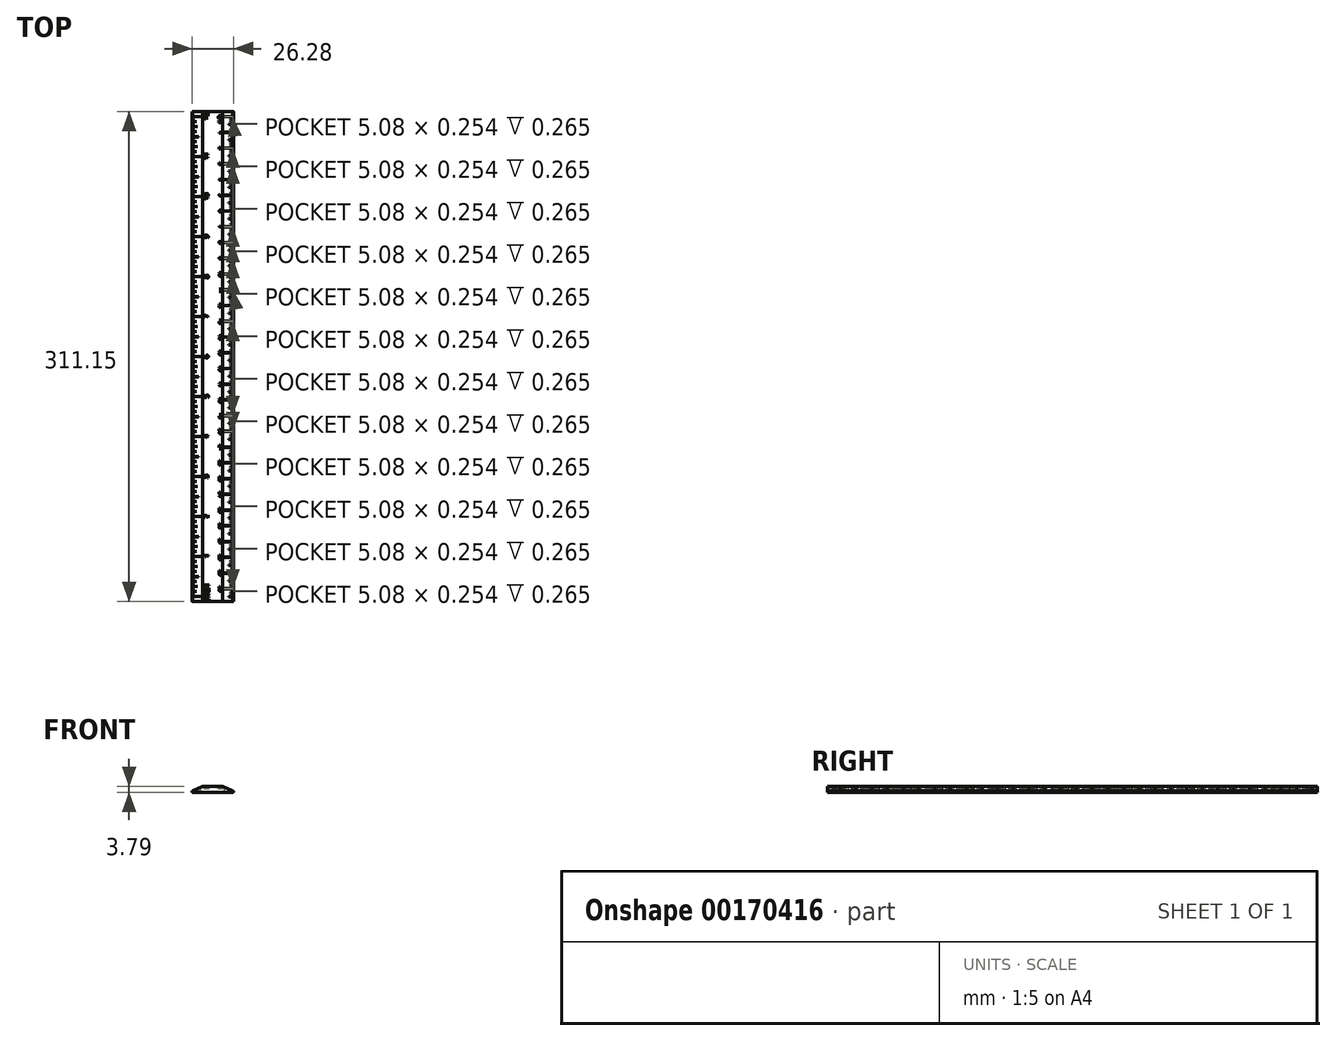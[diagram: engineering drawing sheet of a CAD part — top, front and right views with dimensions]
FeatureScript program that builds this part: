
annotation { "Feature Type Name" : "Feature", "Feature Type Description" : "" }
export const myFeature = defineFeature(function(context is Context, id is Id, definition is map)
    precondition{}
    {
        {
            var Q0;
            Q0=qCreatedBy(makeId("Front.planeOp"),FACE);
            var sketch = newSketch(context, id + "F0", { "sketchPlane" : qUnion([Q0])});
            skLineSegment(sketch, "E0", {"start": v(0, 0) * mm, "end": v(12.7, 0) * mm});
            skLineSegment(sketch, "E1", {"start": v(0, 0) * mm, "end": v(-12.7, 0) * mm});
            skArc(sketch, "E2", {"start": v(-12.7, 0.88) * mm, "mid": v(-13.14, 0.44) * mm, "end": v(-12.7, 0) * mm});
            skLineSegment(sketch, "E3", {"start": v(-12.7, 0.88) * mm, "end": v(-6.35, 3.79) * mm});
            skPoint(sketch, "E3.endSnap0", {"position": v(-6.35, 0) * mm});
            skLineSegment(sketch, "E4", {"start": v(0, 0) * mm, "end": v(0, 3.84) * mm});
            skLineSegment(sketch, "E5.MirrorCS", {"start": v(12.7, 0.88) * mm, "end": v(6.35, 3.79) * mm});
            skArc(sketch, "E6.MirrorCS", {"start": v(12.7, 0.88) * mm, "mid": v(13.14, 0.44) * mm, "end": v(12.7, 0) * mm});
            skLineSegment(sketch, "E7", {"start": v(-6.35, 3.79) * mm, "end": v(6.35, 3.79) * mm});
            skSolve(sketch);
        }
        {
            var Q0;
            Q0 = qSketchRegion(id + "F0", true);
            extrude(context, id + "F1", {"entities" : qUnion([Q0]), "depth" : 311.15 * mm});
        }
        {
            var Q0;
            Q0=makeQuery(id+"F1.opExtrude","SWEPT_FACE",FACE,{"disambiguationData":[OSD([sQuery(id+"F0.wireOp",EDGE,"E7")])]});
            var sketch = newSketch(context, id + "F2", { "sketchPlane" : qUnion([Q0])});
            skLineSegment(sketch, "E8.0.0", {"start": v(-6.35, 0) * mm, "end": v(-12.7, 0) * mm});
            skLineSegment(sketch, "E8.0.1", {"start": v(-12.7, 0) * mm, "end": v(-12.7, -311.15) * mm});
            skLineSegment(sketch, "E8.0.2", {"start": v(-12.7, -311.15) * mm, "end": v(-6.35, -311.15) * mm});
            skLineSegment(sketch, "E8.0.3", {"start": v(-6.35, -311.15) * mm, "end": v(-6.35, 0) * mm});
            skLineSegment(sketch, "E9.0.0", {"start": v(12.7, 0) * mm, "end": v(6.35, 0) * mm});
            skLineSegment(sketch, "E9.0.1", {"start": v(6.35, 0) * mm, "end": v(6.35, -311.15) * mm});
            skLineSegment(sketch, "E9.0.2", {"start": v(6.35, -311.15) * mm, "end": v(12.7, -311.15) * mm});
            skLineSegment(sketch, "E9.0.3", {"start": v(12.7, -311.15) * mm, "end": v(12.7, 0) * mm});
            skLineSegment(sketch, "E10", {"start": v(-12.7, -311.15) * mm, "end": v(-12.7, -308.5) * mm});
            skLineSegment(sketch, "E11", {"start": v(-7.62, -307.98) * mm, "end": v(-7.62, -307.85) * mm});
            skLineSegment(sketch, "E12", {"start": v(-7.62, -307.98) * mm, "end": v(-7.62, -308.1) * mm});
            skLineSegment(sketch, "E13", {"start": v(-7.62, -308.1) * mm, "end": v(-12.7, -308.1) * mm});
            skLineSegment(sketch, "E14", {"start": v(-7.62, -307.85) * mm, "end": v(-12.7, -307.85) * mm});
            skLineSegment(sketch, "E15.0.1.0", {"start": v(-7.62, -282.7) * mm, "end": v(-12.7, -282.7) * mm});
            skLineSegment(sketch, "E15.0.1.1", {"start": v(-7.62, -282.45) * mm, "end": v(-12.7, -282.45) * mm});
            skLineSegment(sketch, "E15.0.1.2", {"start": v(-7.62, -282.58) * mm, "end": v(-7.62, -282.7) * mm});
            skLineSegment(sketch, "E15.0.1.3", {"start": v(-7.62, -282.58) * mm, "end": v(-7.62, -282.45) * mm});
            skLineSegment(sketch, "E15.0.2.0", {"start": v(-7.62, -257.3) * mm, "end": v(-12.7, -257.3) * mm});
            skLineSegment(sketch, "E15.0.2.1", {"start": v(-7.62, -257.05) * mm, "end": v(-12.7, -257.05) * mm});
            skLineSegment(sketch, "E15.0.2.2", {"start": v(-7.62, -257.18) * mm, "end": v(-7.62, -257.3) * mm});
            skLineSegment(sketch, "E15.0.2.3", {"start": v(-7.62, -257.18) * mm, "end": v(-7.62, -257.05) * mm});
            skLineSegment(sketch, "E15.0.3.0", {"start": v(-7.62, -231.9) * mm, "end": v(-12.7, -231.9) * mm});
            skLineSegment(sketch, "E15.0.3.1", {"start": v(-7.62, -231.65) * mm, "end": v(-12.7, -231.65) * mm});
            skLineSegment(sketch, "E15.0.3.2", {"start": v(-7.62, -231.78) * mm, "end": v(-7.62, -231.9) * mm});
            skLineSegment(sketch, "E15.0.3.3", {"start": v(-7.62, -231.78) * mm, "end": v(-7.62, -231.65) * mm});
            skLineSegment(sketch, "E15.0.4.0", {"start": v(-7.62, -206.5) * mm, "end": v(-12.7, -206.5) * mm});
            skLineSegment(sketch, "E15.0.4.1", {"start": v(-7.62, -206.25) * mm, "end": v(-12.7, -206.25) * mm});
            skLineSegment(sketch, "E15.0.4.2", {"start": v(-7.62, -206.38) * mm, "end": v(-7.62, -206.5) * mm});
            skLineSegment(sketch, "E15.0.4.3", {"start": v(-7.62, -206.38) * mm, "end": v(-7.62, -206.25) * mm});
            skLineSegment(sketch, "E15.0.5.0", {"start": v(-7.62, -181.1) * mm, "end": v(-12.7, -181.1) * mm});
            skLineSegment(sketch, "E15.0.5.1", {"start": v(-7.62, -180.85) * mm, "end": v(-12.7, -180.85) * mm});
            skLineSegment(sketch, "E15.0.5.2", {"start": v(-7.62, -180.98) * mm, "end": v(-7.62, -181.1) * mm});
            skLineSegment(sketch, "E15.0.5.3", {"start": v(-7.62, -180.98) * mm, "end": v(-7.62, -180.85) * mm});
            skLineSegment(sketch, "E15.0.6.0", {"start": v(-7.62, -155.7) * mm, "end": v(-12.7, -155.7) * mm});
            skLineSegment(sketch, "E15.0.6.1", {"start": v(-7.62, -155.45) * mm, "end": v(-12.7, -155.45) * mm});
            skLineSegment(sketch, "E15.0.6.2", {"start": v(-7.62, -155.58) * mm, "end": v(-7.62, -155.7) * mm});
            skLineSegment(sketch, "E15.0.6.3", {"start": v(-7.62, -155.58) * mm, "end": v(-7.62, -155.45) * mm});
            skLineSegment(sketch, "E15.0.7.0", {"start": v(-7.62, -130.3) * mm, "end": v(-12.7, -130.3) * mm});
            skLineSegment(sketch, "E15.0.7.1", {"start": v(-7.62, -130.05) * mm, "end": v(-12.7, -130.05) * mm});
            skLineSegment(sketch, "E15.0.7.2", {"start": v(-7.62, -130.18) * mm, "end": v(-7.62, -130.3) * mm});
            skLineSegment(sketch, "E15.0.7.3", {"start": v(-7.62, -130.18) * mm, "end": v(-7.62, -130.05) * mm});
            skLineSegment(sketch, "E15.0.8.0", {"start": v(-7.62, -104.9) * mm, "end": v(-12.7, -104.9) * mm});
            skLineSegment(sketch, "E15.0.8.1", {"start": v(-7.62, -104.65) * mm, "end": v(-12.7, -104.65) * mm});
            skLineSegment(sketch, "E15.0.8.2", {"start": v(-7.62, -104.78) * mm, "end": v(-7.62, -104.9) * mm});
            skLineSegment(sketch, "E15.0.8.3", {"start": v(-7.62, -104.78) * mm, "end": v(-7.62, -104.65) * mm});
            skLineSegment(sketch, "E15.0.9.0", {"start": v(-7.62, -79.5) * mm, "end": v(-12.7, -79.5) * mm});
            skLineSegment(sketch, "E15.0.9.1", {"start": v(-7.62, -79.25) * mm, "end": v(-12.7, -79.25) * mm});
            skLineSegment(sketch, "E15.0.9.2", {"start": v(-7.62, -79.38) * mm, "end": v(-7.62, -79.5) * mm});
            skLineSegment(sketch, "E15.0.9.3", {"start": v(-7.62, -79.38) * mm, "end": v(-7.62, -79.25) * mm});
            skLineSegment(sketch, "E15.0.10.0", {"start": v(-7.62, -54.1) * mm, "end": v(-12.7, -54.1) * mm});
            skLineSegment(sketch, "E15.0.10.1", {"start": v(-7.62, -53.85) * mm, "end": v(-12.7, -53.85) * mm});
            skLineSegment(sketch, "E15.0.10.2", {"start": v(-7.62, -53.98) * mm, "end": v(-7.62, -54.1) * mm});
            skLineSegment(sketch, "E15.0.10.3", {"start": v(-7.62, -53.98) * mm, "end": v(-7.62, -53.85) * mm});
            skLineSegment(sketch, "E15.0.11.0", {"start": v(-7.62, -28.7) * mm, "end": v(-12.7, -28.7) * mm});
            skLineSegment(sketch, "E15.0.11.1", {"start": v(-7.62, -28.45) * mm, "end": v(-12.7, -28.45) * mm});
            skLineSegment(sketch, "E15.0.11.2", {"start": v(-7.62, -28.58) * mm, "end": v(-7.62, -28.7) * mm});
            skLineSegment(sketch, "E15.0.11.3", {"start": v(-7.62, -28.58) * mm, "end": v(-7.62, -28.45) * mm});
            skLineSegment(sketch, "E15.direction1", {"start": v(-12.7, -308.1) * mm, "end": v(12.7, -308.1) * mm, "construction": true});
            skLineSegment(sketch, "E15.direction2", {"start": v(-12.7, -308.1) * mm, "end": v(-12.7, -282.7) * mm, "construction": true});
            skLineSegment(sketch, "E16.0.0.12", {"start": v(-7.62, -3.3) * mm, "end": v(-12.7, -3.3) * mm});
            skLineSegment(sketch, "E16.3.0.12", {"start": v(-7.62, -3.05) * mm, "end": v(-12.7, -3.05) * mm});
            skLineSegment(sketch, "E16.6.0.12", {"start": v(-7.62, -3.18) * mm, "end": v(-7.62, -3.3) * mm});
            skLineSegment(sketch, "E16.9.0.12", {"start": v(-7.62, -3.18) * mm, "end": v(-7.62, -3.05) * mm});
            skLineSegment(sketch, "E17", {"start": v(-12.7, -308.1) * mm, "end": v(-12.7, -307.85) * mm});
            skPoint(sketch, "E18", {"position": v(-12.7, -307.98) * mm});
            skLineSegment(sketch, "E19", {"start": v(-12.7, -307.98) * mm, "end": v(-12.7, -307.25) * mm});
            skLineSegment(sketch, "E20", {"start": v(-12.7, -306.39) * mm, "end": v(-12.7, -306.63) * mm});
            skLineSegment(sketch, "E21", {"start": v(-11.43, -306.39) * mm, "end": v(-11.43, -306.51) * mm});
            skLineSegment(sketch, "E22", {"start": v(-11.43, -306.39) * mm, "end": v(-11.43, -306.26) * mm});
            skLineSegment(sketch, "E23", {"start": v(-11.43, -306.51) * mm, "end": v(-12.7, -306.51) * mm});
            skLineSegment(sketch, "E24", {"start": v(-11.43, -306.26) * mm, "end": v(-12.7, -306.26) * mm});
            skPoint(sketch, "E25.orphan", {"position": v(-12.14, -306.39) * mm});
            skPoint(sketch, "E26.start.orphan", {"position": v(-12.14, -307.98) * mm});
            skLineSegment(sketch, "E27.0.1.0", {"start": v(-11.43, -303.34) * mm, "end": v(-12.7, -303.34) * mm});
            skLineSegment(sketch, "E27.0.1.1", {"start": v(-11.43, -303.09) * mm, "end": v(-12.7, -303.09) * mm});
            skLineSegment(sketch, "E27.0.1.2", {"start": v(-11.43, -303.21) * mm, "end": v(-11.43, -303.34) * mm});
            skLineSegment(sketch, "E27.0.1.3", {"start": v(-11.43, -303.21) * mm, "end": v(-11.43, -303.09) * mm});
            skLineSegment(sketch, "E27.0.2.0", {"start": v(-11.43, -300.16) * mm, "end": v(-12.7, -300.16) * mm});
            skLineSegment(sketch, "E27.0.2.1", {"start": v(-11.43, -299.91) * mm, "end": v(-12.7, -299.91) * mm});
            skLineSegment(sketch, "E27.0.2.2", {"start": v(-11.43, -300.04) * mm, "end": v(-11.43, -300.16) * mm});
            skLineSegment(sketch, "E27.0.2.3", {"start": v(-11.43, -300.04) * mm, "end": v(-11.43, -299.91) * mm});
            skLineSegment(sketch, "E27.0.3.0", {"start": v(-11.43, -296.99) * mm, "end": v(-12.7, -296.99) * mm});
            skLineSegment(sketch, "E27.0.3.1", {"start": v(-11.43, -296.74) * mm, "end": v(-12.7, -296.74) * mm});
            skLineSegment(sketch, "E27.0.3.2", {"start": v(-11.43, -296.86) * mm, "end": v(-11.43, -296.99) * mm});
            skLineSegment(sketch, "E27.0.3.3", {"start": v(-11.43, -296.86) * mm, "end": v(-11.43, -296.74) * mm});
            skLineSegment(sketch, "E27.0.4.0", {"start": v(-11.43, -293.81) * mm, "end": v(-12.7, -293.81) * mm});
            skLineSegment(sketch, "E27.0.4.1", {"start": v(-11.43, -293.56) * mm, "end": v(-12.7, -293.56) * mm});
            skLineSegment(sketch, "E27.0.4.2", {"start": v(-11.43, -293.69) * mm, "end": v(-11.43, -293.81) * mm});
            skLineSegment(sketch, "E27.0.4.3", {"start": v(-11.43, -293.69) * mm, "end": v(-11.43, -293.56) * mm});
            skLineSegment(sketch, "E27.0.5.0", {"start": v(-11.43, -290.64) * mm, "end": v(-12.7, -290.64) * mm});
            skLineSegment(sketch, "E27.0.5.1", {"start": v(-11.43, -290.39) * mm, "end": v(-12.7, -290.39) * mm});
            skLineSegment(sketch, "E27.0.5.2", {"start": v(-11.43, -290.51) * mm, "end": v(-11.43, -290.64) * mm});
            skLineSegment(sketch, "E27.0.5.3", {"start": v(-11.43, -290.51) * mm, "end": v(-11.43, -290.39) * mm});
            skLineSegment(sketch, "E27.0.6.0", {"start": v(-11.43, -287.46) * mm, "end": v(-12.7, -287.46) * mm});
            skLineSegment(sketch, "E27.0.6.1", {"start": v(-11.43, -287.21) * mm, "end": v(-12.7, -287.21) * mm});
            skLineSegment(sketch, "E27.0.6.2", {"start": v(-11.43, -287.34) * mm, "end": v(-11.43, -287.46) * mm});
            skLineSegment(sketch, "E27.0.6.3", {"start": v(-11.43, -287.34) * mm, "end": v(-11.43, -287.21) * mm});
            skLineSegment(sketch, "E27.0.7.0", {"start": v(-11.43, -284.29) * mm, "end": v(-12.7, -284.29) * mm});
            skLineSegment(sketch, "E27.0.7.1", {"start": v(-11.43, -284.04) * mm, "end": v(-12.7, -284.04) * mm});
            skLineSegment(sketch, "E27.0.7.2", {"start": v(-11.43, -284.16) * mm, "end": v(-11.43, -284.29) * mm});
            skLineSegment(sketch, "E27.0.7.3", {"start": v(-11.43, -284.16) * mm, "end": v(-11.43, -284.04) * mm});
            skLineSegment(sketch, "E27.0.8.0", {"start": v(-11.43, -281.11) * mm, "end": v(-12.7, -281.11) * mm});
            skLineSegment(sketch, "E27.0.8.1", {"start": v(-11.43, -280.86) * mm, "end": v(-12.7, -280.86) * mm});
            skLineSegment(sketch, "E27.0.8.2", {"start": v(-11.43, -280.99) * mm, "end": v(-11.43, -281.11) * mm});
            skLineSegment(sketch, "E27.0.8.3", {"start": v(-11.43, -280.99) * mm, "end": v(-11.43, -280.86) * mm});
            skLineSegment(sketch, "E27.0.9.0", {"start": v(-11.43, -277.94) * mm, "end": v(-12.7, -277.94) * mm});
            skLineSegment(sketch, "E27.0.9.1", {"start": v(-11.43, -277.69) * mm, "end": v(-12.7, -277.69) * mm});
            skLineSegment(sketch, "E27.0.9.2", {"start": v(-11.43, -277.81) * mm, "end": v(-11.43, -277.94) * mm});
            skLineSegment(sketch, "E27.0.9.3", {"start": v(-11.43, -277.81) * mm, "end": v(-11.43, -277.69) * mm});
            skLineSegment(sketch, "E27.0.10.0", {"start": v(-11.43, -274.76) * mm, "end": v(-12.7, -274.76) * mm});
            skLineSegment(sketch, "E27.0.10.1", {"start": v(-11.43, -274.51) * mm, "end": v(-12.7, -274.51) * mm});
            skLineSegment(sketch, "E27.0.10.2", {"start": v(-11.43, -274.64) * mm, "end": v(-11.43, -274.76) * mm});
            skLineSegment(sketch, "E27.0.10.3", {"start": v(-11.43, -274.64) * mm, "end": v(-11.43, -274.51) * mm});
            skLineSegment(sketch, "E27.0.11.0", {"start": v(-11.43, -271.59) * mm, "end": v(-12.7, -271.59) * mm});
            skLineSegment(sketch, "E27.0.11.1", {"start": v(-11.43, -271.34) * mm, "end": v(-12.7, -271.34) * mm});
            skLineSegment(sketch, "E27.0.11.2", {"start": v(-11.43, -271.46) * mm, "end": v(-11.43, -271.59) * mm});
            skLineSegment(sketch, "E27.0.11.3", {"start": v(-11.43, -271.46) * mm, "end": v(-11.43, -271.34) * mm});
            skLineSegment(sketch, "E27.0.12.0", {"start": v(-11.43, -268.41) * mm, "end": v(-12.7, -268.41) * mm});
            skLineSegment(sketch, "E27.0.12.1", {"start": v(-11.43, -268.16) * mm, "end": v(-12.7, -268.16) * mm});
            skLineSegment(sketch, "E27.0.12.2", {"start": v(-11.43, -268.29) * mm, "end": v(-11.43, -268.41) * mm});
            skLineSegment(sketch, "E27.0.12.3", {"start": v(-11.43, -268.29) * mm, "end": v(-11.43, -268.16) * mm});
            skLineSegment(sketch, "E27.0.13.0", {"start": v(-11.43, -265.24) * mm, "end": v(-12.7, -265.24) * mm});
            skLineSegment(sketch, "E27.0.13.1", {"start": v(-11.43, -264.99) * mm, "end": v(-12.7, -264.99) * mm});
            skLineSegment(sketch, "E27.0.13.2", {"start": v(-11.43, -265.11) * mm, "end": v(-11.43, -265.24) * mm});
            skLineSegment(sketch, "E27.0.13.3", {"start": v(-11.43, -265.11) * mm, "end": v(-11.43, -264.99) * mm});
            skLineSegment(sketch, "E27.0.14.0", {"start": v(-11.43, -262.06) * mm, "end": v(-12.7, -262.06) * mm});
            skLineSegment(sketch, "E27.0.14.1", {"start": v(-11.43, -261.81) * mm, "end": v(-12.7, -261.81) * mm});
            skLineSegment(sketch, "E27.0.14.2", {"start": v(-11.43, -261.94) * mm, "end": v(-11.43, -262.06) * mm});
            skLineSegment(sketch, "E27.0.14.3", {"start": v(-11.43, -261.94) * mm, "end": v(-11.43, -261.81) * mm});
            skLineSegment(sketch, "E27.0.15.0", {"start": v(-11.43, -258.89) * mm, "end": v(-12.7, -258.89) * mm});
            skLineSegment(sketch, "E27.0.15.1", {"start": v(-11.43, -258.64) * mm, "end": v(-12.7, -258.64) * mm});
            skLineSegment(sketch, "E27.0.15.2", {"start": v(-11.43, -258.76) * mm, "end": v(-11.43, -258.89) * mm});
            skLineSegment(sketch, "E27.0.15.3", {"start": v(-11.43, -258.76) * mm, "end": v(-11.43, -258.64) * mm});
            skLineSegment(sketch, "E27.0.16.0", {"start": v(-11.43, -255.71) * mm, "end": v(-12.7, -255.71) * mm});
            skLineSegment(sketch, "E27.0.16.1", {"start": v(-11.43, -255.46) * mm, "end": v(-12.7, -255.46) * mm});
            skLineSegment(sketch, "E27.0.16.2", {"start": v(-11.43, -255.59) * mm, "end": v(-11.43, -255.71) * mm});
            skLineSegment(sketch, "E27.0.16.3", {"start": v(-11.43, -255.59) * mm, "end": v(-11.43, -255.46) * mm});
            skLineSegment(sketch, "E27.0.17.0", {"start": v(-11.43, -252.54) * mm, "end": v(-12.7, -252.54) * mm});
            skLineSegment(sketch, "E27.0.17.1", {"start": v(-11.43, -252.29) * mm, "end": v(-12.7, -252.29) * mm});
            skLineSegment(sketch, "E27.0.17.2", {"start": v(-11.43, -252.41) * mm, "end": v(-11.43, -252.54) * mm});
            skLineSegment(sketch, "E27.0.17.3", {"start": v(-11.43, -252.41) * mm, "end": v(-11.43, -252.29) * mm});
            skLineSegment(sketch, "E27.0.18.0", {"start": v(-11.43, -249.36) * mm, "end": v(-12.7, -249.36) * mm});
            skLineSegment(sketch, "E27.0.18.1", {"start": v(-11.43, -249.11) * mm, "end": v(-12.7, -249.11) * mm});
            skLineSegment(sketch, "E27.0.18.2", {"start": v(-11.43, -249.24) * mm, "end": v(-11.43, -249.36) * mm});
            skLineSegment(sketch, "E27.0.18.3", {"start": v(-11.43, -249.24) * mm, "end": v(-11.43, -249.11) * mm});
            skLineSegment(sketch, "E27.0.19.0", {"start": v(-11.43, -246.19) * mm, "end": v(-12.7, -246.19) * mm});
            skLineSegment(sketch, "E27.0.19.1", {"start": v(-11.43, -245.94) * mm, "end": v(-12.7, -245.94) * mm});
            skLineSegment(sketch, "E27.0.19.2", {"start": v(-11.43, -246.06) * mm, "end": v(-11.43, -246.19) * mm});
            skLineSegment(sketch, "E27.0.19.3", {"start": v(-11.43, -246.06) * mm, "end": v(-11.43, -245.94) * mm});
            skLineSegment(sketch, "E27.0.20.0", {"start": v(-11.43, -243.01) * mm, "end": v(-12.7, -243.01) * mm});
            skLineSegment(sketch, "E27.0.20.1", {"start": v(-11.43, -242.76) * mm, "end": v(-12.7, -242.76) * mm});
            skLineSegment(sketch, "E27.0.20.2", {"start": v(-11.43, -242.89) * mm, "end": v(-11.43, -243.01) * mm});
            skLineSegment(sketch, "E27.0.20.3", {"start": v(-11.43, -242.89) * mm, "end": v(-11.43, -242.76) * mm});
            skLineSegment(sketch, "E27.0.21.0", {"start": v(-11.43, -239.84) * mm, "end": v(-12.7, -239.84) * mm});
            skLineSegment(sketch, "E27.0.21.1", {"start": v(-11.43, -239.59) * mm, "end": v(-12.7, -239.59) * mm});
            skLineSegment(sketch, "E27.0.21.2", {"start": v(-11.43, -239.71) * mm, "end": v(-11.43, -239.84) * mm});
            skLineSegment(sketch, "E27.0.21.3", {"start": v(-11.43, -239.71) * mm, "end": v(-11.43, -239.59) * mm});
            skLineSegment(sketch, "E27.0.22.0", {"start": v(-11.43, -236.66) * mm, "end": v(-12.7, -236.66) * mm});
            skLineSegment(sketch, "E27.0.22.1", {"start": v(-11.43, -236.41) * mm, "end": v(-12.7, -236.41) * mm});
            skLineSegment(sketch, "E27.0.22.2", {"start": v(-11.43, -236.54) * mm, "end": v(-11.43, -236.66) * mm});
            skLineSegment(sketch, "E27.0.22.3", {"start": v(-11.43, -236.54) * mm, "end": v(-11.43, -236.41) * mm});
            skLineSegment(sketch, "E27.0.23.0", {"start": v(-11.43, -233.49) * mm, "end": v(-12.7, -233.49) * mm});
            skLineSegment(sketch, "E27.0.23.1", {"start": v(-11.43, -233.24) * mm, "end": v(-12.7, -233.24) * mm});
            skLineSegment(sketch, "E27.0.23.2", {"start": v(-11.43, -233.36) * mm, "end": v(-11.43, -233.49) * mm});
            skLineSegment(sketch, "E27.0.23.3", {"start": v(-11.43, -233.36) * mm, "end": v(-11.43, -233.24) * mm});
            skLineSegment(sketch, "E27.0.24.0", {"start": v(-11.43, -230.31) * mm, "end": v(-12.7, -230.31) * mm});
            skLineSegment(sketch, "E27.0.24.1", {"start": v(-11.43, -230.06) * mm, "end": v(-12.7, -230.06) * mm});
            skLineSegment(sketch, "E27.0.24.2", {"start": v(-11.43, -230.19) * mm, "end": v(-11.43, -230.31) * mm});
            skLineSegment(sketch, "E27.0.24.3", {"start": v(-11.43, -230.19) * mm, "end": v(-11.43, -230.06) * mm});
            skLineSegment(sketch, "E27.0.25.0", {"start": v(-11.43, -227.14) * mm, "end": v(-12.7, -227.14) * mm});
            skLineSegment(sketch, "E27.0.25.1", {"start": v(-11.43, -226.89) * mm, "end": v(-12.7, -226.89) * mm});
            skLineSegment(sketch, "E27.0.25.2", {"start": v(-11.43, -227.01) * mm, "end": v(-11.43, -227.14) * mm});
            skLineSegment(sketch, "E27.0.25.3", {"start": v(-11.43, -227.01) * mm, "end": v(-11.43, -226.89) * mm});
            skLineSegment(sketch, "E27.0.26.0", {"start": v(-11.43, -223.96) * mm, "end": v(-12.7, -223.96) * mm});
            skLineSegment(sketch, "E27.0.26.1", {"start": v(-11.43, -223.71) * mm, "end": v(-12.7, -223.71) * mm});
            skLineSegment(sketch, "E27.0.26.2", {"start": v(-11.43, -223.84) * mm, "end": v(-11.43, -223.96) * mm});
            skLineSegment(sketch, "E27.0.26.3", {"start": v(-11.43, -223.84) * mm, "end": v(-11.43, -223.71) * mm});
            skLineSegment(sketch, "E27.0.27.0", {"start": v(-11.43, -220.79) * mm, "end": v(-12.7, -220.79) * mm});
            skLineSegment(sketch, "E27.0.27.1", {"start": v(-11.43, -220.54) * mm, "end": v(-12.7, -220.54) * mm});
            skLineSegment(sketch, "E27.0.27.2", {"start": v(-11.43, -220.66) * mm, "end": v(-11.43, -220.79) * mm});
            skLineSegment(sketch, "E27.0.27.3", {"start": v(-11.43, -220.66) * mm, "end": v(-11.43, -220.54) * mm});
            skLineSegment(sketch, "E27.0.28.0", {"start": v(-11.43, -217.61) * mm, "end": v(-12.7, -217.61) * mm});
            skLineSegment(sketch, "E27.0.28.1", {"start": v(-11.43, -217.36) * mm, "end": v(-12.7, -217.36) * mm});
            skLineSegment(sketch, "E27.0.28.2", {"start": v(-11.43, -217.49) * mm, "end": v(-11.43, -217.61) * mm});
            skLineSegment(sketch, "E27.0.28.3", {"start": v(-11.43, -217.49) * mm, "end": v(-11.43, -217.36) * mm});
            skLineSegment(sketch, "E27.0.29.0", {"start": v(-11.43, -214.44) * mm, "end": v(-12.7, -214.44) * mm});
            skLineSegment(sketch, "E27.0.29.1", {"start": v(-11.43, -214.19) * mm, "end": v(-12.7, -214.19) * mm});
            skLineSegment(sketch, "E27.0.29.2", {"start": v(-11.43, -214.31) * mm, "end": v(-11.43, -214.44) * mm});
            skLineSegment(sketch, "E27.0.29.3", {"start": v(-11.43, -214.31) * mm, "end": v(-11.43, -214.19) * mm});
            skLineSegment(sketch, "E27.0.30.0", {"start": v(-11.43, -211.26) * mm, "end": v(-12.7, -211.26) * mm});
            skLineSegment(sketch, "E27.0.30.1", {"start": v(-11.43, -211.01) * mm, "end": v(-12.7, -211.01) * mm});
            skLineSegment(sketch, "E27.0.30.2", {"start": v(-11.43, -211.14) * mm, "end": v(-11.43, -211.26) * mm});
            skLineSegment(sketch, "E27.0.30.3", {"start": v(-11.43, -211.14) * mm, "end": v(-11.43, -211.01) * mm});
            skLineSegment(sketch, "E27.0.31.0", {"start": v(-11.43, -208.09) * mm, "end": v(-12.7, -208.09) * mm});
            skLineSegment(sketch, "E27.0.31.1", {"start": v(-11.43, -207.84) * mm, "end": v(-12.7, -207.84) * mm});
            skLineSegment(sketch, "E27.0.31.2", {"start": v(-11.43, -207.96) * mm, "end": v(-11.43, -208.09) * mm});
            skLineSegment(sketch, "E27.0.31.3", {"start": v(-11.43, -207.96) * mm, "end": v(-11.43, -207.84) * mm});
            skLineSegment(sketch, "E27.0.32.0", {"start": v(-11.43, -204.91) * mm, "end": v(-12.7, -204.91) * mm});
            skLineSegment(sketch, "E27.0.32.1", {"start": v(-11.43, -204.66) * mm, "end": v(-12.7, -204.66) * mm});
            skLineSegment(sketch, "E27.0.32.2", {"start": v(-11.43, -204.79) * mm, "end": v(-11.43, -204.91) * mm});
            skLineSegment(sketch, "E27.0.32.3", {"start": v(-11.43, -204.79) * mm, "end": v(-11.43, -204.66) * mm});
            skLineSegment(sketch, "E27.0.33.0", {"start": v(-11.43, -201.74) * mm, "end": v(-12.7, -201.74) * mm});
            skLineSegment(sketch, "E27.0.33.1", {"start": v(-11.43, -201.49) * mm, "end": v(-12.7, -201.49) * mm});
            skLineSegment(sketch, "E27.0.33.2", {"start": v(-11.43, -201.61) * mm, "end": v(-11.43, -201.74) * mm});
            skLineSegment(sketch, "E27.0.33.3", {"start": v(-11.43, -201.61) * mm, "end": v(-11.43, -201.49) * mm});
            skLineSegment(sketch, "E27.0.34.0", {"start": v(-11.43, -198.56) * mm, "end": v(-12.7, -198.56) * mm});
            skLineSegment(sketch, "E27.0.34.1", {"start": v(-11.43, -198.31) * mm, "end": v(-12.7, -198.31) * mm});
            skLineSegment(sketch, "E27.0.34.2", {"start": v(-11.43, -198.44) * mm, "end": v(-11.43, -198.56) * mm});
            skLineSegment(sketch, "E27.0.34.3", {"start": v(-11.43, -198.44) * mm, "end": v(-11.43, -198.31) * mm});
            skLineSegment(sketch, "E27.0.35.0", {"start": v(-11.43, -195.39) * mm, "end": v(-12.7, -195.39) * mm});
            skLineSegment(sketch, "E27.0.35.1", {"start": v(-11.43, -195.14) * mm, "end": v(-12.7, -195.14) * mm});
            skLineSegment(sketch, "E27.0.35.2", {"start": v(-11.43, -195.26) * mm, "end": v(-11.43, -195.39) * mm});
            skLineSegment(sketch, "E27.0.35.3", {"start": v(-11.43, -195.26) * mm, "end": v(-11.43, -195.14) * mm});
            skLineSegment(sketch, "E27.0.36.0", {"start": v(-11.43, -192.21) * mm, "end": v(-12.7, -192.21) * mm});
            skLineSegment(sketch, "E27.0.36.1", {"start": v(-11.43, -191.96) * mm, "end": v(-12.7, -191.96) * mm});
            skLineSegment(sketch, "E27.0.36.2", {"start": v(-11.43, -192.09) * mm, "end": v(-11.43, -192.21) * mm});
            skLineSegment(sketch, "E27.0.36.3", {"start": v(-11.43, -192.09) * mm, "end": v(-11.43, -191.96) * mm});
            skLineSegment(sketch, "E27.0.37.0", {"start": v(-11.43, -189.04) * mm, "end": v(-12.7, -189.04) * mm});
            skLineSegment(sketch, "E27.0.37.1", {"start": v(-11.43, -188.79) * mm, "end": v(-12.7, -188.79) * mm});
            skLineSegment(sketch, "E27.0.37.2", {"start": v(-11.43, -188.91) * mm, "end": v(-11.43, -189.04) * mm});
            skLineSegment(sketch, "E27.0.37.3", {"start": v(-11.43, -188.91) * mm, "end": v(-11.43, -188.79) * mm});
            skLineSegment(sketch, "E27.0.38.0", {"start": v(-11.43, -185.86) * mm, "end": v(-12.7, -185.86) * mm});
            skLineSegment(sketch, "E27.0.38.1", {"start": v(-11.43, -185.61) * mm, "end": v(-12.7, -185.61) * mm});
            skLineSegment(sketch, "E27.0.38.2", {"start": v(-11.43, -185.74) * mm, "end": v(-11.43, -185.86) * mm});
            skLineSegment(sketch, "E27.0.38.3", {"start": v(-11.43, -185.74) * mm, "end": v(-11.43, -185.61) * mm});
            skLineSegment(sketch, "E27.0.39.0", {"start": v(-11.43, -182.69) * mm, "end": v(-12.7, -182.69) * mm});
            skLineSegment(sketch, "E27.0.39.1", {"start": v(-11.43, -182.44) * mm, "end": v(-12.7, -182.44) * mm});
            skLineSegment(sketch, "E27.0.39.2", {"start": v(-11.43, -182.56) * mm, "end": v(-11.43, -182.69) * mm});
            skLineSegment(sketch, "E27.0.39.3", {"start": v(-11.43, -182.56) * mm, "end": v(-11.43, -182.44) * mm});
            skLineSegment(sketch, "E27.0.40.0", {"start": v(-11.43, -179.51) * mm, "end": v(-12.7, -179.51) * mm});
            skLineSegment(sketch, "E27.0.40.1", {"start": v(-11.43, -179.26) * mm, "end": v(-12.7, -179.26) * mm});
            skLineSegment(sketch, "E27.0.40.2", {"start": v(-11.43, -179.39) * mm, "end": v(-11.43, -179.51) * mm});
            skLineSegment(sketch, "E27.0.40.3", {"start": v(-11.43, -179.39) * mm, "end": v(-11.43, -179.26) * mm});
            skLineSegment(sketch, "E27.0.41.0", {"start": v(-11.43, -176.34) * mm, "end": v(-12.7, -176.34) * mm});
            skLineSegment(sketch, "E27.0.41.1", {"start": v(-11.43, -176.09) * mm, "end": v(-12.7, -176.09) * mm});
            skLineSegment(sketch, "E27.0.41.2", {"start": v(-11.43, -176.21) * mm, "end": v(-11.43, -176.34) * mm});
            skLineSegment(sketch, "E27.0.41.3", {"start": v(-11.43, -176.21) * mm, "end": v(-11.43, -176.09) * mm});
            skLineSegment(sketch, "E27.0.42.0", {"start": v(-11.43, -173.16) * mm, "end": v(-12.7, -173.16) * mm});
            skLineSegment(sketch, "E27.0.42.1", {"start": v(-11.43, -172.91) * mm, "end": v(-12.7, -172.91) * mm});
            skLineSegment(sketch, "E27.0.42.2", {"start": v(-11.43, -173.04) * mm, "end": v(-11.43, -173.16) * mm});
            skLineSegment(sketch, "E27.0.42.3", {"start": v(-11.43, -173.04) * mm, "end": v(-11.43, -172.91) * mm});
            skLineSegment(sketch, "E27.0.43.0", {"start": v(-11.43, -169.99) * mm, "end": v(-12.7, -169.99) * mm});
            skLineSegment(sketch, "E27.0.43.1", {"start": v(-11.43, -169.74) * mm, "end": v(-12.7, -169.74) * mm});
            skLineSegment(sketch, "E27.0.43.2", {"start": v(-11.43, -169.86) * mm, "end": v(-11.43, -169.99) * mm});
            skLineSegment(sketch, "E27.0.43.3", {"start": v(-11.43, -169.86) * mm, "end": v(-11.43, -169.74) * mm});
            skLineSegment(sketch, "E27.0.44.0", {"start": v(-11.43, -166.81) * mm, "end": v(-12.7, -166.81) * mm});
            skLineSegment(sketch, "E27.0.44.1", {"start": v(-11.43, -166.56) * mm, "end": v(-12.7, -166.56) * mm});
            skLineSegment(sketch, "E27.0.44.2", {"start": v(-11.43, -166.69) * mm, "end": v(-11.43, -166.81) * mm});
            skLineSegment(sketch, "E27.0.44.3", {"start": v(-11.43, -166.69) * mm, "end": v(-11.43, -166.56) * mm});
            skLineSegment(sketch, "E27.0.45.0", {"start": v(-11.43, -163.64) * mm, "end": v(-12.7, -163.64) * mm});
            skLineSegment(sketch, "E27.0.45.1", {"start": v(-11.43, -163.39) * mm, "end": v(-12.7, -163.39) * mm});
            skLineSegment(sketch, "E27.0.45.2", {"start": v(-11.43, -163.51) * mm, "end": v(-11.43, -163.64) * mm});
            skLineSegment(sketch, "E27.0.45.3", {"start": v(-11.43, -163.51) * mm, "end": v(-11.43, -163.39) * mm});
            skLineSegment(sketch, "E27.0.46.0", {"start": v(-11.43, -160.46) * mm, "end": v(-12.7, -160.46) * mm});
            skLineSegment(sketch, "E27.0.46.1", {"start": v(-11.43, -160.21) * mm, "end": v(-12.7, -160.21) * mm});
            skLineSegment(sketch, "E27.0.46.2", {"start": v(-11.43, -160.34) * mm, "end": v(-11.43, -160.46) * mm});
            skLineSegment(sketch, "E27.0.46.3", {"start": v(-11.43, -160.34) * mm, "end": v(-11.43, -160.21) * mm});
            skLineSegment(sketch, "E27.0.47.0", {"start": v(-11.43, -157.29) * mm, "end": v(-12.7, -157.29) * mm});
            skLineSegment(sketch, "E27.0.47.1", {"start": v(-11.43, -157.04) * mm, "end": v(-12.7, -157.04) * mm});
            skLineSegment(sketch, "E27.0.47.2", {"start": v(-11.43, -157.16) * mm, "end": v(-11.43, -157.29) * mm});
            skLineSegment(sketch, "E27.0.47.3", {"start": v(-11.43, -157.16) * mm, "end": v(-11.43, -157.04) * mm});
            skLineSegment(sketch, "E27.0.48.0", {"start": v(-11.43, -154.11) * mm, "end": v(-12.7, -154.11) * mm});
            skLineSegment(sketch, "E27.0.48.1", {"start": v(-11.43, -153.86) * mm, "end": v(-12.7, -153.86) * mm});
            skLineSegment(sketch, "E27.0.48.2", {"start": v(-11.43, -153.99) * mm, "end": v(-11.43, -154.11) * mm});
            skLineSegment(sketch, "E27.0.48.3", {"start": v(-11.43, -153.99) * mm, "end": v(-11.43, -153.86) * mm});
            skLineSegment(sketch, "E27.0.49.0", {"start": v(-11.43, -150.94) * mm, "end": v(-12.7, -150.94) * mm});
            skLineSegment(sketch, "E27.0.49.1", {"start": v(-11.43, -150.69) * mm, "end": v(-12.7, -150.69) * mm});
            skLineSegment(sketch, "E27.0.49.2", {"start": v(-11.43, -150.81) * mm, "end": v(-11.43, -150.94) * mm});
            skLineSegment(sketch, "E27.0.49.3", {"start": v(-11.43, -150.81) * mm, "end": v(-11.43, -150.69) * mm});
            skLineSegment(sketch, "E27.0.50.0", {"start": v(-11.43, -147.76) * mm, "end": v(-12.7, -147.76) * mm});
            skLineSegment(sketch, "E27.0.50.1", {"start": v(-11.43, -147.51) * mm, "end": v(-12.7, -147.51) * mm});
            skLineSegment(sketch, "E27.0.50.2", {"start": v(-11.43, -147.64) * mm, "end": v(-11.43, -147.76) * mm});
            skLineSegment(sketch, "E27.0.50.3", {"start": v(-11.43, -147.64) * mm, "end": v(-11.43, -147.51) * mm});
            skLineSegment(sketch, "E27.0.51.0", {"start": v(-11.43, -144.59) * mm, "end": v(-12.7, -144.59) * mm});
            skLineSegment(sketch, "E27.0.51.1", {"start": v(-11.43, -144.34) * mm, "end": v(-12.7, -144.34) * mm});
            skLineSegment(sketch, "E27.0.51.2", {"start": v(-11.43, -144.46) * mm, "end": v(-11.43, -144.59) * mm});
            skLineSegment(sketch, "E27.0.51.3", {"start": v(-11.43, -144.46) * mm, "end": v(-11.43, -144.34) * mm});
            skLineSegment(sketch, "E27.0.52.0", {"start": v(-11.43, -141.41) * mm, "end": v(-12.7, -141.41) * mm});
            skLineSegment(sketch, "E27.0.52.1", {"start": v(-11.43, -141.16) * mm, "end": v(-12.7, -141.16) * mm});
            skLineSegment(sketch, "E27.0.52.2", {"start": v(-11.43, -141.29) * mm, "end": v(-11.43, -141.41) * mm});
            skLineSegment(sketch, "E27.0.52.3", {"start": v(-11.43, -141.29) * mm, "end": v(-11.43, -141.16) * mm});
            skLineSegment(sketch, "E27.0.53.0", {"start": v(-11.43, -138.24) * mm, "end": v(-12.7, -138.24) * mm});
            skLineSegment(sketch, "E27.0.53.1", {"start": v(-11.43, -137.99) * mm, "end": v(-12.7, -137.99) * mm});
            skLineSegment(sketch, "E27.0.53.2", {"start": v(-11.43, -138.11) * mm, "end": v(-11.43, -138.24) * mm});
            skLineSegment(sketch, "E27.0.53.3", {"start": v(-11.43, -138.11) * mm, "end": v(-11.43, -137.99) * mm});
            skLineSegment(sketch, "E27.0.54.0", {"start": v(-11.43, -135.06) * mm, "end": v(-12.7, -135.06) * mm});
            skLineSegment(sketch, "E27.0.54.1", {"start": v(-11.43, -134.81) * mm, "end": v(-12.7, -134.81) * mm});
            skLineSegment(sketch, "E27.0.54.2", {"start": v(-11.43, -134.94) * mm, "end": v(-11.43, -135.06) * mm});
            skLineSegment(sketch, "E27.0.54.3", {"start": v(-11.43, -134.94) * mm, "end": v(-11.43, -134.81) * mm});
            skLineSegment(sketch, "E27.0.55.0", {"start": v(-11.43, -131.89) * mm, "end": v(-12.7, -131.89) * mm});
            skLineSegment(sketch, "E27.0.55.1", {"start": v(-11.43, -131.64) * mm, "end": v(-12.7, -131.64) * mm});
            skLineSegment(sketch, "E27.0.55.2", {"start": v(-11.43, -131.76) * mm, "end": v(-11.43, -131.89) * mm});
            skLineSegment(sketch, "E27.0.55.3", {"start": v(-11.43, -131.76) * mm, "end": v(-11.43, -131.64) * mm});
            skLineSegment(sketch, "E27.0.56.0", {"start": v(-11.43, -128.71) * mm, "end": v(-12.7, -128.71) * mm});
            skLineSegment(sketch, "E27.0.56.1", {"start": v(-11.43, -128.46) * mm, "end": v(-12.7, -128.46) * mm});
            skLineSegment(sketch, "E27.0.56.2", {"start": v(-11.43, -128.59) * mm, "end": v(-11.43, -128.71) * mm});
            skLineSegment(sketch, "E27.0.56.3", {"start": v(-11.43, -128.59) * mm, "end": v(-11.43, -128.46) * mm});
            skLineSegment(sketch, "E27.0.57.0", {"start": v(-11.43, -125.54) * mm, "end": v(-12.7, -125.54) * mm});
            skLineSegment(sketch, "E27.0.57.1", {"start": v(-11.43, -125.29) * mm, "end": v(-12.7, -125.29) * mm});
            skLineSegment(sketch, "E27.0.57.2", {"start": v(-11.43, -125.41) * mm, "end": v(-11.43, -125.54) * mm});
            skLineSegment(sketch, "E27.0.57.3", {"start": v(-11.43, -125.41) * mm, "end": v(-11.43, -125.29) * mm});
            skLineSegment(sketch, "E27.0.58.0", {"start": v(-11.43, -122.36) * mm, "end": v(-12.7, -122.36) * mm});
            skLineSegment(sketch, "E27.0.58.1", {"start": v(-11.43, -122.11) * mm, "end": v(-12.7, -122.11) * mm});
            skLineSegment(sketch, "E27.0.58.2", {"start": v(-11.43, -122.24) * mm, "end": v(-11.43, -122.36) * mm});
            skLineSegment(sketch, "E27.0.58.3", {"start": v(-11.43, -122.24) * mm, "end": v(-11.43, -122.11) * mm});
            skLineSegment(sketch, "E27.0.59.0", {"start": v(-11.43, -119.19) * mm, "end": v(-12.7, -119.19) * mm});
            skLineSegment(sketch, "E27.0.59.1", {"start": v(-11.43, -118.94) * mm, "end": v(-12.7, -118.94) * mm});
            skLineSegment(sketch, "E27.0.59.2", {"start": v(-11.43, -119.06) * mm, "end": v(-11.43, -119.19) * mm});
            skLineSegment(sketch, "E27.0.59.3", {"start": v(-11.43, -119.06) * mm, "end": v(-11.43, -118.94) * mm});
            skLineSegment(sketch, "E27.0.60.0", {"start": v(-11.43, -116.01) * mm, "end": v(-12.7, -116.01) * mm});
            skLineSegment(sketch, "E27.0.60.1", {"start": v(-11.43, -115.76) * mm, "end": v(-12.7, -115.76) * mm});
            skLineSegment(sketch, "E27.0.60.2", {"start": v(-11.43, -115.89) * mm, "end": v(-11.43, -116.01) * mm});
            skLineSegment(sketch, "E27.0.60.3", {"start": v(-11.43, -115.89) * mm, "end": v(-11.43, -115.76) * mm});
            skLineSegment(sketch, "E27.0.61.0", {"start": v(-11.43, -112.84) * mm, "end": v(-12.7, -112.84) * mm});
            skLineSegment(sketch, "E27.0.61.1", {"start": v(-11.43, -112.59) * mm, "end": v(-12.7, -112.59) * mm});
            skLineSegment(sketch, "E27.0.61.2", {"start": v(-11.43, -112.71) * mm, "end": v(-11.43, -112.84) * mm});
            skLineSegment(sketch, "E27.0.61.3", {"start": v(-11.43, -112.71) * mm, "end": v(-11.43, -112.59) * mm});
            skLineSegment(sketch, "E27.0.62.0", {"start": v(-11.43, -109.66) * mm, "end": v(-12.7, -109.66) * mm});
            skLineSegment(sketch, "E27.0.62.1", {"start": v(-11.43, -109.41) * mm, "end": v(-12.7, -109.41) * mm});
            skLineSegment(sketch, "E27.0.62.2", {"start": v(-11.43, -109.54) * mm, "end": v(-11.43, -109.66) * mm});
            skLineSegment(sketch, "E27.0.62.3", {"start": v(-11.43, -109.54) * mm, "end": v(-11.43, -109.41) * mm});
            skLineSegment(sketch, "E27.0.63.0", {"start": v(-11.43, -106.49) * mm, "end": v(-12.7, -106.49) * mm});
            skLineSegment(sketch, "E27.0.63.1", {"start": v(-11.43, -106.24) * mm, "end": v(-12.7, -106.24) * mm});
            skLineSegment(sketch, "E27.0.63.2", {"start": v(-11.43, -106.36) * mm, "end": v(-11.43, -106.49) * mm});
            skLineSegment(sketch, "E27.0.63.3", {"start": v(-11.43, -106.36) * mm, "end": v(-11.43, -106.24) * mm});
            skLineSegment(sketch, "E27.0.64.0", {"start": v(-11.43, -103.31) * mm, "end": v(-12.7, -103.31) * mm});
            skLineSegment(sketch, "E27.0.64.1", {"start": v(-11.43, -103.06) * mm, "end": v(-12.7, -103.06) * mm});
            skLineSegment(sketch, "E27.0.64.2", {"start": v(-11.43, -103.19) * mm, "end": v(-11.43, -103.31) * mm});
            skLineSegment(sketch, "E27.0.64.3", {"start": v(-11.43, -103.19) * mm, "end": v(-11.43, -103.06) * mm});
            skLineSegment(sketch, "E27.0.65.0", {"start": v(-11.43, -100.14) * mm, "end": v(-12.7, -100.14) * mm});
            skLineSegment(sketch, "E27.0.65.1", {"start": v(-11.43, -99.89) * mm, "end": v(-12.7, -99.89) * mm});
            skLineSegment(sketch, "E27.0.65.2", {"start": v(-11.43, -100.01) * mm, "end": v(-11.43, -100.14) * mm});
            skLineSegment(sketch, "E27.0.65.3", {"start": v(-11.43, -100.01) * mm, "end": v(-11.43, -99.89) * mm});
            skLineSegment(sketch, "E27.0.66.0", {"start": v(-11.43, -96.96) * mm, "end": v(-12.7, -96.96) * mm});
            skLineSegment(sketch, "E27.0.66.1", {"start": v(-11.43, -96.71) * mm, "end": v(-12.7, -96.71) * mm});
            skLineSegment(sketch, "E27.0.66.2", {"start": v(-11.43, -96.84) * mm, "end": v(-11.43, -96.96) * mm});
            skLineSegment(sketch, "E27.0.66.3", {"start": v(-11.43, -96.84) * mm, "end": v(-11.43, -96.71) * mm});
            skLineSegment(sketch, "E27.0.67.0", {"start": v(-11.43, -93.79) * mm, "end": v(-12.7, -93.79) * mm});
            skLineSegment(sketch, "E27.0.67.1", {"start": v(-11.43, -93.54) * mm, "end": v(-12.7, -93.54) * mm});
            skLineSegment(sketch, "E27.0.67.2", {"start": v(-11.43, -93.66) * mm, "end": v(-11.43, -93.79) * mm});
            skLineSegment(sketch, "E27.0.67.3", {"start": v(-11.43, -93.66) * mm, "end": v(-11.43, -93.54) * mm});
            skLineSegment(sketch, "E27.0.68.0", {"start": v(-11.43, -90.61) * mm, "end": v(-12.7, -90.61) * mm});
            skLineSegment(sketch, "E27.0.68.1", {"start": v(-11.43, -90.36) * mm, "end": v(-12.7, -90.36) * mm});
            skLineSegment(sketch, "E27.0.68.2", {"start": v(-11.43, -90.49) * mm, "end": v(-11.43, -90.61) * mm});
            skLineSegment(sketch, "E27.0.68.3", {"start": v(-11.43, -90.49) * mm, "end": v(-11.43, -90.36) * mm});
            skLineSegment(sketch, "E27.0.69.0", {"start": v(-11.43, -87.44) * mm, "end": v(-12.7, -87.44) * mm});
            skLineSegment(sketch, "E27.0.69.1", {"start": v(-11.43, -87.19) * mm, "end": v(-12.7, -87.19) * mm});
            skLineSegment(sketch, "E27.0.69.2", {"start": v(-11.43, -87.31) * mm, "end": v(-11.43, -87.44) * mm});
            skLineSegment(sketch, "E27.0.69.3", {"start": v(-11.43, -87.31) * mm, "end": v(-11.43, -87.19) * mm});
            skLineSegment(sketch, "E27.0.70.0", {"start": v(-11.43, -84.26) * mm, "end": v(-12.7, -84.26) * mm});
            skLineSegment(sketch, "E27.0.70.1", {"start": v(-11.43, -84.01) * mm, "end": v(-12.7, -84.01) * mm});
            skLineSegment(sketch, "E27.0.70.2", {"start": v(-11.43, -84.14) * mm, "end": v(-11.43, -84.26) * mm});
            skLineSegment(sketch, "E27.0.70.3", {"start": v(-11.43, -84.14) * mm, "end": v(-11.43, -84.01) * mm});
            skLineSegment(sketch, "E27.0.71.0", {"start": v(-11.43, -81.09) * mm, "end": v(-12.7, -81.09) * mm});
            skLineSegment(sketch, "E27.0.71.1", {"start": v(-11.43, -80.84) * mm, "end": v(-12.7, -80.84) * mm});
            skLineSegment(sketch, "E27.0.71.2", {"start": v(-11.43, -80.96) * mm, "end": v(-11.43, -81.09) * mm});
            skLineSegment(sketch, "E27.0.71.3", {"start": v(-11.43, -80.96) * mm, "end": v(-11.43, -80.84) * mm});
            skLineSegment(sketch, "E27.0.72.0", {"start": v(-11.43, -77.91) * mm, "end": v(-12.7, -77.91) * mm});
            skLineSegment(sketch, "E27.0.72.1", {"start": v(-11.43, -77.66) * mm, "end": v(-12.7, -77.66) * mm});
            skLineSegment(sketch, "E27.0.72.2", {"start": v(-11.43, -77.79) * mm, "end": v(-11.43, -77.91) * mm});
            skLineSegment(sketch, "E27.0.72.3", {"start": v(-11.43, -77.79) * mm, "end": v(-11.43, -77.66) * mm});
            skLineSegment(sketch, "E27.0.73.0", {"start": v(-11.43, -74.74) * mm, "end": v(-12.7, -74.74) * mm});
            skLineSegment(sketch, "E27.0.73.1", {"start": v(-11.43, -74.49) * mm, "end": v(-12.7, -74.49) * mm});
            skLineSegment(sketch, "E27.0.73.2", {"start": v(-11.43, -74.61) * mm, "end": v(-11.43, -74.74) * mm});
            skLineSegment(sketch, "E27.0.73.3", {"start": v(-11.43, -74.61) * mm, "end": v(-11.43, -74.49) * mm});
            skLineSegment(sketch, "E27.0.74.0", {"start": v(-11.43, -71.56) * mm, "end": v(-12.7, -71.56) * mm});
            skLineSegment(sketch, "E27.0.74.1", {"start": v(-11.43, -71.31) * mm, "end": v(-12.7, -71.31) * mm});
            skLineSegment(sketch, "E27.0.74.2", {"start": v(-11.43, -71.44) * mm, "end": v(-11.43, -71.56) * mm});
            skLineSegment(sketch, "E27.0.74.3", {"start": v(-11.43, -71.44) * mm, "end": v(-11.43, -71.31) * mm});
            skLineSegment(sketch, "E27.0.75.0", {"start": v(-11.43, -68.39) * mm, "end": v(-12.7, -68.39) * mm});
            skLineSegment(sketch, "E27.0.75.1", {"start": v(-11.43, -68.14) * mm, "end": v(-12.7, -68.14) * mm});
            skLineSegment(sketch, "E27.0.75.2", {"start": v(-11.43, -68.26) * mm, "end": v(-11.43, -68.39) * mm});
            skLineSegment(sketch, "E27.0.75.3", {"start": v(-11.43, -68.26) * mm, "end": v(-11.43, -68.14) * mm});
            skLineSegment(sketch, "E27.0.76.0", {"start": v(-11.43, -65.21) * mm, "end": v(-12.7, -65.21) * mm});
            skLineSegment(sketch, "E27.0.76.1", {"start": v(-11.43, -64.96) * mm, "end": v(-12.7, -64.96) * mm});
            skLineSegment(sketch, "E27.0.76.2", {"start": v(-11.43, -65.09) * mm, "end": v(-11.43, -65.21) * mm});
            skLineSegment(sketch, "E27.0.76.3", {"start": v(-11.43, -65.09) * mm, "end": v(-11.43, -64.96) * mm});
            skLineSegment(sketch, "E27.0.77.0", {"start": v(-11.43, -62.04) * mm, "end": v(-12.7, -62.04) * mm});
            skLineSegment(sketch, "E27.0.77.1", {"start": v(-11.43, -61.79) * mm, "end": v(-12.7, -61.79) * mm});
            skLineSegment(sketch, "E27.0.77.2", {"start": v(-11.43, -61.91) * mm, "end": v(-11.43, -62.04) * mm});
            skLineSegment(sketch, "E27.0.77.3", {"start": v(-11.43, -61.91) * mm, "end": v(-11.43, -61.79) * mm});
            skLineSegment(sketch, "E27.0.78.0", {"start": v(-11.43, -58.86) * mm, "end": v(-12.7, -58.86) * mm});
            skLineSegment(sketch, "E27.0.78.1", {"start": v(-11.43, -58.61) * mm, "end": v(-12.7, -58.61) * mm});
            skLineSegment(sketch, "E27.0.78.2", {"start": v(-11.43, -58.74) * mm, "end": v(-11.43, -58.86) * mm});
            skLineSegment(sketch, "E27.0.78.3", {"start": v(-11.43, -58.74) * mm, "end": v(-11.43, -58.61) * mm});
            skLineSegment(sketch, "E27.0.79.0", {"start": v(-11.43, -55.69) * mm, "end": v(-12.7, -55.69) * mm});
            skLineSegment(sketch, "E27.0.79.1", {"start": v(-11.43, -55.44) * mm, "end": v(-12.7, -55.44) * mm});
            skLineSegment(sketch, "E27.0.79.2", {"start": v(-11.43, -55.56) * mm, "end": v(-11.43, -55.69) * mm});
            skLineSegment(sketch, "E27.0.79.3", {"start": v(-11.43, -55.56) * mm, "end": v(-11.43, -55.44) * mm});
            skLineSegment(sketch, "E27.0.80.0", {"start": v(-11.43, -52.51) * mm, "end": v(-12.7, -52.51) * mm});
            skLineSegment(sketch, "E27.0.80.1", {"start": v(-11.43, -52.26) * mm, "end": v(-12.7, -52.26) * mm});
            skLineSegment(sketch, "E27.0.80.2", {"start": v(-11.43, -52.39) * mm, "end": v(-11.43, -52.51) * mm});
            skLineSegment(sketch, "E27.0.80.3", {"start": v(-11.43, -52.39) * mm, "end": v(-11.43, -52.26) * mm});
            skLineSegment(sketch, "E27.0.81.0", {"start": v(-11.43, -49.34) * mm, "end": v(-12.7, -49.34) * mm});
            skLineSegment(sketch, "E27.0.81.1", {"start": v(-11.43, -49.09) * mm, "end": v(-12.7, -49.09) * mm});
            skLineSegment(sketch, "E27.0.81.2", {"start": v(-11.43, -49.21) * mm, "end": v(-11.43, -49.34) * mm});
            skLineSegment(sketch, "E27.0.81.3", {"start": v(-11.43, -49.21) * mm, "end": v(-11.43, -49.09) * mm});
            skLineSegment(sketch, "E27.0.82.0", {"start": v(-11.43, -46.16) * mm, "end": v(-12.7, -46.16) * mm});
            skLineSegment(sketch, "E27.0.82.1", {"start": v(-11.43, -45.91) * mm, "end": v(-12.7, -45.91) * mm});
            skLineSegment(sketch, "E27.0.82.2", {"start": v(-11.43, -46.04) * mm, "end": v(-11.43, -46.16) * mm});
            skLineSegment(sketch, "E27.0.82.3", {"start": v(-11.43, -46.04) * mm, "end": v(-11.43, -45.91) * mm});
            skLineSegment(sketch, "E27.0.83.0", {"start": v(-11.43, -42.99) * mm, "end": v(-12.7, -42.99) * mm});
            skLineSegment(sketch, "E27.0.83.1", {"start": v(-11.43, -42.74) * mm, "end": v(-12.7, -42.74) * mm});
            skLineSegment(sketch, "E27.0.83.2", {"start": v(-11.43, -42.86) * mm, "end": v(-11.43, -42.99) * mm});
            skLineSegment(sketch, "E27.0.83.3", {"start": v(-11.43, -42.86) * mm, "end": v(-11.43, -42.74) * mm});
            skLineSegment(sketch, "E27.0.84.0", {"start": v(-11.43, -39.81) * mm, "end": v(-12.7, -39.81) * mm});
            skLineSegment(sketch, "E27.0.84.1", {"start": v(-11.43, -39.56) * mm, "end": v(-12.7, -39.56) * mm});
            skLineSegment(sketch, "E27.0.84.2", {"start": v(-11.43, -39.69) * mm, "end": v(-11.43, -39.81) * mm});
            skLineSegment(sketch, "E27.0.84.3", {"start": v(-11.43, -39.69) * mm, "end": v(-11.43, -39.56) * mm});
            skLineSegment(sketch, "E27.0.85.0", {"start": v(-11.43, -36.64) * mm, "end": v(-12.7, -36.64) * mm});
            skLineSegment(sketch, "E27.0.85.1", {"start": v(-11.43, -36.39) * mm, "end": v(-12.7, -36.39) * mm});
            skLineSegment(sketch, "E27.0.85.2", {"start": v(-11.43, -36.51) * mm, "end": v(-11.43, -36.64) * mm});
            skLineSegment(sketch, "E27.0.85.3", {"start": v(-11.43, -36.51) * mm, "end": v(-11.43, -36.39) * mm});
            skLineSegment(sketch, "E27.0.86.0", {"start": v(-11.43, -33.46) * mm, "end": v(-12.7, -33.46) * mm});
            skLineSegment(sketch, "E27.0.86.1", {"start": v(-11.43, -33.21) * mm, "end": v(-12.7, -33.21) * mm});
            skLineSegment(sketch, "E27.0.86.2", {"start": v(-11.43, -33.34) * mm, "end": v(-11.43, -33.46) * mm});
            skLineSegment(sketch, "E27.0.86.3", {"start": v(-11.43, -33.34) * mm, "end": v(-11.43, -33.21) * mm});
            skLineSegment(sketch, "E27.0.87.0", {"start": v(-11.43, -30.29) * mm, "end": v(-12.7, -30.29) * mm});
            skLineSegment(sketch, "E27.0.87.1", {"start": v(-11.43, -30.04) * mm, "end": v(-12.7, -30.04) * mm});
            skLineSegment(sketch, "E27.0.87.2", {"start": v(-11.43, -30.16) * mm, "end": v(-11.43, -30.29) * mm});
            skLineSegment(sketch, "E27.0.87.3", {"start": v(-11.43, -30.16) * mm, "end": v(-11.43, -30.04) * mm});
            skLineSegment(sketch, "E27.0.88.0", {"start": v(-11.43, -27.11) * mm, "end": v(-12.7, -27.11) * mm});
            skLineSegment(sketch, "E27.0.88.1", {"start": v(-11.43, -26.86) * mm, "end": v(-12.7, -26.86) * mm});
            skLineSegment(sketch, "E27.0.88.2", {"start": v(-11.43, -26.99) * mm, "end": v(-11.43, -27.11) * mm});
            skLineSegment(sketch, "E27.0.88.3", {"start": v(-11.43, -26.99) * mm, "end": v(-11.43, -26.86) * mm});
            skLineSegment(sketch, "E27.0.89.0", {"start": v(-11.43, -23.94) * mm, "end": v(-12.7, -23.94) * mm});
            skLineSegment(sketch, "E27.0.89.1", {"start": v(-11.43, -23.69) * mm, "end": v(-12.7, -23.69) * mm});
            skLineSegment(sketch, "E27.0.89.2", {"start": v(-11.43, -23.81) * mm, "end": v(-11.43, -23.94) * mm});
            skLineSegment(sketch, "E27.0.89.3", {"start": v(-11.43, -23.81) * mm, "end": v(-11.43, -23.69) * mm});
            skLineSegment(sketch, "E27.0.90.0", {"start": v(-11.43, -20.76) * mm, "end": v(-12.7, -20.76) * mm});
            skLineSegment(sketch, "E27.0.90.1", {"start": v(-11.43, -20.51) * mm, "end": v(-12.7, -20.51) * mm});
            skLineSegment(sketch, "E27.0.90.2", {"start": v(-11.43, -20.64) * mm, "end": v(-11.43, -20.76) * mm});
            skLineSegment(sketch, "E27.0.90.3", {"start": v(-11.43, -20.64) * mm, "end": v(-11.43, -20.51) * mm});
            skLineSegment(sketch, "E27.0.91.0", {"start": v(-11.43, -17.59) * mm, "end": v(-12.7, -17.59) * mm});
            skLineSegment(sketch, "E27.0.91.1", {"start": v(-11.43, -17.34) * mm, "end": v(-12.7, -17.34) * mm});
            skLineSegment(sketch, "E27.0.91.2", {"start": v(-11.43, -17.46) * mm, "end": v(-11.43, -17.59) * mm});
            skLineSegment(sketch, "E27.0.91.3", {"start": v(-11.43, -17.46) * mm, "end": v(-11.43, -17.34) * mm});
            skLineSegment(sketch, "E27.0.92.0", {"start": v(-11.43, -14.41) * mm, "end": v(-12.7, -14.41) * mm});
            skLineSegment(sketch, "E27.0.92.1", {"start": v(-11.43, -14.16) * mm, "end": v(-12.7, -14.16) * mm});
            skLineSegment(sketch, "E27.0.92.2", {"start": v(-11.43, -14.29) * mm, "end": v(-11.43, -14.41) * mm});
            skLineSegment(sketch, "E27.0.92.3", {"start": v(-11.43, -14.29) * mm, "end": v(-11.43, -14.16) * mm});
            skLineSegment(sketch, "E27.0.93.0", {"start": v(-11.43, -11.24) * mm, "end": v(-12.7, -11.24) * mm});
            skLineSegment(sketch, "E27.0.93.1", {"start": v(-11.43, -10.99) * mm, "end": v(-12.7, -10.99) * mm});
            skLineSegment(sketch, "E27.0.93.2", {"start": v(-11.43, -11.11) * mm, "end": v(-11.43, -11.24) * mm});
            skLineSegment(sketch, "E27.0.93.3", {"start": v(-11.43, -11.11) * mm, "end": v(-11.43, -10.99) * mm});
            skLineSegment(sketch, "E27.0.94.0", {"start": v(-11.43, -8.06) * mm, "end": v(-12.7, -8.06) * mm});
            skLineSegment(sketch, "E27.0.94.1", {"start": v(-11.43, -7.81) * mm, "end": v(-12.7, -7.81) * mm});
            skLineSegment(sketch, "E27.0.94.2", {"start": v(-11.43, -7.94) * mm, "end": v(-11.43, -8.06) * mm});
            skLineSegment(sketch, "E27.0.94.3", {"start": v(-11.43, -7.94) * mm, "end": v(-11.43, -7.81) * mm});
            skLineSegment(sketch, "E27.0.95.0", {"start": v(-11.43, -4.89) * mm, "end": v(-12.7, -4.89) * mm});
            skLineSegment(sketch, "E27.0.95.1", {"start": v(-11.43, -4.64) * mm, "end": v(-12.7, -4.64) * mm});
            skLineSegment(sketch, "E27.0.95.2", {"start": v(-11.43, -4.76) * mm, "end": v(-11.43, -4.89) * mm});
            skLineSegment(sketch, "E27.0.95.3", {"start": v(-11.43, -4.76) * mm, "end": v(-11.43, -4.64) * mm});
            skLineSegment(sketch, "E27.direction1", {"start": v(-12.7, -306.51) * mm, "end": v(12.7, -306.51) * mm, "construction": true});
            skLineSegment(sketch, "E27.direction2", {"start": v(-12.7, -306.51) * mm, "end": v(-12.7, -303.34) * mm, "construction": true});
            skLineSegment(sketch, "E28", {"start": v(-12.14, -306.39) * mm, "end": v(-12.14, -306.26) * mm});
            skLineSegment(sketch, "E29", {"start": v(-12.14, -304.67) * mm, "end": v(-12.7, -304.67) * mm});
            skLineSegment(sketch, "E30", {"start": v(-12.7, -304.67) * mm, "end": v(-10.16, -304.67) * mm});
            skLineSegment(sketch, "E31", {"start": v(-10.16, -304.67) * mm, "end": v(-10.16, -304.93) * mm});
            skLineSegment(sketch, "E32", {"start": v(-10.16, -304.93) * mm, "end": v(-12.7, -304.93) * mm});
            skLineSegment(sketch, "E33.0.1.0", {"start": v(-10.16, -298.58) * mm, "end": v(-12.7, -298.58) * mm});
            skLineSegment(sketch, "E33.0.1.1", {"start": v(-12.7, -298.32) * mm, "end": v(-10.16, -298.32) * mm});
            skLineSegment(sketch, "E33.0.1.2", {"start": v(-10.16, -298.32) * mm, "end": v(-10.16, -298.58) * mm});
            skLineSegment(sketch, "E33.0.2.0", {"start": v(-10.16, -292.23) * mm, "end": v(-12.7, -292.23) * mm});
            skLineSegment(sketch, "E33.0.2.1", {"start": v(-12.7, -291.97) * mm, "end": v(-10.16, -291.97) * mm});
            skLineSegment(sketch, "E33.0.2.2", {"start": v(-10.16, -291.97) * mm, "end": v(-10.16, -292.23) * mm});
            skLineSegment(sketch, "E33.0.3.0", {"start": v(-10.16, -285.88) * mm, "end": v(-12.7, -285.88) * mm});
            skLineSegment(sketch, "E33.0.3.1", {"start": v(-12.7, -285.62) * mm, "end": v(-10.16, -285.62) * mm});
            skLineSegment(sketch, "E33.0.3.2", {"start": v(-10.16, -285.62) * mm, "end": v(-10.16, -285.88) * mm});
            skLineSegment(sketch, "E33.0.4.0", {"start": v(-10.16, -279.53) * mm, "end": v(-12.7, -279.53) * mm});
            skLineSegment(sketch, "E33.0.4.1", {"start": v(-12.7, -279.27) * mm, "end": v(-10.16, -279.27) * mm});
            skLineSegment(sketch, "E33.0.4.2", {"start": v(-10.16, -279.27) * mm, "end": v(-10.16, -279.53) * mm});
            skLineSegment(sketch, "E33.0.5.0", {"start": v(-10.16, -273.18) * mm, "end": v(-12.7, -273.18) * mm});
            skLineSegment(sketch, "E33.0.5.1", {"start": v(-12.7, -272.92) * mm, "end": v(-10.16, -272.92) * mm});
            skLineSegment(sketch, "E33.0.5.2", {"start": v(-10.16, -272.92) * mm, "end": v(-10.16, -273.18) * mm});
            skLineSegment(sketch, "E33.0.6.0", {"start": v(-10.16, -266.83) * mm, "end": v(-12.7, -266.83) * mm});
            skLineSegment(sketch, "E33.0.6.1", {"start": v(-12.7, -266.57) * mm, "end": v(-10.16, -266.57) * mm});
            skLineSegment(sketch, "E33.0.6.2", {"start": v(-10.16, -266.57) * mm, "end": v(-10.16, -266.83) * mm});
            skLineSegment(sketch, "E33.0.7.0", {"start": v(-10.16, -260.48) * mm, "end": v(-12.7, -260.48) * mm});
            skLineSegment(sketch, "E33.0.7.1", {"start": v(-12.7, -260.22) * mm, "end": v(-10.16, -260.22) * mm});
            skLineSegment(sketch, "E33.0.7.2", {"start": v(-10.16, -260.22) * mm, "end": v(-10.16, -260.48) * mm});
            skLineSegment(sketch, "E33.0.8.0", {"start": v(-10.16, -254.13) * mm, "end": v(-12.7, -254.13) * mm});
            skLineSegment(sketch, "E33.0.8.1", {"start": v(-12.7, -253.87) * mm, "end": v(-10.16, -253.87) * mm});
            skLineSegment(sketch, "E33.0.8.2", {"start": v(-10.16, -253.87) * mm, "end": v(-10.16, -254.13) * mm});
            skLineSegment(sketch, "E33.0.9.0", {"start": v(-10.16, -247.78) * mm, "end": v(-12.7, -247.78) * mm});
            skLineSegment(sketch, "E33.0.9.1", {"start": v(-12.7, -247.52) * mm, "end": v(-10.16, -247.52) * mm});
            skLineSegment(sketch, "E33.0.9.2", {"start": v(-10.16, -247.52) * mm, "end": v(-10.16, -247.78) * mm});
            skLineSegment(sketch, "E33.0.10.0", {"start": v(-10.16, -241.43) * mm, "end": v(-12.7, -241.43) * mm});
            skLineSegment(sketch, "E33.0.10.1", {"start": v(-12.7, -241.17) * mm, "end": v(-10.16, -241.17) * mm});
            skLineSegment(sketch, "E33.0.10.2", {"start": v(-10.16, -241.17) * mm, "end": v(-10.16, -241.43) * mm});
            skLineSegment(sketch, "E33.0.11.0", {"start": v(-10.16, -235.08) * mm, "end": v(-12.7, -235.08) * mm});
            skLineSegment(sketch, "E33.0.11.1", {"start": v(-12.7, -234.82) * mm, "end": v(-10.16, -234.82) * mm});
            skLineSegment(sketch, "E33.0.11.2", {"start": v(-10.16, -234.82) * mm, "end": v(-10.16, -235.08) * mm});
            skLineSegment(sketch, "E33.0.12.0", {"start": v(-10.16, -228.73) * mm, "end": v(-12.7, -228.73) * mm});
            skLineSegment(sketch, "E33.0.12.1", {"start": v(-12.7, -228.47) * mm, "end": v(-10.16, -228.47) * mm});
            skLineSegment(sketch, "E33.0.12.2", {"start": v(-10.16, -228.47) * mm, "end": v(-10.16, -228.73) * mm});
            skLineSegment(sketch, "E33.0.13.0", {"start": v(-10.16, -222.38) * mm, "end": v(-12.7, -222.38) * mm});
            skLineSegment(sketch, "E33.0.13.1", {"start": v(-12.7, -222.12) * mm, "end": v(-10.16, -222.12) * mm});
            skLineSegment(sketch, "E33.0.13.2", {"start": v(-10.16, -222.12) * mm, "end": v(-10.16, -222.38) * mm});
            skLineSegment(sketch, "E33.0.14.0", {"start": v(-10.16, -216.03) * mm, "end": v(-12.7, -216.03) * mm});
            skLineSegment(sketch, "E33.0.14.1", {"start": v(-12.7, -215.77) * mm, "end": v(-10.16, -215.77) * mm});
            skLineSegment(sketch, "E33.0.14.2", {"start": v(-10.16, -215.77) * mm, "end": v(-10.16, -216.03) * mm});
            skLineSegment(sketch, "E33.0.15.0", {"start": v(-10.16, -209.68) * mm, "end": v(-12.7, -209.68) * mm});
            skLineSegment(sketch, "E33.0.15.1", {"start": v(-12.7, -209.42) * mm, "end": v(-10.16, -209.42) * mm});
            skLineSegment(sketch, "E33.0.15.2", {"start": v(-10.16, -209.42) * mm, "end": v(-10.16, -209.68) * mm});
            skLineSegment(sketch, "E33.0.16.0", {"start": v(-10.16, -203.33) * mm, "end": v(-12.7, -203.33) * mm});
            skLineSegment(sketch, "E33.0.16.1", {"start": v(-12.7, -203.07) * mm, "end": v(-10.16, -203.07) * mm});
            skLineSegment(sketch, "E33.0.16.2", {"start": v(-10.16, -203.07) * mm, "end": v(-10.16, -203.33) * mm});
            skLineSegment(sketch, "E33.0.17.0", {"start": v(-10.16, -196.98) * mm, "end": v(-12.7, -196.98) * mm});
            skLineSegment(sketch, "E33.0.17.1", {"start": v(-12.7, -196.72) * mm, "end": v(-10.16, -196.72) * mm});
            skLineSegment(sketch, "E33.0.17.2", {"start": v(-10.16, -196.72) * mm, "end": v(-10.16, -196.98) * mm});
            skLineSegment(sketch, "E33.0.18.0", {"start": v(-10.16, -190.63) * mm, "end": v(-12.7, -190.63) * mm});
            skLineSegment(sketch, "E33.0.18.1", {"start": v(-12.7, -190.37) * mm, "end": v(-10.16, -190.37) * mm});
            skLineSegment(sketch, "E33.0.18.2", {"start": v(-10.16, -190.37) * mm, "end": v(-10.16, -190.63) * mm});
            skLineSegment(sketch, "E33.0.19.0", {"start": v(-10.16, -184.28) * mm, "end": v(-12.7, -184.28) * mm});
            skLineSegment(sketch, "E33.0.19.1", {"start": v(-12.7, -184.02) * mm, "end": v(-10.16, -184.02) * mm});
            skLineSegment(sketch, "E33.0.19.2", {"start": v(-10.16, -184.02) * mm, "end": v(-10.16, -184.28) * mm});
            skLineSegment(sketch, "E33.0.20.0", {"start": v(-10.16, -177.93) * mm, "end": v(-12.7, -177.93) * mm});
            skLineSegment(sketch, "E33.0.20.1", {"start": v(-12.7, -177.67) * mm, "end": v(-10.16, -177.67) * mm});
            skLineSegment(sketch, "E33.0.20.2", {"start": v(-10.16, -177.67) * mm, "end": v(-10.16, -177.93) * mm});
            skLineSegment(sketch, "E33.0.21.0", {"start": v(-10.16, -171.58) * mm, "end": v(-12.7, -171.58) * mm});
            skLineSegment(sketch, "E33.0.21.1", {"start": v(-12.7, -171.32) * mm, "end": v(-10.16, -171.32) * mm});
            skLineSegment(sketch, "E33.0.21.2", {"start": v(-10.16, -171.32) * mm, "end": v(-10.16, -171.58) * mm});
            skLineSegment(sketch, "E33.0.22.0", {"start": v(-10.16, -165.23) * mm, "end": v(-12.7, -165.23) * mm});
            skLineSegment(sketch, "E33.0.22.1", {"start": v(-12.7, -164.97) * mm, "end": v(-10.16, -164.97) * mm});
            skLineSegment(sketch, "E33.0.22.2", {"start": v(-10.16, -164.97) * mm, "end": v(-10.16, -165.23) * mm});
            skLineSegment(sketch, "E33.0.23.0", {"start": v(-10.16, -158.88) * mm, "end": v(-12.7, -158.88) * mm});
            skLineSegment(sketch, "E33.0.23.1", {"start": v(-12.7, -158.62) * mm, "end": v(-10.16, -158.62) * mm});
            skLineSegment(sketch, "E33.0.23.2", {"start": v(-10.16, -158.62) * mm, "end": v(-10.16, -158.88) * mm});
            skLineSegment(sketch, "E33.0.24.0", {"start": v(-10.16, -152.53) * mm, "end": v(-12.7, -152.53) * mm});
            skLineSegment(sketch, "E33.0.24.1", {"start": v(-12.7, -152.27) * mm, "end": v(-10.16, -152.27) * mm});
            skLineSegment(sketch, "E33.0.24.2", {"start": v(-10.16, -152.27) * mm, "end": v(-10.16, -152.53) * mm});
            skLineSegment(sketch, "E33.0.25.0", {"start": v(-10.16, -146.18) * mm, "end": v(-12.7, -146.18) * mm});
            skLineSegment(sketch, "E33.0.25.1", {"start": v(-12.7, -145.92) * mm, "end": v(-10.16, -145.92) * mm});
            skLineSegment(sketch, "E33.0.25.2", {"start": v(-10.16, -145.92) * mm, "end": v(-10.16, -146.18) * mm});
            skLineSegment(sketch, "E33.0.26.0", {"start": v(-10.16, -139.83) * mm, "end": v(-12.7, -139.83) * mm});
            skLineSegment(sketch, "E33.0.26.1", {"start": v(-12.7, -139.57) * mm, "end": v(-10.16, -139.57) * mm});
            skLineSegment(sketch, "E33.0.26.2", {"start": v(-10.16, -139.57) * mm, "end": v(-10.16, -139.83) * mm});
            skLineSegment(sketch, "E33.0.27.0", {"start": v(-10.16, -133.48) * mm, "end": v(-12.7, -133.48) * mm});
            skLineSegment(sketch, "E33.0.27.1", {"start": v(-12.7, -133.22) * mm, "end": v(-10.16, -133.22) * mm});
            skLineSegment(sketch, "E33.0.27.2", {"start": v(-10.16, -133.22) * mm, "end": v(-10.16, -133.48) * mm});
            skLineSegment(sketch, "E33.0.28.0", {"start": v(-10.16, -127.13) * mm, "end": v(-12.7, -127.13) * mm});
            skLineSegment(sketch, "E33.0.28.1", {"start": v(-12.7, -126.87) * mm, "end": v(-10.16, -126.87) * mm});
            skLineSegment(sketch, "E33.0.28.2", {"start": v(-10.16, -126.87) * mm, "end": v(-10.16, -127.13) * mm});
            skLineSegment(sketch, "E33.0.29.0", {"start": v(-10.16, -120.78) * mm, "end": v(-12.7, -120.78) * mm});
            skLineSegment(sketch, "E33.0.29.1", {"start": v(-12.7, -120.52) * mm, "end": v(-10.16, -120.52) * mm});
            skLineSegment(sketch, "E33.0.29.2", {"start": v(-10.16, -120.52) * mm, "end": v(-10.16, -120.78) * mm});
            skLineSegment(sketch, "E33.0.30.0", {"start": v(-10.16, -114.43) * mm, "end": v(-12.7, -114.43) * mm});
            skLineSegment(sketch, "E33.0.30.1", {"start": v(-12.7, -114.17) * mm, "end": v(-10.16, -114.17) * mm});
            skLineSegment(sketch, "E33.0.30.2", {"start": v(-10.16, -114.17) * mm, "end": v(-10.16, -114.43) * mm});
            skLineSegment(sketch, "E33.0.31.0", {"start": v(-10.16, -108.08) * mm, "end": v(-12.7, -108.08) * mm});
            skLineSegment(sketch, "E33.0.31.1", {"start": v(-12.7, -107.82) * mm, "end": v(-10.16, -107.82) * mm});
            skLineSegment(sketch, "E33.0.31.2", {"start": v(-10.16, -107.82) * mm, "end": v(-10.16, -108.08) * mm});
            skLineSegment(sketch, "E33.0.32.0", {"start": v(-10.16, -101.73) * mm, "end": v(-12.7, -101.73) * mm});
            skLineSegment(sketch, "E33.0.32.1", {"start": v(-12.7, -101.47) * mm, "end": v(-10.16, -101.47) * mm});
            skLineSegment(sketch, "E33.0.32.2", {"start": v(-10.16, -101.47) * mm, "end": v(-10.16, -101.73) * mm});
            skLineSegment(sketch, "E33.0.33.0", {"start": v(-10.16, -95.38) * mm, "end": v(-12.7, -95.38) * mm});
            skLineSegment(sketch, "E33.0.33.1", {"start": v(-12.7, -95.12) * mm, "end": v(-10.16, -95.12) * mm});
            skLineSegment(sketch, "E33.0.33.2", {"start": v(-10.16, -95.12) * mm, "end": v(-10.16, -95.38) * mm});
            skLineSegment(sketch, "E33.0.34.0", {"start": v(-10.16, -89.03) * mm, "end": v(-12.7, -89.03) * mm});
            skLineSegment(sketch, "E33.0.34.1", {"start": v(-12.7, -88.77) * mm, "end": v(-10.16, -88.77) * mm});
            skLineSegment(sketch, "E33.0.34.2", {"start": v(-10.16, -88.77) * mm, "end": v(-10.16, -89.03) * mm});
            skLineSegment(sketch, "E33.0.35.0", {"start": v(-10.16, -82.68) * mm, "end": v(-12.7, -82.68) * mm});
            skLineSegment(sketch, "E33.0.35.1", {"start": v(-12.7, -82.42) * mm, "end": v(-10.16, -82.42) * mm});
            skLineSegment(sketch, "E33.0.35.2", {"start": v(-10.16, -82.42) * mm, "end": v(-10.16, -82.68) * mm});
            skLineSegment(sketch, "E33.0.36.0", {"start": v(-10.16, -76.33) * mm, "end": v(-12.7, -76.33) * mm});
            skLineSegment(sketch, "E33.0.36.1", {"start": v(-12.7, -76.07) * mm, "end": v(-10.16, -76.07) * mm});
            skLineSegment(sketch, "E33.0.36.2", {"start": v(-10.16, -76.07) * mm, "end": v(-10.16, -76.33) * mm});
            skLineSegment(sketch, "E33.0.37.0", {"start": v(-10.16, -69.98) * mm, "end": v(-12.7, -69.98) * mm});
            skLineSegment(sketch, "E33.0.37.1", {"start": v(-12.7, -69.72) * mm, "end": v(-10.16, -69.72) * mm});
            skLineSegment(sketch, "E33.0.37.2", {"start": v(-10.16, -69.72) * mm, "end": v(-10.16, -69.98) * mm});
            skLineSegment(sketch, "E33.0.38.0", {"start": v(-10.16, -63.63) * mm, "end": v(-12.7, -63.63) * mm});
            skLineSegment(sketch, "E33.0.38.1", {"start": v(-12.7, -63.37) * mm, "end": v(-10.16, -63.37) * mm});
            skLineSegment(sketch, "E33.0.38.2", {"start": v(-10.16, -63.37) * mm, "end": v(-10.16, -63.63) * mm});
            skLineSegment(sketch, "E33.0.39.0", {"start": v(-10.16, -57.28) * mm, "end": v(-12.7, -57.28) * mm});
            skLineSegment(sketch, "E33.0.39.1", {"start": v(-12.7, -57.02) * mm, "end": v(-10.16, -57.02) * mm});
            skLineSegment(sketch, "E33.0.39.2", {"start": v(-10.16, -57.02) * mm, "end": v(-10.16, -57.28) * mm});
            skLineSegment(sketch, "E33.0.40.0", {"start": v(-10.16, -50.93) * mm, "end": v(-12.7, -50.93) * mm});
            skLineSegment(sketch, "E33.0.40.1", {"start": v(-12.7, -50.67) * mm, "end": v(-10.16, -50.67) * mm});
            skLineSegment(sketch, "E33.0.40.2", {"start": v(-10.16, -50.67) * mm, "end": v(-10.16, -50.93) * mm});
            skLineSegment(sketch, "E33.0.41.0", {"start": v(-10.16, -44.58) * mm, "end": v(-12.7, -44.58) * mm});
            skLineSegment(sketch, "E33.0.41.1", {"start": v(-12.7, -44.32) * mm, "end": v(-10.16, -44.32) * mm});
            skLineSegment(sketch, "E33.0.41.2", {"start": v(-10.16, -44.32) * mm, "end": v(-10.16, -44.58) * mm});
            skLineSegment(sketch, "E33.0.42.0", {"start": v(-10.16, -38.23) * mm, "end": v(-12.7, -38.23) * mm});
            skLineSegment(sketch, "E33.0.42.1", {"start": v(-12.7, -37.97) * mm, "end": v(-10.16, -37.97) * mm});
            skLineSegment(sketch, "E33.0.42.2", {"start": v(-10.16, -37.97) * mm, "end": v(-10.16, -38.23) * mm});
            skLineSegment(sketch, "E33.0.43.0", {"start": v(-10.16, -31.88) * mm, "end": v(-12.7, -31.88) * mm});
            skLineSegment(sketch, "E33.0.43.1", {"start": v(-12.7, -31.62) * mm, "end": v(-10.16, -31.62) * mm});
            skLineSegment(sketch, "E33.0.43.2", {"start": v(-10.16, -31.62) * mm, "end": v(-10.16, -31.88) * mm});
            skLineSegment(sketch, "E33.0.44.0", {"start": v(-10.16, -25.53) * mm, "end": v(-12.7, -25.53) * mm});
            skLineSegment(sketch, "E33.0.44.1", {"start": v(-12.7, -25.27) * mm, "end": v(-10.16, -25.27) * mm});
            skLineSegment(sketch, "E33.0.44.2", {"start": v(-10.16, -25.27) * mm, "end": v(-10.16, -25.53) * mm});
            skLineSegment(sketch, "E33.0.45.0", {"start": v(-10.16, -19.18) * mm, "end": v(-12.7, -19.18) * mm});
            skLineSegment(sketch, "E33.0.45.1", {"start": v(-12.7, -18.92) * mm, "end": v(-10.16, -18.92) * mm});
            skLineSegment(sketch, "E33.0.45.2", {"start": v(-10.16, -18.92) * mm, "end": v(-10.16, -19.18) * mm});
            skLineSegment(sketch, "E33.0.46.0", {"start": v(-10.16, -12.83) * mm, "end": v(-12.7, -12.83) * mm});
            skLineSegment(sketch, "E33.0.46.1", {"start": v(-12.7, -12.57) * mm, "end": v(-10.16, -12.57) * mm});
            skLineSegment(sketch, "E33.0.46.2", {"start": v(-10.16, -12.57) * mm, "end": v(-10.16, -12.83) * mm});
            skLineSegment(sketch, "E33.0.47.0", {"start": v(-10.16, -6.48) * mm, "end": v(-12.7, -6.48) * mm});
            skLineSegment(sketch, "E33.0.47.1", {"start": v(-12.7, -6.22) * mm, "end": v(-10.16, -6.22) * mm});
            skLineSegment(sketch, "E33.0.47.2", {"start": v(-10.16, -6.22) * mm, "end": v(-10.16, -6.48) * mm});
            skLineSegment(sketch, "E33.direction1", {"start": v(-12.7, -304.93) * mm, "end": v(12.7, -304.93) * mm, "construction": true});
            skLineSegment(sketch, "E33.direction2", {"start": v(-12.7, -304.93) * mm, "end": v(-12.7, -298.58) * mm, "construction": true});
            skLineSegment(sketch, "E34", {"start": v(-12.05, -301.63) * mm, "end": v(-12.05, -301.5) * mm});
            skLineSegment(sketch, "E35", {"start": v(-12.05, -301.5) * mm, "end": v(-12.7, -301.5) * mm});
            skLineSegment(sketch, "E36", {"start": v(-12.7, -301.5) * mm, "end": v(-9.53, -301.5) * mm});
            skLineSegment(sketch, "E37", {"start": v(-9.53, -301.5) * mm, "end": v(-9.53, -301.75) * mm});
            skLineSegment(sketch, "E38", {"start": v(-9.53, -301.75) * mm, "end": v(-12.7, -301.75) * mm});
            skLineSegment(sketch, "E39.trimOffspring", {"start": v(-12.05, -301.75) * mm, "end": v(-12.05, -301.63) * mm});
            skPoint(sketch, "E40.start.orphan", {"position": v(-12.05, -303.21) * mm});
            skLineSegment(sketch, "E41.0.1.0", {"start": v(-9.52, -289.05) * mm, "end": v(-12.7, -289.05) * mm});
            skLineSegment(sketch, "E41.0.1.1", {"start": v(-12.7, -288.8) * mm, "end": v(-9.52, -288.8) * mm});
            skLineSegment(sketch, "E41.0.1.2", {"start": v(-9.53, -288.8) * mm, "end": v(-9.53, -289.05) * mm});
            skLineSegment(sketch, "E41.0.2.0", {"start": v(-9.52, -276.35) * mm, "end": v(-12.7, -276.35) * mm});
            skLineSegment(sketch, "E41.0.2.1", {"start": v(-12.7, -276.1) * mm, "end": v(-9.52, -276.1) * mm});
            skLineSegment(sketch, "E41.0.2.2", {"start": v(-9.53, -276.1) * mm, "end": v(-9.53, -276.35) * mm});
            skLineSegment(sketch, "E41.0.3.0", {"start": v(-9.52, -263.65) * mm, "end": v(-12.7, -263.65) * mm});
            skLineSegment(sketch, "E41.0.3.1", {"start": v(-12.7, -263.4) * mm, "end": v(-9.52, -263.4) * mm});
            skLineSegment(sketch, "E41.0.3.2", {"start": v(-9.53, -263.4) * mm, "end": v(-9.53, -263.65) * mm});
            skLineSegment(sketch, "E41.0.4.0", {"start": v(-9.52, -250.95) * mm, "end": v(-12.7, -250.95) * mm});
            skLineSegment(sketch, "E41.0.4.1", {"start": v(-12.7, -250.7) * mm, "end": v(-9.52, -250.7) * mm});
            skLineSegment(sketch, "E41.0.4.2", {"start": v(-9.53, -250.7) * mm, "end": v(-9.53, -250.95) * mm});
            skLineSegment(sketch, "E41.0.5.0", {"start": v(-9.52, -238.25) * mm, "end": v(-12.7, -238.25) * mm});
            skLineSegment(sketch, "E41.0.5.1", {"start": v(-12.7, -238) * mm, "end": v(-9.52, -238) * mm});
            skLineSegment(sketch, "E41.0.5.2", {"start": v(-9.53, -238) * mm, "end": v(-9.53, -238.25) * mm});
            skLineSegment(sketch, "E41.0.6.0", {"start": v(-9.52, -225.55) * mm, "end": v(-12.7, -225.55) * mm});
            skLineSegment(sketch, "E41.0.6.1", {"start": v(-12.7, -225.3) * mm, "end": v(-9.52, -225.3) * mm});
            skLineSegment(sketch, "E41.0.6.2", {"start": v(-9.53, -225.3) * mm, "end": v(-9.53, -225.55) * mm});
            skLineSegment(sketch, "E41.0.7.0", {"start": v(-9.52, -212.85) * mm, "end": v(-12.7, -212.85) * mm});
            skLineSegment(sketch, "E41.0.7.1", {"start": v(-12.7, -212.6) * mm, "end": v(-9.52, -212.6) * mm});
            skLineSegment(sketch, "E41.0.7.2", {"start": v(-9.53, -212.6) * mm, "end": v(-9.53, -212.85) * mm});
            skLineSegment(sketch, "E41.0.8.0", {"start": v(-9.52, -200.15) * mm, "end": v(-12.7, -200.15) * mm});
            skLineSegment(sketch, "E41.0.8.1", {"start": v(-12.7, -199.9) * mm, "end": v(-9.52, -199.9) * mm});
            skLineSegment(sketch, "E41.0.8.2", {"start": v(-9.53, -199.9) * mm, "end": v(-9.53, -200.15) * mm});
            skLineSegment(sketch, "E41.0.9.0", {"start": v(-9.52, -187.45) * mm, "end": v(-12.7, -187.45) * mm});
            skLineSegment(sketch, "E41.0.9.1", {"start": v(-12.7, -187.2) * mm, "end": v(-9.52, -187.2) * mm});
            skLineSegment(sketch, "E41.0.9.2", {"start": v(-9.53, -187.2) * mm, "end": v(-9.53, -187.45) * mm});
            skLineSegment(sketch, "E41.0.10.0", {"start": v(-9.52, -174.75) * mm, "end": v(-12.7, -174.75) * mm});
            skLineSegment(sketch, "E41.0.10.1", {"start": v(-12.7, -174.5) * mm, "end": v(-9.52, -174.5) * mm});
            skLineSegment(sketch, "E41.0.10.2", {"start": v(-9.53, -174.5) * mm, "end": v(-9.53, -174.75) * mm});
            skLineSegment(sketch, "E41.0.11.0", {"start": v(-9.52, -162.05) * mm, "end": v(-12.7, -162.05) * mm});
            skLineSegment(sketch, "E41.0.11.1", {"start": v(-12.7, -161.8) * mm, "end": v(-9.52, -161.8) * mm});
            skLineSegment(sketch, "E41.0.11.2", {"start": v(-9.53, -161.8) * mm, "end": v(-9.53, -162.05) * mm});
            skLineSegment(sketch, "E41.0.12.0", {"start": v(-9.52, -149.35) * mm, "end": v(-12.7, -149.35) * mm});
            skLineSegment(sketch, "E41.0.12.1", {"start": v(-12.7, -149.1) * mm, "end": v(-9.52, -149.1) * mm});
            skLineSegment(sketch, "E41.0.12.2", {"start": v(-9.53, -149.1) * mm, "end": v(-9.53, -149.35) * mm});
            skLineSegment(sketch, "E41.0.13.0", {"start": v(-9.52, -136.65) * mm, "end": v(-12.7, -136.65) * mm});
            skLineSegment(sketch, "E41.0.13.1", {"start": v(-12.7, -136.4) * mm, "end": v(-9.52, -136.4) * mm});
            skLineSegment(sketch, "E41.0.13.2", {"start": v(-9.53, -136.4) * mm, "end": v(-9.53, -136.65) * mm});
            skLineSegment(sketch, "E41.0.14.0", {"start": v(-9.52, -123.95) * mm, "end": v(-12.7, -123.95) * mm});
            skLineSegment(sketch, "E41.0.14.1", {"start": v(-12.7, -123.7) * mm, "end": v(-9.52, -123.7) * mm});
            skLineSegment(sketch, "E41.0.14.2", {"start": v(-9.53, -123.7) * mm, "end": v(-9.53, -123.95) * mm});
            skLineSegment(sketch, "E41.0.15.0", {"start": v(-9.52, -111.25) * mm, "end": v(-12.7, -111.25) * mm});
            skLineSegment(sketch, "E41.0.15.1", {"start": v(-12.7, -111) * mm, "end": v(-9.52, -111) * mm});
            skLineSegment(sketch, "E41.0.15.2", {"start": v(-9.53, -111) * mm, "end": v(-9.53, -111.25) * mm});
            skLineSegment(sketch, "E41.0.16.0", {"start": v(-9.52, -98.55) * mm, "end": v(-12.7, -98.55) * mm});
            skLineSegment(sketch, "E41.0.16.1", {"start": v(-12.7, -98.3) * mm, "end": v(-9.52, -98.3) * mm});
            skLineSegment(sketch, "E41.0.16.2", {"start": v(-9.53, -98.3) * mm, "end": v(-9.53, -98.55) * mm});
            skLineSegment(sketch, "E41.0.17.0", {"start": v(-9.52, -85.85) * mm, "end": v(-12.7, -85.85) * mm});
            skLineSegment(sketch, "E41.0.17.1", {"start": v(-12.7, -85.6) * mm, "end": v(-9.52, -85.6) * mm});
            skLineSegment(sketch, "E41.0.17.2", {"start": v(-9.53, -85.6) * mm, "end": v(-9.53, -85.85) * mm});
            skLineSegment(sketch, "E41.0.18.0", {"start": v(-9.52, -73.15) * mm, "end": v(-12.7, -73.15) * mm});
            skLineSegment(sketch, "E41.0.18.1", {"start": v(-12.7, -72.9) * mm, "end": v(-9.52, -72.9) * mm});
            skLineSegment(sketch, "E41.0.18.2", {"start": v(-9.53, -72.9) * mm, "end": v(-9.53, -73.15) * mm});
            skLineSegment(sketch, "E41.0.19.0", {"start": v(-9.52, -60.45) * mm, "end": v(-12.7, -60.45) * mm});
            skLineSegment(sketch, "E41.0.19.1", {"start": v(-12.7, -60.2) * mm, "end": v(-9.52, -60.2) * mm});
            skLineSegment(sketch, "E41.0.19.2", {"start": v(-9.53, -60.2) * mm, "end": v(-9.53, -60.45) * mm});
            skLineSegment(sketch, "E41.0.20.0", {"start": v(-9.52, -47.75) * mm, "end": v(-12.7, -47.75) * mm});
            skLineSegment(sketch, "E41.0.20.1", {"start": v(-12.7, -47.5) * mm, "end": v(-9.52, -47.5) * mm});
            skLineSegment(sketch, "E41.0.20.2", {"start": v(-9.53, -47.5) * mm, "end": v(-9.53, -47.75) * mm});
            skLineSegment(sketch, "E41.0.21.0", {"start": v(-9.52, -35.05) * mm, "end": v(-12.7, -35.05) * mm});
            skLineSegment(sketch, "E41.0.21.1", {"start": v(-12.7, -34.8) * mm, "end": v(-9.52, -34.8) * mm});
            skLineSegment(sketch, "E41.0.21.2", {"start": v(-9.53, -34.8) * mm, "end": v(-9.53, -35.05) * mm});
            skLineSegment(sketch, "E41.0.22.0", {"start": v(-9.52, -22.35) * mm, "end": v(-12.7, -22.35) * mm});
            skLineSegment(sketch, "E41.0.22.1", {"start": v(-12.7, -22.1) * mm, "end": v(-9.52, -22.1) * mm});
            skLineSegment(sketch, "E41.0.22.2", {"start": v(-9.53, -22.1) * mm, "end": v(-9.53, -22.35) * mm});
            skLineSegment(sketch, "E41.0.23.0", {"start": v(-9.52, -9.65) * mm, "end": v(-12.7, -9.65) * mm});
            skLineSegment(sketch, "E41.0.23.1", {"start": v(-12.7, -9.4) * mm, "end": v(-9.52, -9.4) * mm});
            skLineSegment(sketch, "E41.0.23.2", {"start": v(-9.53, -9.4) * mm, "end": v(-9.53, -9.65) * mm});
            skLineSegment(sketch, "E41.direction1", {"start": v(-12.7, -301.75) * mm, "end": v(12.7, -301.75) * mm, "construction": true});
            skLineSegment(sketch, "E41.direction2", {"start": v(-12.7, -301.75) * mm, "end": v(-12.7, -289.05) * mm, "construction": true});
            skPoint(sketch, "E42.endSnap0", {"position": v(-12.7, -295.4) * mm});
            skLineSegment(sketch, "E43", {"start": v(-9.07, -295.4) * mm, "end": v(-9.07, -295.28) * mm});
            skLineSegment(sketch, "E44", {"start": v(-9.07, -295.4) * mm, "end": v(-9.07, -295.53) * mm});
            skLineSegment(sketch, "E45", {"start": v(-9.07, -295.53) * mm, "end": v(-12.7, -295.53) * mm});
            skLineSegment(sketch, "E46", {"start": v(-9.07, -295.28) * mm, "end": v(-12.7, -295.28) * mm});
            skPoint(sketch, "E42.start.orphan", {"position": v(-12.7, -295.4) * mm});
            skLineSegment(sketch, "E47.0.1.0", {"start": v(-9.07, -270.13) * mm, "end": v(-12.7, -270.13) * mm});
            skLineSegment(sketch, "E47.0.1.1", {"start": v(-9.07, -269.88) * mm, "end": v(-12.7, -269.88) * mm});
            skLineSegment(sketch, "E47.0.1.2", {"start": v(-9.07, -270) * mm, "end": v(-9.07, -270.13) * mm});
            skLineSegment(sketch, "E47.0.1.3", {"start": v(-9.07, -270) * mm, "end": v(-9.07, -269.88) * mm});
            skLineSegment(sketch, "E47.0.2.0", {"start": v(-9.07, -244.73) * mm, "end": v(-12.7, -244.73) * mm});
            skLineSegment(sketch, "E47.0.2.1", {"start": v(-9.07, -244.48) * mm, "end": v(-12.7, -244.48) * mm});
            skLineSegment(sketch, "E47.0.2.2", {"start": v(-9.07, -244.6) * mm, "end": v(-9.07, -244.73) * mm});
            skLineSegment(sketch, "E47.0.2.3", {"start": v(-9.07, -244.6) * mm, "end": v(-9.07, -244.48) * mm});
            skLineSegment(sketch, "E47.0.3.0", {"start": v(-9.07, -219.33) * mm, "end": v(-12.7, -219.33) * mm});
            skLineSegment(sketch, "E47.0.3.1", {"start": v(-9.07, -219.08) * mm, "end": v(-12.7, -219.08) * mm});
            skLineSegment(sketch, "E47.0.3.2", {"start": v(-9.07, -219.2) * mm, "end": v(-9.07, -219.33) * mm});
            skLineSegment(sketch, "E47.0.3.3", {"start": v(-9.07, -219.2) * mm, "end": v(-9.07, -219.08) * mm});
            skLineSegment(sketch, "E47.0.4.0", {"start": v(-9.07, -193.93) * mm, "end": v(-12.7, -193.93) * mm});
            skLineSegment(sketch, "E47.0.4.1", {"start": v(-9.07, -193.68) * mm, "end": v(-12.7, -193.68) * mm});
            skLineSegment(sketch, "E47.0.4.2", {"start": v(-9.07, -193.8) * mm, "end": v(-9.07, -193.93) * mm});
            skLineSegment(sketch, "E47.0.4.3", {"start": v(-9.07, -193.8) * mm, "end": v(-9.07, -193.68) * mm});
            skLineSegment(sketch, "E47.0.5.0", {"start": v(-9.07, -168.53) * mm, "end": v(-12.7, -168.53) * mm});
            skLineSegment(sketch, "E47.0.5.1", {"start": v(-9.07, -168.28) * mm, "end": v(-12.7, -168.28) * mm});
            skLineSegment(sketch, "E47.0.5.2", {"start": v(-9.07, -168.4) * mm, "end": v(-9.07, -168.53) * mm});
            skLineSegment(sketch, "E47.0.5.3", {"start": v(-9.07, -168.4) * mm, "end": v(-9.07, -168.28) * mm});
            skLineSegment(sketch, "E47.0.6.0", {"start": v(-9.07, -143.13) * mm, "end": v(-12.7, -143.13) * mm});
            skLineSegment(sketch, "E47.0.6.1", {"start": v(-9.07, -142.88) * mm, "end": v(-12.7, -142.88) * mm});
            skLineSegment(sketch, "E47.0.6.2", {"start": v(-9.07, -143) * mm, "end": v(-9.07, -143.13) * mm});
            skLineSegment(sketch, "E47.0.6.3", {"start": v(-9.07, -143) * mm, "end": v(-9.07, -142.88) * mm});
            skLineSegment(sketch, "E47.0.7.0", {"start": v(-9.07, -117.73) * mm, "end": v(-12.7, -117.73) * mm});
            skLineSegment(sketch, "E47.0.7.1", {"start": v(-9.07, -117.48) * mm, "end": v(-12.7, -117.48) * mm});
            skLineSegment(sketch, "E47.0.7.2", {"start": v(-9.07, -117.6) * mm, "end": v(-9.07, -117.73) * mm});
            skLineSegment(sketch, "E47.0.7.3", {"start": v(-9.07, -117.6) * mm, "end": v(-9.07, -117.48) * mm});
            skLineSegment(sketch, "E47.0.8.0", {"start": v(-9.07, -92.33) * mm, "end": v(-12.7, -92.33) * mm});
            skLineSegment(sketch, "E47.0.8.1", {"start": v(-9.07, -92.08) * mm, "end": v(-12.7, -92.08) * mm});
            skLineSegment(sketch, "E47.0.8.2", {"start": v(-9.07, -92.2) * mm, "end": v(-9.07, -92.33) * mm});
            skLineSegment(sketch, "E47.0.8.3", {"start": v(-9.07, -92.2) * mm, "end": v(-9.07, -92.08) * mm});
            skLineSegment(sketch, "E47.0.9.0", {"start": v(-9.07, -66.93) * mm, "end": v(-12.7, -66.93) * mm});
            skLineSegment(sketch, "E47.0.9.1", {"start": v(-9.07, -66.68) * mm, "end": v(-12.7, -66.68) * mm});
            skLineSegment(sketch, "E47.0.9.2", {"start": v(-9.07, -66.8) * mm, "end": v(-9.07, -66.93) * mm});
            skLineSegment(sketch, "E47.0.9.3", {"start": v(-9.07, -66.8) * mm, "end": v(-9.07, -66.68) * mm});
            skLineSegment(sketch, "E47.0.10.0", {"start": v(-9.07, -41.53) * mm, "end": v(-12.7, -41.53) * mm});
            skLineSegment(sketch, "E47.0.10.1", {"start": v(-9.07, -41.28) * mm, "end": v(-12.7, -41.28) * mm});
            skLineSegment(sketch, "E47.0.10.2", {"start": v(-9.07, -41.4) * mm, "end": v(-9.07, -41.53) * mm});
            skLineSegment(sketch, "E47.0.10.3", {"start": v(-9.07, -41.4) * mm, "end": v(-9.07, -41.28) * mm});
            skLineSegment(sketch, "E47.0.11.0", {"start": v(-9.07, -16.13) * mm, "end": v(-12.7, -16.13) * mm});
            skLineSegment(sketch, "E47.0.11.1", {"start": v(-9.07, -15.88) * mm, "end": v(-12.7, -15.88) * mm});
            skLineSegment(sketch, "E47.0.11.2", {"start": v(-9.07, -16) * mm, "end": v(-9.07, -16.13) * mm});
            skLineSegment(sketch, "E47.0.11.3", {"start": v(-9.07, -16) * mm, "end": v(-9.07, -15.88) * mm});
            skLineSegment(sketch, "E47.direction1", {"start": v(-12.7, -295.53) * mm, "end": v(-38.1, -295.53) * mm, "construction": true});
            skLineSegment(sketch, "E47.direction2", {"start": v(-12.7, -295.53) * mm, "end": v(-12.7, -270.13) * mm, "construction": true});
            skSolve(sketch);
        }
        {
            var Q0;
            {var subQ1=sQuery(id+"F2.wireOp",EDGE,"E16.0.0.12");Q0=makeQuery(id+"F2.imprint","IMPRINT",FACE,{"disambiguationData":[TD([[makeQuery(id+"F2.imprint","IMPRINT",EDGE,{"derivedFrom":subQ1}),-1.0]])]});}
            var Q1;
            {var subQ1=sQuery(id+"F2.wireOp",EDGE,"E27.0.95.0");Q1=makeQuery(id+"F2.imprint","IMPRINT",FACE,{"disambiguationData":[TD([[makeQuery(id+"F2.imprint","IMPRINT",EDGE,{"derivedFrom":subQ1}),-1.0]])]});}
            var Q2;
            {var subQ0=sQuery(id+"F2.wireOp",EDGE,"E33.0.47.0");Q2=makeQuery(id+"F2.imprint","IMPRINT",FACE,{"disambiguationData":[TD([[makeQuery(id+"F2.imprint","IMPRINT",EDGE,{"derivedFrom":subQ0}),-1.0]])]});}
            var Q3;
            {var subQ1=sQuery(id+"F2.wireOp",EDGE,"E27.0.94.0");Q3=makeQuery(id+"F2.imprint","IMPRINT",FACE,{"disambiguationData":[TD([[makeQuery(id+"F2.imprint","IMPRINT",EDGE,{"derivedFrom":subQ1}),-1.0]])]});}
            var Q4;
            {var subQ0=sQuery(id+"F2.wireOp",EDGE,"E41.0.23.0");Q4=makeQuery(id+"F2.imprint","IMPRINT",FACE,{"disambiguationData":[TD([[makeQuery(id+"F2.imprint","IMPRINT",EDGE,{"derivedFrom":subQ0}),-1.0]])]});}
            var Q5;
            {var subQ0=sQuery(id+"F2.wireOp",EDGE,"E27.0.93.0");Q5=makeQuery(id+"F2.imprint","IMPRINT",FACE,{"disambiguationData":[TD([[makeQuery(id+"F2.imprint","IMPRINT",EDGE,{"derivedFrom":subQ0}),-1.0]])]});}
            var Q6;
            {var subQ0=sQuery(id+"F2.wireOp",EDGE,"E33.0.46.0");Q6=makeQuery(id+"F2.imprint","IMPRINT",FACE,{"disambiguationData":[TD([[makeQuery(id+"F2.imprint","IMPRINT",EDGE,{"derivedFrom":subQ0}),-1.0]])]});}
            var Q7;
            {var subQ0=sQuery(id+"F2.wireOp",EDGE,"E27.0.92.0");Q7=makeQuery(id+"F2.imprint","IMPRINT",FACE,{"disambiguationData":[TD([[makeQuery(id+"F2.imprint","IMPRINT",EDGE,{"derivedFrom":subQ0}),-1.0]])]});}
            var Q8;
            {var subQ1=sQuery(id+"F2.wireOp",EDGE,"E47.0.11.0");Q8=makeQuery(id+"F2.imprint","IMPRINT",FACE,{"disambiguationData":[TD([[makeQuery(id+"F2.imprint","IMPRINT",EDGE,{"derivedFrom":subQ1}),-1.0]])]});}
            var Q9;
            {var subQ1=sQuery(id+"F2.wireOp",EDGE,"E27.0.91.0");Q9=makeQuery(id+"F2.imprint","IMPRINT",FACE,{"disambiguationData":[TD([[makeQuery(id+"F2.imprint","IMPRINT",EDGE,{"derivedFrom":subQ1}),-1.0]])]});}
            var Q10;
            {var subQ0=sQuery(id+"F2.wireOp",EDGE,"E33.0.45.0");Q10=makeQuery(id+"F2.imprint","IMPRINT",FACE,{"disambiguationData":[TD([[makeQuery(id+"F2.imprint","IMPRINT",EDGE,{"derivedFrom":subQ0}),-1.0]])]});}
            var Q11;
            {var subQ1=sQuery(id+"F2.wireOp",EDGE,"E27.0.90.0");Q11=makeQuery(id+"F2.imprint","IMPRINT",FACE,{"disambiguationData":[TD([[makeQuery(id+"F2.imprint","IMPRINT",EDGE,{"derivedFrom":subQ1}),-1.0]])]});}
            var Q12;
            {var subQ0=sQuery(id+"F2.wireOp",EDGE,"E41.0.22.0");Q12=makeQuery(id+"F2.imprint","IMPRINT",FACE,{"disambiguationData":[TD([[makeQuery(id+"F2.imprint","IMPRINT",EDGE,{"derivedFrom":subQ0}),-1.0]])]});}
            var Q13;
            {var subQ1=sQuery(id+"F2.wireOp",EDGE,"E27.0.89.0");Q13=makeQuery(id+"F2.imprint","IMPRINT",FACE,{"disambiguationData":[TD([[makeQuery(id+"F2.imprint","IMPRINT",EDGE,{"derivedFrom":subQ1}),-1.0]])]});}
            var Q14;
            {var subQ0=sQuery(id+"F2.wireOp",EDGE,"E33.0.44.0");Q14=makeQuery(id+"F2.imprint","IMPRINT",FACE,{"disambiguationData":[TD([[makeQuery(id+"F2.imprint","IMPRINT",EDGE,{"derivedFrom":subQ0}),-1.0]])]});}
            var Q15;
            {var subQ1=sQuery(id+"F2.wireOp",EDGE,"E27.0.88.0");Q15=makeQuery(id+"F2.imprint","IMPRINT",FACE,{"disambiguationData":[TD([[makeQuery(id+"F2.imprint","IMPRINT",EDGE,{"derivedFrom":subQ1}),-1.0]])]});}
            var Q16;
            {var subQ1=sQuery(id+"F2.wireOp",EDGE,"E15.0.11.0");Q16=makeQuery(id+"F2.imprint","IMPRINT",FACE,{"disambiguationData":[TD([[makeQuery(id+"F2.imprint","IMPRINT",EDGE,{"derivedFrom":subQ1}),-1.0]])]});}
            var Q17;
            {var subQ1=sQuery(id+"F2.wireOp",EDGE,"E27.0.87.0");Q17=makeQuery(id+"F2.imprint","IMPRINT",FACE,{"disambiguationData":[TD([[makeQuery(id+"F2.imprint","IMPRINT",EDGE,{"derivedFrom":subQ1}),-1.0]])]});}
            var Q18;
            {var subQ0=sQuery(id+"F2.wireOp",EDGE,"E33.0.43.0");Q18=makeQuery(id+"F2.imprint","IMPRINT",FACE,{"disambiguationData":[TD([[makeQuery(id+"F2.imprint","IMPRINT",EDGE,{"derivedFrom":subQ0}),-1.0]])]});}
            var Q19;
            {var subQ1=sQuery(id+"F2.wireOp",EDGE,"E27.0.86.0");Q19=makeQuery(id+"F2.imprint","IMPRINT",FACE,{"disambiguationData":[TD([[makeQuery(id+"F2.imprint","IMPRINT",EDGE,{"derivedFrom":subQ1}),-1.0]])]});}
            var Q20;
            {var subQ0=sQuery(id+"F2.wireOp",EDGE,"E41.0.21.0");Q20=makeQuery(id+"F2.imprint","IMPRINT",FACE,{"disambiguationData":[TD([[makeQuery(id+"F2.imprint","IMPRINT",EDGE,{"derivedFrom":subQ0}),-1.0]])]});}
            var Q21;
            {var subQ1=sQuery(id+"F2.wireOp",EDGE,"E27.0.85.0");Q21=makeQuery(id+"F2.imprint","IMPRINT",FACE,{"disambiguationData":[TD([[makeQuery(id+"F2.imprint","IMPRINT",EDGE,{"derivedFrom":subQ1}),-1.0]])]});}
            var Q22;
            {var subQ0=sQuery(id+"F2.wireOp",EDGE,"E33.0.42.0");Q22=makeQuery(id+"F2.imprint","IMPRINT",FACE,{"disambiguationData":[TD([[makeQuery(id+"F2.imprint","IMPRINT",EDGE,{"derivedFrom":subQ0}),-1.0]])]});}
            var Q23;
            {var subQ1=sQuery(id+"F2.wireOp",EDGE,"E27.0.84.0");Q23=makeQuery(id+"F2.imprint","IMPRINT",FACE,{"disambiguationData":[TD([[makeQuery(id+"F2.imprint","IMPRINT",EDGE,{"derivedFrom":subQ1}),-1.0]])]});}
            var Q24;
            {var subQ1=sQuery(id+"F2.wireOp",EDGE,"E47.0.10.0");Q24=makeQuery(id+"F2.imprint","IMPRINT",FACE,{"disambiguationData":[TD([[makeQuery(id+"F2.imprint","IMPRINT",EDGE,{"derivedFrom":subQ1}),-1.0]])]});}
            var Q25;
            {var subQ1=sQuery(id+"F2.wireOp",EDGE,"E27.0.83.0");Q25=makeQuery(id+"F2.imprint","IMPRINT",FACE,{"disambiguationData":[TD([[makeQuery(id+"F2.imprint","IMPRINT",EDGE,{"derivedFrom":subQ1}),-1.0]])]});}
            var Q26;
            {var subQ0=sQuery(id+"F2.wireOp",EDGE,"E33.0.41.0");Q26=makeQuery(id+"F2.imprint","IMPRINT",FACE,{"disambiguationData":[TD([[makeQuery(id+"F2.imprint","IMPRINT",EDGE,{"derivedFrom":subQ0}),-1.0]])]});}
            var Q27;
            {var subQ0=sQuery(id+"F2.wireOp",EDGE,"E27.0.82.0");Q27=makeQuery(id+"F2.imprint","IMPRINT",FACE,{"disambiguationData":[TD([[makeQuery(id+"F2.imprint","IMPRINT",EDGE,{"derivedFrom":subQ0}),-1.0]])]});}
            var Q28;
            {var subQ0=sQuery(id+"F2.wireOp",EDGE,"E41.0.20.0");Q28=makeQuery(id+"F2.imprint","IMPRINT",FACE,{"disambiguationData":[TD([[makeQuery(id+"F2.imprint","IMPRINT",EDGE,{"derivedFrom":subQ0}),-1.0]])]});}
            var Q29;
            {var subQ1=sQuery(id+"F2.wireOp",EDGE,"E27.0.81.0");Q29=makeQuery(id+"F2.imprint","IMPRINT",FACE,{"disambiguationData":[TD([[makeQuery(id+"F2.imprint","IMPRINT",EDGE,{"derivedFrom":subQ1}),-1.0]])]});}
            var Q30;
            {var subQ0=sQuery(id+"F2.wireOp",EDGE,"E33.0.40.0");Q30=makeQuery(id+"F2.imprint","IMPRINT",FACE,{"disambiguationData":[TD([[makeQuery(id+"F2.imprint","IMPRINT",EDGE,{"derivedFrom":subQ0}),-1.0]])]});}
            var Q31;
            {var subQ1=sQuery(id+"F2.wireOp",EDGE,"E27.0.80.0");Q31=makeQuery(id+"F2.imprint","IMPRINT",FACE,{"disambiguationData":[TD([[makeQuery(id+"F2.imprint","IMPRINT",EDGE,{"derivedFrom":subQ1}),-1.0]])]});}
            var Q32;
            {var subQ1=sQuery(id+"F2.wireOp",EDGE,"E15.0.10.0");Q32=makeQuery(id+"F2.imprint","IMPRINT",FACE,{"disambiguationData":[TD([[makeQuery(id+"F2.imprint","IMPRINT",EDGE,{"derivedFrom":subQ1}),-1.0]])]});}
            var Q33;
            {var subQ1=sQuery(id+"F2.wireOp",EDGE,"E27.0.79.0");Q33=makeQuery(id+"F2.imprint","IMPRINT",FACE,{"disambiguationData":[TD([[makeQuery(id+"F2.imprint","IMPRINT",EDGE,{"derivedFrom":subQ1}),-1.0]])]});}
            var Q34;
            {var subQ0=sQuery(id+"F2.wireOp",EDGE,"E33.0.39.0");Q34=makeQuery(id+"F2.imprint","IMPRINT",FACE,{"disambiguationData":[TD([[makeQuery(id+"F2.imprint","IMPRINT",EDGE,{"derivedFrom":subQ0}),-1.0]])]});}
            var Q35;
            {var subQ1=sQuery(id+"F2.wireOp",EDGE,"E27.0.78.0");Q35=makeQuery(id+"F2.imprint","IMPRINT",FACE,{"disambiguationData":[TD([[makeQuery(id+"F2.imprint","IMPRINT",EDGE,{"derivedFrom":subQ1}),-1.0]])]});}
            var Q36;
            {var subQ0=sQuery(id+"F2.wireOp",EDGE,"E41.0.19.0");Q36=makeQuery(id+"F2.imprint","IMPRINT",FACE,{"disambiguationData":[TD([[makeQuery(id+"F2.imprint","IMPRINT",EDGE,{"derivedFrom":subQ0}),-1.0]])]});}
            var Q37;
            {var subQ0=sQuery(id+"F2.wireOp",EDGE,"E27.0.77.0");Q37=makeQuery(id+"F2.imprint","IMPRINT",FACE,{"disambiguationData":[TD([[makeQuery(id+"F2.imprint","IMPRINT",EDGE,{"derivedFrom":subQ0}),-1.0]])]});}
            var Q38;
            {var subQ0=sQuery(id+"F2.wireOp",EDGE,"E33.0.38.0");Q38=makeQuery(id+"F2.imprint","IMPRINT",FACE,{"disambiguationData":[TD([[makeQuery(id+"F2.imprint","IMPRINT",EDGE,{"derivedFrom":subQ0}),-1.0]])]});}
            var Q39;
            {var subQ1=sQuery(id+"F2.wireOp",EDGE,"E27.0.76.0");Q39=makeQuery(id+"F2.imprint","IMPRINT",FACE,{"disambiguationData":[TD([[makeQuery(id+"F2.imprint","IMPRINT",EDGE,{"derivedFrom":subQ1}),-1.0]])]});}
            var Q40;
            {var subQ1=sQuery(id+"F2.wireOp",EDGE,"E47.0.9.0");Q40=makeQuery(id+"F2.imprint","IMPRINT",FACE,{"disambiguationData":[TD([[makeQuery(id+"F2.imprint","IMPRINT",EDGE,{"derivedFrom":subQ1}),-1.0]])]});}
            var Q41;
            {var subQ1=sQuery(id+"F2.wireOp",EDGE,"E27.0.75.0");Q41=makeQuery(id+"F2.imprint","IMPRINT",FACE,{"disambiguationData":[TD([[makeQuery(id+"F2.imprint","IMPRINT",EDGE,{"derivedFrom":subQ1}),-1.0]])]});}
            var Q42;
            {var subQ0=sQuery(id+"F2.wireOp",EDGE,"E33.0.37.0");Q42=makeQuery(id+"F2.imprint","IMPRINT",FACE,{"disambiguationData":[TD([[makeQuery(id+"F2.imprint","IMPRINT",EDGE,{"derivedFrom":subQ0}),-1.0]])]});}
            var Q43;
            {var subQ1=sQuery(id+"F2.wireOp",EDGE,"E27.0.74.0");Q43=makeQuery(id+"F2.imprint","IMPRINT",FACE,{"disambiguationData":[TD([[makeQuery(id+"F2.imprint","IMPRINT",EDGE,{"derivedFrom":subQ1}),-1.0]])]});}
            var Q44;
            {var subQ0=sQuery(id+"F2.wireOp",EDGE,"E41.0.18.0");Q44=makeQuery(id+"F2.imprint","IMPRINT",FACE,{"disambiguationData":[TD([[makeQuery(id+"F2.imprint","IMPRINT",EDGE,{"derivedFrom":subQ0}),-1.0]])]});}
            var Q45;
            {var subQ1=sQuery(id+"F2.wireOp",EDGE,"E27.0.73.0");Q45=makeQuery(id+"F2.imprint","IMPRINT",FACE,{"disambiguationData":[TD([[makeQuery(id+"F2.imprint","IMPRINT",EDGE,{"derivedFrom":subQ1}),-1.0]])]});}
            var Q46;
            {var subQ0=sQuery(id+"F2.wireOp",EDGE,"E33.0.36.0");Q46=makeQuery(id+"F2.imprint","IMPRINT",FACE,{"disambiguationData":[TD([[makeQuery(id+"F2.imprint","IMPRINT",EDGE,{"derivedFrom":subQ0}),-1.0]])]});}
            var Q47;
            {var subQ1=sQuery(id+"F2.wireOp",EDGE,"E27.0.72.0");Q47=makeQuery(id+"F2.imprint","IMPRINT",FACE,{"disambiguationData":[TD([[makeQuery(id+"F2.imprint","IMPRINT",EDGE,{"derivedFrom":subQ1}),-1.0]])]});}
            var Q48;
            {var subQ1=sQuery(id+"F2.wireOp",EDGE,"E15.0.9.0");Q48=makeQuery(id+"F2.imprint","IMPRINT",FACE,{"disambiguationData":[TD([[makeQuery(id+"F2.imprint","IMPRINT",EDGE,{"derivedFrom":subQ1}),-1.0]])]});}
            var Q49;
            {var subQ1=sQuery(id+"F2.wireOp",EDGE,"E27.0.71.0");Q49=makeQuery(id+"F2.imprint","IMPRINT",FACE,{"disambiguationData":[TD([[makeQuery(id+"F2.imprint","IMPRINT",EDGE,{"derivedFrom":subQ1}),-1.0]])]});}
            var Q50;
            {var subQ0=sQuery(id+"F2.wireOp",EDGE,"E33.0.35.0");Q50=makeQuery(id+"F2.imprint","IMPRINT",FACE,{"disambiguationData":[TD([[makeQuery(id+"F2.imprint","IMPRINT",EDGE,{"derivedFrom":subQ0}),-1.0]])]});}
            var Q51;
            {var subQ1=sQuery(id+"F2.wireOp",EDGE,"E27.0.70.0");Q51=makeQuery(id+"F2.imprint","IMPRINT",FACE,{"disambiguationData":[TD([[makeQuery(id+"F2.imprint","IMPRINT",EDGE,{"derivedFrom":subQ1}),-1.0]])]});}
            var Q52;
            {var subQ0=sQuery(id+"F2.wireOp",EDGE,"E41.0.17.0");Q52=makeQuery(id+"F2.imprint","IMPRINT",FACE,{"disambiguationData":[TD([[makeQuery(id+"F2.imprint","IMPRINT",EDGE,{"derivedFrom":subQ0}),-1.0]])]});}
            var Q53;
            {var subQ1=sQuery(id+"F2.wireOp",EDGE,"E27.0.69.0");Q53=makeQuery(id+"F2.imprint","IMPRINT",FACE,{"disambiguationData":[TD([[makeQuery(id+"F2.imprint","IMPRINT",EDGE,{"derivedFrom":subQ1}),-1.0]])]});}
            var Q54;
            {var subQ0=sQuery(id+"F2.wireOp",EDGE,"E33.0.34.0");Q54=makeQuery(id+"F2.imprint","IMPRINT",FACE,{"disambiguationData":[TD([[makeQuery(id+"F2.imprint","IMPRINT",EDGE,{"derivedFrom":subQ0}),-1.0]])]});}
            var Q55;
            {var subQ1=sQuery(id+"F2.wireOp",EDGE,"E27.0.68.0");Q55=makeQuery(id+"F2.imprint","IMPRINT",FACE,{"disambiguationData":[TD([[makeQuery(id+"F2.imprint","IMPRINT",EDGE,{"derivedFrom":subQ1}),-1.0]])]});}
            var Q56;
            {var subQ1=sQuery(id+"F2.wireOp",EDGE,"E47.0.8.0");Q56=makeQuery(id+"F2.imprint","IMPRINT",FACE,{"disambiguationData":[TD([[makeQuery(id+"F2.imprint","IMPRINT",EDGE,{"derivedFrom":subQ1}),-1.0]])]});}
            var Q57;
            {var subQ1=sQuery(id+"F2.wireOp",EDGE,"E27.0.67.0");Q57=makeQuery(id+"F2.imprint","IMPRINT",FACE,{"disambiguationData":[TD([[makeQuery(id+"F2.imprint","IMPRINT",EDGE,{"derivedFrom":subQ1}),-1.0]])]});}
            var Q58;
            {var subQ0=sQuery(id+"F2.wireOp",EDGE,"E33.0.33.0");Q58=makeQuery(id+"F2.imprint","IMPRINT",FACE,{"disambiguationData":[TD([[makeQuery(id+"F2.imprint","IMPRINT",EDGE,{"derivedFrom":subQ0}),-1.0]])]});}
            var Q59;
            {var subQ1=sQuery(id+"F2.wireOp",EDGE,"E27.0.66.0");Q59=makeQuery(id+"F2.imprint","IMPRINT",FACE,{"disambiguationData":[TD([[makeQuery(id+"F2.imprint","IMPRINT",EDGE,{"derivedFrom":subQ1}),-1.0]])]});}
            var Q60;
            {var subQ0=sQuery(id+"F2.wireOp",EDGE,"E41.0.16.0");Q60=makeQuery(id+"F2.imprint","IMPRINT",FACE,{"disambiguationData":[TD([[makeQuery(id+"F2.imprint","IMPRINT",EDGE,{"derivedFrom":subQ0}),-1.0]])]});}
            var Q61;
            {var subQ1=sQuery(id+"F2.wireOp",EDGE,"E27.0.65.0");Q61=makeQuery(id+"F2.imprint","IMPRINT",FACE,{"disambiguationData":[TD([[makeQuery(id+"F2.imprint","IMPRINT",EDGE,{"derivedFrom":subQ1}),-1.0]])]});}
            var Q62;
            {var subQ0=sQuery(id+"F2.wireOp",EDGE,"E33.0.32.0");Q62=makeQuery(id+"F2.imprint","IMPRINT",FACE,{"disambiguationData":[TD([[makeQuery(id+"F2.imprint","IMPRINT",EDGE,{"derivedFrom":subQ0}),-1.0]])]});}
            var Q63;
            {var subQ1=sQuery(id+"F2.wireOp",EDGE,"E27.0.64.0");Q63=makeQuery(id+"F2.imprint","IMPRINT",FACE,{"disambiguationData":[TD([[makeQuery(id+"F2.imprint","IMPRINT",EDGE,{"derivedFrom":subQ1}),-1.0]])]});}
            var Q64;
            {var subQ1=sQuery(id+"F2.wireOp",EDGE,"E15.0.8.0");Q64=makeQuery(id+"F2.imprint","IMPRINT",FACE,{"disambiguationData":[TD([[makeQuery(id+"F2.imprint","IMPRINT",EDGE,{"derivedFrom":subQ1}),-1.0]])]});}
            var Q65;
            {var subQ1=sQuery(id+"F2.wireOp",EDGE,"E27.0.63.0");Q65=makeQuery(id+"F2.imprint","IMPRINT",FACE,{"disambiguationData":[TD([[makeQuery(id+"F2.imprint","IMPRINT",EDGE,{"derivedFrom":subQ1}),-1.0]])]});}
            var Q66;
            {var subQ0=sQuery(id+"F2.wireOp",EDGE,"E33.0.31.0");Q66=makeQuery(id+"F2.imprint","IMPRINT",FACE,{"disambiguationData":[TD([[makeQuery(id+"F2.imprint","IMPRINT",EDGE,{"derivedFrom":subQ0}),-1.0]])]});}
            var Q67;
            {var subQ0=sQuery(id+"F2.wireOp",EDGE,"E27.0.62.0");Q67=makeQuery(id+"F2.imprint","IMPRINT",FACE,{"disambiguationData":[TD([[makeQuery(id+"F2.imprint","IMPRINT",EDGE,{"derivedFrom":subQ0}),-1.0]])]});}
            var Q68;
            {var subQ0=sQuery(id+"F2.wireOp",EDGE,"E41.0.15.0");Q68=makeQuery(id+"F2.imprint","IMPRINT",FACE,{"disambiguationData":[TD([[makeQuery(id+"F2.imprint","IMPRINT",EDGE,{"derivedFrom":subQ0}),-1.0]])]});}
            var Q69;
            {var subQ1=sQuery(id+"F2.wireOp",EDGE,"E27.0.61.0");Q69=makeQuery(id+"F2.imprint","IMPRINT",FACE,{"disambiguationData":[TD([[makeQuery(id+"F2.imprint","IMPRINT",EDGE,{"derivedFrom":subQ1}),-1.0]])]});}
            var Q70;
            {var subQ0=sQuery(id+"F2.wireOp",EDGE,"E33.0.30.0");Q70=makeQuery(id+"F2.imprint","IMPRINT",FACE,{"disambiguationData":[TD([[makeQuery(id+"F2.imprint","IMPRINT",EDGE,{"derivedFrom":subQ0}),-1.0]])]});}
            var Q71;
            {var subQ1=sQuery(id+"F2.wireOp",EDGE,"E27.0.60.0");Q71=makeQuery(id+"F2.imprint","IMPRINT",FACE,{"disambiguationData":[TD([[makeQuery(id+"F2.imprint","IMPRINT",EDGE,{"derivedFrom":subQ1}),-1.0]])]});}
            var Q72;
            {var subQ0=sQuery(id+"F2.wireOp",EDGE,"E47.0.7.0");Q72=makeQuery(id+"F2.imprint","IMPRINT",FACE,{"disambiguationData":[TD([[makeQuery(id+"F2.imprint","IMPRINT",EDGE,{"derivedFrom":subQ0}),-1.0]])]});}
            var Q73;
            {var subQ0=sQuery(id+"F2.wireOp",EDGE,"E27.0.59.0");Q73=makeQuery(id+"F2.imprint","IMPRINT",FACE,{"disambiguationData":[TD([[makeQuery(id+"F2.imprint","IMPRINT",EDGE,{"derivedFrom":subQ0}),-1.0]])]});}
            var Q74;
            {var subQ0=sQuery(id+"F2.wireOp",EDGE,"E33.0.29.0");Q74=makeQuery(id+"F2.imprint","IMPRINT",FACE,{"disambiguationData":[TD([[makeQuery(id+"F2.imprint","IMPRINT",EDGE,{"derivedFrom":subQ0}),-1.0]])]});}
            var Q75;
            {var subQ1=sQuery(id+"F2.wireOp",EDGE,"E27.0.58.0");Q75=makeQuery(id+"F2.imprint","IMPRINT",FACE,{"disambiguationData":[TD([[makeQuery(id+"F2.imprint","IMPRINT",EDGE,{"derivedFrom":subQ1}),-1.0]])]});}
            var Q76;
            {var subQ0=sQuery(id+"F2.wireOp",EDGE,"E41.0.14.0");Q76=makeQuery(id+"F2.imprint","IMPRINT",FACE,{"disambiguationData":[TD([[makeQuery(id+"F2.imprint","IMPRINT",EDGE,{"derivedFrom":subQ0}),-1.0]])]});}
            var Q77;
            {var subQ1=sQuery(id+"F2.wireOp",EDGE,"E27.0.57.0");Q77=makeQuery(id+"F2.imprint","IMPRINT",FACE,{"disambiguationData":[TD([[makeQuery(id+"F2.imprint","IMPRINT",EDGE,{"derivedFrom":subQ1}),-1.0]])]});}
            var Q78;
            {var subQ0=sQuery(id+"F2.wireOp",EDGE,"E33.0.28.0");Q78=makeQuery(id+"F2.imprint","IMPRINT",FACE,{"disambiguationData":[TD([[makeQuery(id+"F2.imprint","IMPRINT",EDGE,{"derivedFrom":subQ0}),-1.0]])]});}
            var Q79;
            {var subQ1=sQuery(id+"F2.wireOp",EDGE,"E27.0.56.0");Q79=makeQuery(id+"F2.imprint","IMPRINT",FACE,{"disambiguationData":[TD([[makeQuery(id+"F2.imprint","IMPRINT",EDGE,{"derivedFrom":subQ1}),-1.0]])]});}
            var Q80;
            {var subQ1=sQuery(id+"F2.wireOp",EDGE,"E15.0.7.0");Q80=makeQuery(id+"F2.imprint","IMPRINT",FACE,{"disambiguationData":[TD([[makeQuery(id+"F2.imprint","IMPRINT",EDGE,{"derivedFrom":subQ1}),-1.0]])]});}
            var Q81;
            {var subQ0=sQuery(id+"F2.wireOp",EDGE,"E27.0.55.0");Q81=makeQuery(id+"F2.imprint","IMPRINT",FACE,{"disambiguationData":[TD([[makeQuery(id+"F2.imprint","IMPRINT",EDGE,{"derivedFrom":subQ0}),-1.0]])]});}
            var Q82;
            {var subQ0=sQuery(id+"F2.wireOp",EDGE,"E33.0.27.0");Q82=makeQuery(id+"F2.imprint","IMPRINT",FACE,{"disambiguationData":[TD([[makeQuery(id+"F2.imprint","IMPRINT",EDGE,{"derivedFrom":subQ0}),-1.0]])]});}
            var Q83;
            {var subQ1=sQuery(id+"F2.wireOp",EDGE,"E27.0.54.0");Q83=makeQuery(id+"F2.imprint","IMPRINT",FACE,{"disambiguationData":[TD([[makeQuery(id+"F2.imprint","IMPRINT",EDGE,{"derivedFrom":subQ1}),-1.0]])]});}
            var Q84;
            {var subQ0=sQuery(id+"F2.wireOp",EDGE,"E41.0.13.0");Q84=makeQuery(id+"F2.imprint","IMPRINT",FACE,{"disambiguationData":[TD([[makeQuery(id+"F2.imprint","IMPRINT",EDGE,{"derivedFrom":subQ0}),-1.0]])]});}
            var Q85;
            {var subQ1=sQuery(id+"F2.wireOp",EDGE,"E27.0.53.0");Q85=makeQuery(id+"F2.imprint","IMPRINT",FACE,{"disambiguationData":[TD([[makeQuery(id+"F2.imprint","IMPRINT",EDGE,{"derivedFrom":subQ1}),-1.0]])]});}
            var Q86;
            {var subQ0=sQuery(id+"F2.wireOp",EDGE,"E33.0.26.0");Q86=makeQuery(id+"F2.imprint","IMPRINT",FACE,{"disambiguationData":[TD([[makeQuery(id+"F2.imprint","IMPRINT",EDGE,{"derivedFrom":subQ0}),-1.0]])]});}
            var Q87;
            {var subQ1=sQuery(id+"F2.wireOp",EDGE,"E27.0.52.0");Q87=makeQuery(id+"F2.imprint","IMPRINT",FACE,{"disambiguationData":[TD([[makeQuery(id+"F2.imprint","IMPRINT",EDGE,{"derivedFrom":subQ1}),-1.0]])]});}
            var Q88;
            {var subQ1=sQuery(id+"F2.wireOp",EDGE,"E47.0.6.0");Q88=makeQuery(id+"F2.imprint","IMPRINT",FACE,{"disambiguationData":[TD([[makeQuery(id+"F2.imprint","IMPRINT",EDGE,{"derivedFrom":subQ1}),-1.0]])]});}
            var Q89;
            {var subQ1=sQuery(id+"F2.wireOp",EDGE,"E27.0.51.0");Q89=makeQuery(id+"F2.imprint","IMPRINT",FACE,{"disambiguationData":[TD([[makeQuery(id+"F2.imprint","IMPRINT",EDGE,{"derivedFrom":subQ1}),-1.0]])]});}
            var Q90;
            {var subQ0=sQuery(id+"F2.wireOp",EDGE,"E33.0.25.0");Q90=makeQuery(id+"F2.imprint","IMPRINT",FACE,{"disambiguationData":[TD([[makeQuery(id+"F2.imprint","IMPRINT",EDGE,{"derivedFrom":subQ0}),-1.0]])]});}
            var Q91;
            {var subQ1=sQuery(id+"F2.wireOp",EDGE,"E27.0.50.0");Q91=makeQuery(id+"F2.imprint","IMPRINT",FACE,{"disambiguationData":[TD([[makeQuery(id+"F2.imprint","IMPRINT",EDGE,{"derivedFrom":subQ1}),-1.0]])]});}
            var Q92;
            {var subQ0=sQuery(id+"F2.wireOp",EDGE,"E41.0.12.0");Q92=makeQuery(id+"F2.imprint","IMPRINT",FACE,{"disambiguationData":[TD([[makeQuery(id+"F2.imprint","IMPRINT",EDGE,{"derivedFrom":subQ0}),-1.0]])]});}
            var Q93;
            {var subQ1=sQuery(id+"F2.wireOp",EDGE,"E27.0.49.0");Q93=makeQuery(id+"F2.imprint","IMPRINT",FACE,{"disambiguationData":[TD([[makeQuery(id+"F2.imprint","IMPRINT",EDGE,{"derivedFrom":subQ1}),-1.0]])]});}
            var Q94;
            {var subQ0=sQuery(id+"F2.wireOp",EDGE,"E33.0.24.0");Q94=makeQuery(id+"F2.imprint","IMPRINT",FACE,{"disambiguationData":[TD([[makeQuery(id+"F2.imprint","IMPRINT",EDGE,{"derivedFrom":subQ0}),-1.0]])]});}
            var Q95;
            {var subQ1=sQuery(id+"F2.wireOp",EDGE,"E27.0.48.0");Q95=makeQuery(id+"F2.imprint","IMPRINT",FACE,{"disambiguationData":[TD([[makeQuery(id+"F2.imprint","IMPRINT",EDGE,{"derivedFrom":subQ1}),-1.0]])]});}
            var Q96;
            {var subQ1=sQuery(id+"F2.wireOp",EDGE,"E15.0.6.0");Q96=makeQuery(id+"F2.imprint","IMPRINT",FACE,{"disambiguationData":[TD([[makeQuery(id+"F2.imprint","IMPRINT",EDGE,{"derivedFrom":subQ1}),-1.0]])]});}
            var Q97;
            {var subQ0=sQuery(id+"F2.wireOp",EDGE,"E27.0.47.0");Q97=makeQuery(id+"F2.imprint","IMPRINT",FACE,{"disambiguationData":[TD([[makeQuery(id+"F2.imprint","IMPRINT",EDGE,{"derivedFrom":subQ0}),-1.0]])]});}
            var Q98;
            {var subQ0=sQuery(id+"F2.wireOp",EDGE,"E33.0.23.0");Q98=makeQuery(id+"F2.imprint","IMPRINT",FACE,{"disambiguationData":[TD([[makeQuery(id+"F2.imprint","IMPRINT",EDGE,{"derivedFrom":subQ0}),-1.0]])]});}
            var Q99;
            {var subQ1=sQuery(id+"F2.wireOp",EDGE,"E27.0.46.0");Q99=makeQuery(id+"F2.imprint","IMPRINT",FACE,{"disambiguationData":[TD([[makeQuery(id+"F2.imprint","IMPRINT",EDGE,{"derivedFrom":subQ1}),-1.0]])]});}
            var Q100;
            {var subQ0=sQuery(id+"F2.wireOp",EDGE,"E41.0.11.0");Q100=makeQuery(id+"F2.imprint","IMPRINT",FACE,{"disambiguationData":[TD([[makeQuery(id+"F2.imprint","IMPRINT",EDGE,{"derivedFrom":subQ0}),-1.0]])]});}
            var Q101;
            {var subQ1=sQuery(id+"F2.wireOp",EDGE,"E27.0.45.0");Q101=makeQuery(id+"F2.imprint","IMPRINT",FACE,{"disambiguationData":[TD([[makeQuery(id+"F2.imprint","IMPRINT",EDGE,{"derivedFrom":subQ1}),-1.0]])]});}
            var Q102;
            {var subQ0=sQuery(id+"F2.wireOp",EDGE,"E33.0.22.0");Q102=makeQuery(id+"F2.imprint","IMPRINT",FACE,{"disambiguationData":[TD([[makeQuery(id+"F2.imprint","IMPRINT",EDGE,{"derivedFrom":subQ0}),-1.0]])]});}
            var Q103;
            {var subQ0=sQuery(id+"F2.wireOp",EDGE,"E27.0.44.0");Q103=makeQuery(id+"F2.imprint","IMPRINT",FACE,{"disambiguationData":[TD([[makeQuery(id+"F2.imprint","IMPRINT",EDGE,{"derivedFrom":subQ0}),-1.0]])]});}
            var Q104;
            {var subQ0=sQuery(id+"F2.wireOp",EDGE,"E47.0.5.0");Q104=makeQuery(id+"F2.imprint","IMPRINT",FACE,{"disambiguationData":[TD([[makeQuery(id+"F2.imprint","IMPRINT",EDGE,{"derivedFrom":subQ0}),-1.0]])]});}
            var Q105;
            {var subQ1=sQuery(id+"F2.wireOp",EDGE,"E27.0.43.0");Q105=makeQuery(id+"F2.imprint","IMPRINT",FACE,{"disambiguationData":[TD([[makeQuery(id+"F2.imprint","IMPRINT",EDGE,{"derivedFrom":subQ1}),-1.0]])]});}
            var Q106;
            {var subQ0=sQuery(id+"F2.wireOp",EDGE,"E33.0.21.0");Q106=makeQuery(id+"F2.imprint","IMPRINT",FACE,{"disambiguationData":[TD([[makeQuery(id+"F2.imprint","IMPRINT",EDGE,{"derivedFrom":subQ0}),-1.0]])]});}
            var Q107;
            {var subQ1=sQuery(id+"F2.wireOp",EDGE,"E27.0.42.0");Q107=makeQuery(id+"F2.imprint","IMPRINT",FACE,{"disambiguationData":[TD([[makeQuery(id+"F2.imprint","IMPRINT",EDGE,{"derivedFrom":subQ1}),-1.0]])]});}
            var Q108;
            {var subQ0=sQuery(id+"F2.wireOp",EDGE,"E41.0.10.0");Q108=makeQuery(id+"F2.imprint","IMPRINT",FACE,{"disambiguationData":[TD([[makeQuery(id+"F2.imprint","IMPRINT",EDGE,{"derivedFrom":subQ0}),-1.0]])]});}
            var Q109;
            {var subQ1=sQuery(id+"F2.wireOp",EDGE,"E27.0.41.0");Q109=makeQuery(id+"F2.imprint","IMPRINT",FACE,{"disambiguationData":[TD([[makeQuery(id+"F2.imprint","IMPRINT",EDGE,{"derivedFrom":subQ1}),-1.0]])]});}
            var Q110;
            {var subQ0=sQuery(id+"F2.wireOp",EDGE,"E33.0.20.0");Q110=makeQuery(id+"F2.imprint","IMPRINT",FACE,{"disambiguationData":[TD([[makeQuery(id+"F2.imprint","IMPRINT",EDGE,{"derivedFrom":subQ0}),-1.0]])]});}
            var Q111;
            {var subQ1=sQuery(id+"F2.wireOp",EDGE,"E27.0.40.0");Q111=makeQuery(id+"F2.imprint","IMPRINT",FACE,{"disambiguationData":[TD([[makeQuery(id+"F2.imprint","IMPRINT",EDGE,{"derivedFrom":subQ1}),-1.0]])]});}
            var Q112;
            {var subQ0=sQuery(id+"F2.wireOp",EDGE,"E15.0.5.0");Q112=makeQuery(id+"F2.imprint","IMPRINT",FACE,{"disambiguationData":[TD([[makeQuery(id+"F2.imprint","IMPRINT",EDGE,{"derivedFrom":subQ0}),-1.0]])]});}
            var Q113;
            {var subQ1=sQuery(id+"F2.wireOp",EDGE,"E27.0.39.0");Q113=makeQuery(id+"F2.imprint","IMPRINT",FACE,{"disambiguationData":[TD([[makeQuery(id+"F2.imprint","IMPRINT",EDGE,{"derivedFrom":subQ1}),-1.0]])]});}
            var Q114;
            {var subQ0=sQuery(id+"F2.wireOp",EDGE,"E33.0.19.0");Q114=makeQuery(id+"F2.imprint","IMPRINT",FACE,{"disambiguationData":[TD([[makeQuery(id+"F2.imprint","IMPRINT",EDGE,{"derivedFrom":subQ0}),-1.0]])]});}
            var Q115;
            {var subQ1=sQuery(id+"F2.wireOp",EDGE,"E27.0.38.0");Q115=makeQuery(id+"F2.imprint","IMPRINT",FACE,{"disambiguationData":[TD([[makeQuery(id+"F2.imprint","IMPRINT",EDGE,{"derivedFrom":subQ1}),-1.0]])]});}
            var Q116;
            {var subQ0=sQuery(id+"F2.wireOp",EDGE,"E41.0.9.0");Q116=makeQuery(id+"F2.imprint","IMPRINT",FACE,{"disambiguationData":[TD([[makeQuery(id+"F2.imprint","IMPRINT",EDGE,{"derivedFrom":subQ0}),-1.0]])]});}
            var Q117;
            {var subQ1=sQuery(id+"F2.wireOp",EDGE,"E27.0.37.0");Q117=makeQuery(id+"F2.imprint","IMPRINT",FACE,{"disambiguationData":[TD([[makeQuery(id+"F2.imprint","IMPRINT",EDGE,{"derivedFrom":subQ1}),-1.0]])]});}
            var Q118;
            {var subQ0=sQuery(id+"F2.wireOp",EDGE,"E33.0.18.0");Q118=makeQuery(id+"F2.imprint","IMPRINT",FACE,{"disambiguationData":[TD([[makeQuery(id+"F2.imprint","IMPRINT",EDGE,{"derivedFrom":subQ0}),-1.0]])]});}
            var Q119;
            {var subQ1=sQuery(id+"F2.wireOp",EDGE,"E27.0.36.0");Q119=makeQuery(id+"F2.imprint","IMPRINT",FACE,{"disambiguationData":[TD([[makeQuery(id+"F2.imprint","IMPRINT",EDGE,{"derivedFrom":subQ1}),-1.0]])]});}
            var Q120;
            {var subQ1=sQuery(id+"F2.wireOp",EDGE,"E47.0.4.0");Q120=makeQuery(id+"F2.imprint","IMPRINT",FACE,{"disambiguationData":[TD([[makeQuery(id+"F2.imprint","IMPRINT",EDGE,{"derivedFrom":subQ1}),-1.0]])]});}
            var Q121;
            {var subQ1=sQuery(id+"F2.wireOp",EDGE,"E27.0.35.0");Q121=makeQuery(id+"F2.imprint","IMPRINT",FACE,{"disambiguationData":[TD([[makeQuery(id+"F2.imprint","IMPRINT",EDGE,{"derivedFrom":subQ1}),-1.0]])]});}
            var Q122;
            {var subQ0=sQuery(id+"F2.wireOp",EDGE,"E33.0.17.0");Q122=makeQuery(id+"F2.imprint","IMPRINT",FACE,{"disambiguationData":[TD([[makeQuery(id+"F2.imprint","IMPRINT",EDGE,{"derivedFrom":subQ0}),-1.0]])]});}
            var Q123;
            {var subQ0=sQuery(id+"F2.wireOp",EDGE,"E27.0.34.0");Q123=makeQuery(id+"F2.imprint","IMPRINT",FACE,{"disambiguationData":[TD([[makeQuery(id+"F2.imprint","IMPRINT",EDGE,{"derivedFrom":subQ0}),-1.0]])]});}
            var Q124;
            {var subQ0=sQuery(id+"F2.wireOp",EDGE,"E41.0.8.0");Q124=makeQuery(id+"F2.imprint","IMPRINT",FACE,{"disambiguationData":[TD([[makeQuery(id+"F2.imprint","IMPRINT",EDGE,{"derivedFrom":subQ0}),-1.0]])]});}
            var Q125;
            {var subQ1=sQuery(id+"F2.wireOp",EDGE,"E27.0.33.0");Q125=makeQuery(id+"F2.imprint","IMPRINT",FACE,{"disambiguationData":[TD([[makeQuery(id+"F2.imprint","IMPRINT",EDGE,{"derivedFrom":subQ1}),-1.0]])]});}
            var Q126;
            {var subQ0=sQuery(id+"F2.wireOp",EDGE,"E33.0.16.0");Q126=makeQuery(id+"F2.imprint","IMPRINT",FACE,{"disambiguationData":[TD([[makeQuery(id+"F2.imprint","IMPRINT",EDGE,{"derivedFrom":subQ0}),-1.0]])]});}
            var Q127;
            {var subQ1=sQuery(id+"F2.wireOp",EDGE,"E27.0.32.0");Q127=makeQuery(id+"F2.imprint","IMPRINT",FACE,{"disambiguationData":[TD([[makeQuery(id+"F2.imprint","IMPRINT",EDGE,{"derivedFrom":subQ1}),-1.0]])]});}
            var Q128;
            {var subQ1=sQuery(id+"F2.wireOp",EDGE,"E15.0.4.0");Q128=makeQuery(id+"F2.imprint","IMPRINT",FACE,{"disambiguationData":[TD([[makeQuery(id+"F2.imprint","IMPRINT",EDGE,{"derivedFrom":subQ1}),-1.0]])]});}
            var Q129;
            {var subQ1=sQuery(id+"F2.wireOp",EDGE,"E27.0.31.0");Q129=makeQuery(id+"F2.imprint","IMPRINT",FACE,{"disambiguationData":[TD([[makeQuery(id+"F2.imprint","IMPRINT",EDGE,{"derivedFrom":subQ1}),-1.0]])]});}
            var Q130;
            {var subQ0=sQuery(id+"F2.wireOp",EDGE,"E33.0.15.0");Q130=makeQuery(id+"F2.imprint","IMPRINT",FACE,{"disambiguationData":[TD([[makeQuery(id+"F2.imprint","IMPRINT",EDGE,{"derivedFrom":subQ0}),-1.0]])]});}
            var Q131;
            {var subQ1=sQuery(id+"F2.wireOp",EDGE,"E27.0.30.0");Q131=makeQuery(id+"F2.imprint","IMPRINT",FACE,{"disambiguationData":[TD([[makeQuery(id+"F2.imprint","IMPRINT",EDGE,{"derivedFrom":subQ1}),-1.0]])]});}
            var Q132;
            {var subQ0=sQuery(id+"F2.wireOp",EDGE,"E41.0.7.0");Q132=makeQuery(id+"F2.imprint","IMPRINT",FACE,{"disambiguationData":[TD([[makeQuery(id+"F2.imprint","IMPRINT",EDGE,{"derivedFrom":subQ0}),-1.0]])]});}
            var Q133;
            {var subQ0=sQuery(id+"F2.wireOp",EDGE,"E27.0.29.0");Q133=makeQuery(id+"F2.imprint","IMPRINT",FACE,{"disambiguationData":[TD([[makeQuery(id+"F2.imprint","IMPRINT",EDGE,{"derivedFrom":subQ0}),-1.0]])]});}
            var Q134;
            {var subQ0=sQuery(id+"F2.wireOp",EDGE,"E33.0.14.0");Q134=makeQuery(id+"F2.imprint","IMPRINT",FACE,{"disambiguationData":[TD([[makeQuery(id+"F2.imprint","IMPRINT",EDGE,{"derivedFrom":subQ0}),-1.0]])]});}
            var Q135;
            {var subQ1=sQuery(id+"F2.wireOp",EDGE,"E27.0.28.0");Q135=makeQuery(id+"F2.imprint","IMPRINT",FACE,{"disambiguationData":[TD([[makeQuery(id+"F2.imprint","IMPRINT",EDGE,{"derivedFrom":subQ1}),-1.0]])]});}
            var Q136;
            {var subQ1=sQuery(id+"F2.wireOp",EDGE,"E47.0.3.0");Q136=makeQuery(id+"F2.imprint","IMPRINT",FACE,{"disambiguationData":[TD([[makeQuery(id+"F2.imprint","IMPRINT",EDGE,{"derivedFrom":subQ1}),-1.0]])]});}
            var Q137;
            {var subQ1=sQuery(id+"F2.wireOp",EDGE,"E27.0.27.0");Q137=makeQuery(id+"F2.imprint","IMPRINT",FACE,{"disambiguationData":[TD([[makeQuery(id+"F2.imprint","IMPRINT",EDGE,{"derivedFrom":subQ1}),-1.0]])]});}
            var Q138;
            {var subQ0=sQuery(id+"F2.wireOp",EDGE,"E33.0.13.0");Q138=makeQuery(id+"F2.imprint","IMPRINT",FACE,{"disambiguationData":[TD([[makeQuery(id+"F2.imprint","IMPRINT",EDGE,{"derivedFrom":subQ0}),-1.0]])]});}
            var Q139;
            {var subQ1=sQuery(id+"F2.wireOp",EDGE,"E27.0.26.0");Q139=makeQuery(id+"F2.imprint","IMPRINT",FACE,{"disambiguationData":[TD([[makeQuery(id+"F2.imprint","IMPRINT",EDGE,{"derivedFrom":subQ1}),-1.0]])]});}
            var Q140;
            {var subQ0=sQuery(id+"F2.wireOp",EDGE,"E41.0.6.0");Q140=makeQuery(id+"F2.imprint","IMPRINT",FACE,{"disambiguationData":[TD([[makeQuery(id+"F2.imprint","IMPRINT",EDGE,{"derivedFrom":subQ0}),-1.0]])]});}
            var Q141;
            {var subQ1=sQuery(id+"F2.wireOp",EDGE,"E27.0.25.0");Q141=makeQuery(id+"F2.imprint","IMPRINT",FACE,{"disambiguationData":[TD([[makeQuery(id+"F2.imprint","IMPRINT",EDGE,{"derivedFrom":subQ1}),-1.0]])]});}
            var Q142;
            {var subQ0=sQuery(id+"F2.wireOp",EDGE,"E33.0.12.0");Q142=makeQuery(id+"F2.imprint","IMPRINT",FACE,{"disambiguationData":[TD([[makeQuery(id+"F2.imprint","IMPRINT",EDGE,{"derivedFrom":subQ0}),-1.0]])]});}
            var Q143;
            {var subQ1=sQuery(id+"F2.wireOp",EDGE,"E27.0.24.0");Q143=makeQuery(id+"F2.imprint","IMPRINT",FACE,{"disambiguationData":[TD([[makeQuery(id+"F2.imprint","IMPRINT",EDGE,{"derivedFrom":subQ1}),-1.0]])]});}
            var Q144;
            {var subQ1=sQuery(id+"F2.wireOp",EDGE,"E15.0.3.0");Q144=makeQuery(id+"F2.imprint","IMPRINT",FACE,{"disambiguationData":[TD([[makeQuery(id+"F2.imprint","IMPRINT",EDGE,{"derivedFrom":subQ1}),-1.0]])]});}
            var Q145;
            {var subQ1=sQuery(id+"F2.wireOp",EDGE,"E27.0.23.0");Q145=makeQuery(id+"F2.imprint","IMPRINT",FACE,{"disambiguationData":[TD([[makeQuery(id+"F2.imprint","IMPRINT",EDGE,{"derivedFrom":subQ1}),-1.0]])]});}
            var Q146;
            {var subQ0=sQuery(id+"F2.wireOp",EDGE,"E33.0.11.0");Q146=makeQuery(id+"F2.imprint","IMPRINT",FACE,{"disambiguationData":[TD([[makeQuery(id+"F2.imprint","IMPRINT",EDGE,{"derivedFrom":subQ0}),-1.0]])]});}
            var Q147;
            {var subQ1=sQuery(id+"F2.wireOp",EDGE,"E27.0.22.0");Q147=makeQuery(id+"F2.imprint","IMPRINT",FACE,{"disambiguationData":[TD([[makeQuery(id+"F2.imprint","IMPRINT",EDGE,{"derivedFrom":subQ1}),-1.0]])]});}
            var Q148;
            {var subQ0=sQuery(id+"F2.wireOp",EDGE,"E41.0.5.0");Q148=makeQuery(id+"F2.imprint","IMPRINT",FACE,{"disambiguationData":[TD([[makeQuery(id+"F2.imprint","IMPRINT",EDGE,{"derivedFrom":subQ0}),-1.0]])]});}
            var Q149;
            {var subQ1=sQuery(id+"F2.wireOp",EDGE,"E27.0.21.0");Q149=makeQuery(id+"F2.imprint","IMPRINT",FACE,{"disambiguationData":[TD([[makeQuery(id+"F2.imprint","IMPRINT",EDGE,{"derivedFrom":subQ1}),-1.0]])]});}
            var Q150;
            {var subQ0=sQuery(id+"F2.wireOp",EDGE,"E33.0.10.0");Q150=makeQuery(id+"F2.imprint","IMPRINT",FACE,{"disambiguationData":[TD([[makeQuery(id+"F2.imprint","IMPRINT",EDGE,{"derivedFrom":subQ0}),-1.0]])]});}
            var Q151;
            {var subQ1=sQuery(id+"F2.wireOp",EDGE,"E27.0.20.0");Q151=makeQuery(id+"F2.imprint","IMPRINT",FACE,{"disambiguationData":[TD([[makeQuery(id+"F2.imprint","IMPRINT",EDGE,{"derivedFrom":subQ1}),-1.0]])]});}
            var Q152;
            {var subQ1=sQuery(id+"F2.wireOp",EDGE,"E47.0.2.0");Q152=makeQuery(id+"F2.imprint","IMPRINT",FACE,{"disambiguationData":[TD([[makeQuery(id+"F2.imprint","IMPRINT",EDGE,{"derivedFrom":subQ1}),-1.0]])]});}
            var Q153;
            {var subQ1=sQuery(id+"F2.wireOp",EDGE,"E27.0.19.0");Q153=makeQuery(id+"F2.imprint","IMPRINT",FACE,{"disambiguationData":[TD([[makeQuery(id+"F2.imprint","IMPRINT",EDGE,{"derivedFrom":subQ1}),-1.0]])]});}
            var Q154;
            {var subQ0=sQuery(id+"F2.wireOp",EDGE,"E33.0.9.0");Q154=makeQuery(id+"F2.imprint","IMPRINT",FACE,{"disambiguationData":[TD([[makeQuery(id+"F2.imprint","IMPRINT",EDGE,{"derivedFrom":subQ0}),-1.0]])]});}
            var Q155;
            {var subQ1=sQuery(id+"F2.wireOp",EDGE,"E27.0.18.0");Q155=makeQuery(id+"F2.imprint","IMPRINT",FACE,{"disambiguationData":[TD([[makeQuery(id+"F2.imprint","IMPRINT",EDGE,{"derivedFrom":subQ1}),-1.0]])]});}
            var Q156;
            {var subQ0=sQuery(id+"F2.wireOp",EDGE,"E41.0.4.0");Q156=makeQuery(id+"F2.imprint","IMPRINT",FACE,{"disambiguationData":[TD([[makeQuery(id+"F2.imprint","IMPRINT",EDGE,{"derivedFrom":subQ0}),-1.0]])]});}
            var Q157;
            {var subQ1=sQuery(id+"F2.wireOp",EDGE,"E27.0.17.0");Q157=makeQuery(id+"F2.imprint","IMPRINT",FACE,{"disambiguationData":[TD([[makeQuery(id+"F2.imprint","IMPRINT",EDGE,{"derivedFrom":subQ1}),-1.0]])]});}
            var Q158;
            {var subQ0=sQuery(id+"F2.wireOp",EDGE,"E33.0.8.0");Q158=makeQuery(id+"F2.imprint","IMPRINT",FACE,{"disambiguationData":[TD([[makeQuery(id+"F2.imprint","IMPRINT",EDGE,{"derivedFrom":subQ0}),-1.0]])]});}
            var Q159;
            {var subQ1=sQuery(id+"F2.wireOp",EDGE,"E27.0.16.0");Q159=makeQuery(id+"F2.imprint","IMPRINT",FACE,{"disambiguationData":[TD([[makeQuery(id+"F2.imprint","IMPRINT",EDGE,{"derivedFrom":subQ1}),-1.0]])]});}
            var Q160;
            {var subQ1=sQuery(id+"F2.wireOp",EDGE,"E15.0.2.0");Q160=makeQuery(id+"F2.imprint","IMPRINT",FACE,{"disambiguationData":[TD([[makeQuery(id+"F2.imprint","IMPRINT",EDGE,{"derivedFrom":subQ1}),-1.0]])]});}
            var Q161;
            {var subQ1=sQuery(id+"F2.wireOp",EDGE,"E27.0.15.0");Q161=makeQuery(id+"F2.imprint","IMPRINT",FACE,{"disambiguationData":[TD([[makeQuery(id+"F2.imprint","IMPRINT",EDGE,{"derivedFrom":subQ1}),-1.0]])]});}
            var Q162;
            {var subQ0=sQuery(id+"F2.wireOp",EDGE,"E33.0.7.0");Q162=makeQuery(id+"F2.imprint","IMPRINT",FACE,{"disambiguationData":[TD([[makeQuery(id+"F2.imprint","IMPRINT",EDGE,{"derivedFrom":subQ0}),-1.0]])]});}
            var Q163;
            {var subQ0=sQuery(id+"F2.wireOp",EDGE,"E27.0.14.0");Q163=makeQuery(id+"F2.imprint","IMPRINT",FACE,{"disambiguationData":[TD([[makeQuery(id+"F2.imprint","IMPRINT",EDGE,{"derivedFrom":subQ0}),-1.0]])]});}
            var Q164;
            {var subQ0=sQuery(id+"F2.wireOp",EDGE,"E41.0.3.0");Q164=makeQuery(id+"F2.imprint","IMPRINT",FACE,{"disambiguationData":[TD([[makeQuery(id+"F2.imprint","IMPRINT",EDGE,{"derivedFrom":subQ0}),-1.0]])]});}
            var Q165;
            {var subQ1=sQuery(id+"F2.wireOp",EDGE,"E27.0.13.0");Q165=makeQuery(id+"F2.imprint","IMPRINT",FACE,{"disambiguationData":[TD([[makeQuery(id+"F2.imprint","IMPRINT",EDGE,{"derivedFrom":subQ1}),-1.0]])]});}
            var Q166;
            {var subQ0=sQuery(id+"F2.wireOp",EDGE,"E33.0.6.0");Q166=makeQuery(id+"F2.imprint","IMPRINT",FACE,{"disambiguationData":[TD([[makeQuery(id+"F2.imprint","IMPRINT",EDGE,{"derivedFrom":subQ0}),-1.0]])]});}
            var Q167;
            {var subQ1=sQuery(id+"F2.wireOp",EDGE,"E27.0.12.0");Q167=makeQuery(id+"F2.imprint","IMPRINT",FACE,{"disambiguationData":[TD([[makeQuery(id+"F2.imprint","IMPRINT",EDGE,{"derivedFrom":subQ1}),-1.0]])]});}
            var Q168;
            {var subQ1=sQuery(id+"F2.wireOp",EDGE,"E47.0.1.0");Q168=makeQuery(id+"F2.imprint","IMPRINT",FACE,{"disambiguationData":[TD([[makeQuery(id+"F2.imprint","IMPRINT",EDGE,{"derivedFrom":subQ1}),-1.0]])]});}
            var Q169;
            {var subQ0=sQuery(id+"F2.wireOp",EDGE,"E27.0.11.0");Q169=makeQuery(id+"F2.imprint","IMPRINT",FACE,{"disambiguationData":[TD([[makeQuery(id+"F2.imprint","IMPRINT",EDGE,{"derivedFrom":subQ0}),-1.0]])]});}
            var Q170;
            {var subQ0=sQuery(id+"F2.wireOp",EDGE,"E33.0.5.0");Q170=makeQuery(id+"F2.imprint","IMPRINT",FACE,{"disambiguationData":[TD([[makeQuery(id+"F2.imprint","IMPRINT",EDGE,{"derivedFrom":subQ0}),-1.0]])]});}
            var Q171;
            {var subQ1=sQuery(id+"F2.wireOp",EDGE,"E27.0.10.0");Q171=makeQuery(id+"F2.imprint","IMPRINT",FACE,{"disambiguationData":[TD([[makeQuery(id+"F2.imprint","IMPRINT",EDGE,{"derivedFrom":subQ1}),-1.0]])]});}
            var Q172;
            {var subQ0=sQuery(id+"F2.wireOp",EDGE,"E41.0.2.0");Q172=makeQuery(id+"F2.imprint","IMPRINT",FACE,{"disambiguationData":[TD([[makeQuery(id+"F2.imprint","IMPRINT",EDGE,{"derivedFrom":subQ0}),-1.0]])]});}
            var Q173;
            {var subQ0=sQuery(id+"F2.wireOp",EDGE,"E27.0.9.0");Q173=makeQuery(id+"F2.imprint","IMPRINT",FACE,{"disambiguationData":[TD([[makeQuery(id+"F2.imprint","IMPRINT",EDGE,{"derivedFrom":subQ0}),-1.0]])]});}
            var Q174;
            {var subQ0=sQuery(id+"F2.wireOp",EDGE,"E33.0.4.0");Q174=makeQuery(id+"F2.imprint","IMPRINT",FACE,{"disambiguationData":[TD([[makeQuery(id+"F2.imprint","IMPRINT",EDGE,{"derivedFrom":subQ0}),-1.0]])]});}
            var Q175;
            {var subQ1=sQuery(id+"F2.wireOp",EDGE,"E27.0.8.0");Q175=makeQuery(id+"F2.imprint","IMPRINT",FACE,{"disambiguationData":[TD([[makeQuery(id+"F2.imprint","IMPRINT",EDGE,{"derivedFrom":subQ1}),-1.0]])]});}
            var Q176;
            {var subQ1=sQuery(id+"F2.wireOp",EDGE,"E15.0.1.0");Q176=makeQuery(id+"F2.imprint","IMPRINT",FACE,{"disambiguationData":[TD([[makeQuery(id+"F2.imprint","IMPRINT",EDGE,{"derivedFrom":subQ1}),-1.0]])]});}
            var Q177;
            {var subQ1=sQuery(id+"F2.wireOp",EDGE,"E27.0.7.0");Q177=makeQuery(id+"F2.imprint","IMPRINT",FACE,{"disambiguationData":[TD([[makeQuery(id+"F2.imprint","IMPRINT",EDGE,{"derivedFrom":subQ1}),-1.0]])]});}
            var Q178;
            {var subQ0=sQuery(id+"F2.wireOp",EDGE,"E33.0.3.0");Q178=makeQuery(id+"F2.imprint","IMPRINT",FACE,{"disambiguationData":[TD([[makeQuery(id+"F2.imprint","IMPRINT",EDGE,{"derivedFrom":subQ0}),-1.0]])]});}
            var Q179;
            {var subQ1=sQuery(id+"F2.wireOp",EDGE,"E27.0.6.0");Q179=makeQuery(id+"F2.imprint","IMPRINT",FACE,{"disambiguationData":[TD([[makeQuery(id+"F2.imprint","IMPRINT",EDGE,{"derivedFrom":subQ1}),-1.0]])]});}
            var Q180;
            {var subQ0=sQuery(id+"F2.wireOp",EDGE,"E41.0.1.0");Q180=makeQuery(id+"F2.imprint","IMPRINT",FACE,{"disambiguationData":[TD([[makeQuery(id+"F2.imprint","IMPRINT",EDGE,{"derivedFrom":subQ0}),-1.0]])]});}
            var Q181;
            {var subQ1=sQuery(id+"F2.wireOp",EDGE,"E27.0.5.0");Q181=makeQuery(id+"F2.imprint","IMPRINT",FACE,{"disambiguationData":[TD([[makeQuery(id+"F2.imprint","IMPRINT",EDGE,{"derivedFrom":subQ1}),-1.0]])]});}
            var Q182;
            {var subQ0=sQuery(id+"F2.wireOp",EDGE,"E33.0.2.0");Q182=makeQuery(id+"F2.imprint","IMPRINT",FACE,{"disambiguationData":[TD([[makeQuery(id+"F2.imprint","IMPRINT",EDGE,{"derivedFrom":subQ0}),-1.0]])]});}
            var Q183;
            {var subQ1=sQuery(id+"F2.wireOp",EDGE,"E27.0.4.0");Q183=makeQuery(id+"F2.imprint","IMPRINT",FACE,{"disambiguationData":[TD([[makeQuery(id+"F2.imprint","IMPRINT",EDGE,{"derivedFrom":subQ1}),-1.0]])]});}
            var Q184;
            Q184=makeQuery(id+"F2.imprint","IMPRINT",FACE,{"disambiguationData":[TD([[makeQuery(id+"F2.imprint","IMPRINT",EDGE,{"derivedFrom":sQuery(id+"F2.wireOp",EDGE,"E43")}),1.0]])]});
            var Q185;
            {var subQ1=sQuery(id+"F2.wireOp",EDGE,"E27.0.3.0");Q185=makeQuery(id+"F2.imprint","IMPRINT",FACE,{"disambiguationData":[TD([[makeQuery(id+"F2.imprint","IMPRINT",EDGE,{"derivedFrom":subQ1}),-1.0]])]});}
            var Q186;
            {var subQ0=sQuery(id+"F2.wireOp",EDGE,"E33.0.1.0");Q186=makeQuery(id+"F2.imprint","IMPRINT",FACE,{"disambiguationData":[TD([[makeQuery(id+"F2.imprint","IMPRINT",EDGE,{"derivedFrom":subQ0}),-1.0]])]});}
            var Q187;
            {var subQ1=sQuery(id+"F2.wireOp",EDGE,"E27.0.2.0");Q187=makeQuery(id+"F2.imprint","IMPRINT",FACE,{"disambiguationData":[TD([[makeQuery(id+"F2.imprint","IMPRINT",EDGE,{"derivedFrom":subQ1}),-1.0]])]});}
            var Q188;
            {var subQ1=sQuery(id+"F2.wireOp",EDGE,"E27.0.1.0");Q188=makeQuery(id+"F2.imprint","IMPRINT",FACE,{"disambiguationData":[TD([[makeQuery(id+"F2.imprint","IMPRINT",EDGE,{"derivedFrom":subQ1}),-1.0]])]});}
            var Q189;
            {var subQ0=sQuery(id+"F2.wireOp",EDGE,"E31");Q189=makeQuery(id+"F2.imprint","IMPRINT",FACE,{"disambiguationData":[TD([[makeQuery(id+"F2.imprint","IMPRINT",EDGE,{"derivedFrom":subQ0}),-1.0]])]});}
            var Q190;
            Q190=makeQuery(id+"F2.imprint","IMPRINT",FACE,{"disambiguationData":[TD([[makeQuery(id+"F2.imprint","IMPRINT",EDGE,{"derivedFrom":sQuery(id+"F2.wireOp",EDGE,"E21")}),-1.0]])]});
            var Q191;
            Q191=makeQuery(id+"F2.imprint","IMPRINT",FACE,{"disambiguationData":[TD([[makeQuery(id+"F2.imprint","IMPRINT",EDGE,{"derivedFrom":sQuery(id+"F2.wireOp",EDGE,"E11")}),1.0]])]});
            var Q192;
            {var subQ4=sQuery(id+"F2.wireOp",EDGE,"E34");Q192=makeQuery(id+"F2.imprint","IMPRINT",FACE,{"disambiguationData":[TD([[makeQuery(id+"F2.imprint","IMPRINT",EDGE,{"derivedFrom":subQ4}),1.0]])]});}
            var Q193;
            {var subQ4=sQuery(id+"F2.wireOp",EDGE,"E34");Q193=makeQuery(id+"F2.imprint","IMPRINT",FACE,{"disambiguationData":[TD([[makeQuery(id+"F2.imprint","IMPRINT",EDGE,{"derivedFrom":subQ4}),-1.0]])]});}
            extrude(context, id + "F3", {"entities" : qUnion([Q0, Q1, Q2, Q3, Q4, Q5, Q6, Q7, Q8, Q9, Q10, Q11, Q12, Q13, Q14, Q15, Q16, Q17, Q18, Q19, Q20, Q21, Q22, Q23, Q24, Q25, Q26, Q27, Q28, Q29, Q30, Q31, Q32, Q33, Q34, Q35, Q36, Q37, Q38, Q39, Q40, Q41, Q42, Q43, Q44, Q45, Q46, Q47, Q48, Q49, Q50, Q51, Q52, Q53, Q54, Q55, Q56, Q57, Q58, Q59, Q60, Q61, Q62, Q63, Q64, Q65, Q66, Q67, Q68, Q69, Q70, Q71, Q72, Q73, Q74, Q75, Q76, Q77, Q78, Q79, Q80, Q81, Q82, Q83, Q84, Q85, Q86, Q87, Q88, Q89, Q90, Q91, Q92, Q93, Q94, Q95, Q96, Q97, Q98, Q99, Q100, Q101, Q102, Q103, Q104, Q105, Q106, Q107, Q108, Q109, Q110, Q111, Q112, Q113, Q114, Q115, Q116, Q117, Q118, Q119, Q120, Q121, Q122, Q123, Q124, Q125, Q126, Q127, Q128, Q129, Q130, Q131, Q132, Q133, Q134, Q135, Q136, Q137, Q138, Q139, Q140, Q141, Q142, Q143, Q144, Q145, Q146, Q147, Q148, Q149, Q150, Q151, Q152, Q153, Q154, Q155, Q156, Q157, Q158, Q159, Q160, Q161, Q162, Q163, Q164, Q165, Q166, Q167, Q168, Q169, Q170, Q171, Q172, Q173, Q174, Q175, Q176, Q177, Q178, Q179, Q180, Q181, Q182, Q183, Q184, Q185, Q186, Q187, Q188, Q189, Q190, Q191, Q192, Q193]), "operationType" : NewBodyOperationType.REMOVE, "oppositeDirection" : true, "depth" : 3.17 * mm});
        }
        {
            var Q0;
            Q0=makeQuery(id+"F1.opExtrude","SWEPT_FACE",FACE,{"disambiguationData":[OSD([sQuery(id+"F0.wireOp",EDGE,"E7")])]});
            var sketch = newSketch(context, id + "F4", { "sketchPlane" : qUnion([Q0])});
            skLineSegment(sketch, "E48.0.0", {"start": v(12.7, 0) * mm, "end": v(6.35, 0) * mm});
            skLineSegment(sketch, "E48.0.2", {"start": v(6.35, -311.15) * mm, "end": v(12.7, -311.15) * mm});
            skLineSegment(sketch, "E48.0.3", {"start": v(12.7, -311.15) * mm, "end": v(12.7, 0) * mm});
            skLineSegment(sketch, "E49", {"start": v(7.62, -3.05) * mm, "end": v(7.62, -3.18) * mm});
            skLineSegment(sketch, "E50", {"start": v(7.62, -3.18) * mm, "end": v(7.62, -3.3) * mm});
            skLineSegment(sketch, "E51", {"start": v(7.62, -3.18) * mm, "end": v(7.62, -3.05) * mm});
            skLineSegment(sketch, "E52", {"start": v(7.62, -3.05) * mm, "end": v(12.7, -3.05) * mm});
            skLineSegment(sketch, "E53.0", {"start": v(-7.62, -3.05) * mm, "end": v(-12.7, -3.05) * mm});
            skLineSegment(sketch, "E54", {"start": v(7.62, -3.3) * mm, "end": v(12.7, -3.3) * mm});
            skLineSegment(sketch, "E55.0.1.0", {"start": v(7.62, -13.05) * mm, "end": v(12.7, -13.05) * mm});
            skLineSegment(sketch, "E55.0.1.1", {"start": v(7.62, -13.3) * mm, "end": v(12.7, -13.3) * mm});
            skLineSegment(sketch, "E55.0.1.2", {"start": v(7.62, -13.17) * mm, "end": v(7.62, -13.3) * mm});
            skLineSegment(sketch, "E55.0.1.3", {"start": v(7.62, -13.17) * mm, "end": v(7.62, -13.05) * mm});
            skLineSegment(sketch, "E55.0.2.0", {"start": v(7.62, -23.05) * mm, "end": v(12.7, -23.05) * mm});
            skLineSegment(sketch, "E55.0.2.1", {"start": v(7.62, -23.3) * mm, "end": v(12.7, -23.3) * mm});
            skLineSegment(sketch, "E55.0.2.2", {"start": v(7.62, -23.17) * mm, "end": v(7.62, -23.3) * mm});
            skLineSegment(sketch, "E55.0.2.3", {"start": v(7.62, -23.17) * mm, "end": v(7.62, -23.05) * mm});
            skLineSegment(sketch, "E55.0.3.0", {"start": v(7.62, -33.05) * mm, "end": v(12.7, -33.05) * mm});
            skLineSegment(sketch, "E55.0.3.1", {"start": v(7.62, -33.3) * mm, "end": v(12.7, -33.3) * mm});
            skLineSegment(sketch, "E55.0.3.2", {"start": v(7.62, -33.17) * mm, "end": v(7.62, -33.3) * mm});
            skLineSegment(sketch, "E55.0.3.3", {"start": v(7.62, -33.17) * mm, "end": v(7.62, -33.05) * mm});
            skLineSegment(sketch, "E55.0.4.0", {"start": v(7.62, -43.05) * mm, "end": v(12.7, -43.05) * mm});
            skLineSegment(sketch, "E55.0.4.1", {"start": v(7.62, -43.3) * mm, "end": v(12.7, -43.3) * mm});
            skLineSegment(sketch, "E55.0.4.2", {"start": v(7.62, -43.17) * mm, "end": v(7.62, -43.3) * mm});
            skLineSegment(sketch, "E55.0.4.3", {"start": v(7.62, -43.17) * mm, "end": v(7.62, -43.05) * mm});
            skLineSegment(sketch, "E55.0.5.0", {"start": v(7.62, -53.05) * mm, "end": v(12.7, -53.05) * mm});
            skLineSegment(sketch, "E55.0.5.1", {"start": v(7.62, -53.3) * mm, "end": v(12.7, -53.3) * mm});
            skLineSegment(sketch, "E55.0.5.2", {"start": v(7.62, -53.17) * mm, "end": v(7.62, -53.3) * mm});
            skLineSegment(sketch, "E55.0.5.3", {"start": v(7.62, -53.17) * mm, "end": v(7.62, -53.05) * mm});
            skLineSegment(sketch, "E55.0.6.0", {"start": v(7.62, -63.05) * mm, "end": v(12.7, -63.05) * mm});
            skLineSegment(sketch, "E55.0.6.1", {"start": v(7.62, -63.3) * mm, "end": v(12.7, -63.3) * mm});
            skLineSegment(sketch, "E55.0.6.2", {"start": v(7.62, -63.17) * mm, "end": v(7.62, -63.3) * mm});
            skLineSegment(sketch, "E55.0.6.3", {"start": v(7.62, -63.17) * mm, "end": v(7.62, -63.05) * mm});
            skLineSegment(sketch, "E55.0.7.0", {"start": v(7.62, -73.05) * mm, "end": v(12.7, -73.05) * mm});
            skLineSegment(sketch, "E55.0.7.1", {"start": v(7.62, -73.3) * mm, "end": v(12.7, -73.3) * mm});
            skLineSegment(sketch, "E55.0.7.2", {"start": v(7.62, -73.17) * mm, "end": v(7.62, -73.3) * mm});
            skLineSegment(sketch, "E55.0.7.3", {"start": v(7.62, -73.17) * mm, "end": v(7.62, -73.05) * mm});
            skLineSegment(sketch, "E55.0.8.0", {"start": v(7.62, -83.05) * mm, "end": v(12.7, -83.05) * mm});
            skLineSegment(sketch, "E55.0.8.1", {"start": v(7.62, -83.3) * mm, "end": v(12.7, -83.3) * mm});
            skLineSegment(sketch, "E55.0.8.2", {"start": v(7.62, -83.17) * mm, "end": v(7.62, -83.3) * mm});
            skLineSegment(sketch, "E55.0.8.3", {"start": v(7.62, -83.17) * mm, "end": v(7.62, -83.05) * mm});
            skLineSegment(sketch, "E55.0.9.0", {"start": v(7.62, -93.05) * mm, "end": v(12.7, -93.05) * mm});
            skLineSegment(sketch, "E55.0.9.1", {"start": v(7.62, -93.3) * mm, "end": v(12.7, -93.3) * mm});
            skLineSegment(sketch, "E55.0.9.2", {"start": v(7.62, -93.17) * mm, "end": v(7.62, -93.3) * mm});
            skLineSegment(sketch, "E55.0.9.3", {"start": v(7.62, -93.17) * mm, "end": v(7.62, -93.05) * mm});
            skLineSegment(sketch, "E55.0.10.0", {"start": v(7.62, -103.05) * mm, "end": v(12.7, -103.05) * mm});
            skLineSegment(sketch, "E55.0.10.1", {"start": v(7.62, -103.3) * mm, "end": v(12.7, -103.3) * mm});
            skLineSegment(sketch, "E55.0.10.2", {"start": v(7.62, -103.17) * mm, "end": v(7.62, -103.3) * mm});
            skLineSegment(sketch, "E55.0.10.3", {"start": v(7.62, -103.17) * mm, "end": v(7.62, -103.05) * mm});
            skLineSegment(sketch, "E55.0.11.0", {"start": v(7.62, -113.05) * mm, "end": v(12.7, -113.05) * mm});
            skLineSegment(sketch, "E55.0.11.1", {"start": v(7.62, -113.3) * mm, "end": v(12.7, -113.3) * mm});
            skLineSegment(sketch, "E55.0.11.2", {"start": v(7.62, -113.17) * mm, "end": v(7.62, -113.3) * mm});
            skLineSegment(sketch, "E55.0.11.3", {"start": v(7.62, -113.17) * mm, "end": v(7.62, -113.05) * mm});
            skLineSegment(sketch, "E55.0.12.0", {"start": v(7.62, -123.05) * mm, "end": v(12.7, -123.05) * mm});
            skLineSegment(sketch, "E55.0.12.1", {"start": v(7.62, -123.3) * mm, "end": v(12.7, -123.3) * mm});
            skLineSegment(sketch, "E55.0.12.2", {"start": v(7.62, -123.17) * mm, "end": v(7.62, -123.3) * mm});
            skLineSegment(sketch, "E55.0.12.3", {"start": v(7.62, -123.17) * mm, "end": v(7.62, -123.05) * mm});
            skLineSegment(sketch, "E55.0.13.0", {"start": v(7.62, -133.05) * mm, "end": v(12.7, -133.05) * mm});
            skLineSegment(sketch, "E55.0.13.1", {"start": v(7.62, -133.3) * mm, "end": v(12.7, -133.3) * mm});
            skLineSegment(sketch, "E55.0.13.2", {"start": v(7.62, -133.17) * mm, "end": v(7.62, -133.3) * mm});
            skLineSegment(sketch, "E55.0.13.3", {"start": v(7.62, -133.17) * mm, "end": v(7.62, -133.05) * mm});
            skLineSegment(sketch, "E55.0.14.0", {"start": v(7.62, -143.05) * mm, "end": v(12.7, -143.05) * mm});
            skLineSegment(sketch, "E55.0.14.1", {"start": v(7.62, -143.3) * mm, "end": v(12.7, -143.3) * mm});
            skLineSegment(sketch, "E55.0.14.2", {"start": v(7.62, -143.17) * mm, "end": v(7.62, -143.3) * mm});
            skLineSegment(sketch, "E55.0.14.3", {"start": v(7.62, -143.17) * mm, "end": v(7.62, -143.05) * mm});
            skLineSegment(sketch, "E55.0.15.0", {"start": v(7.62, -153.05) * mm, "end": v(12.7, -153.05) * mm});
            skLineSegment(sketch, "E55.0.15.1", {"start": v(7.62, -153.3) * mm, "end": v(12.7, -153.3) * mm});
            skLineSegment(sketch, "E55.0.15.2", {"start": v(7.62, -153.17) * mm, "end": v(7.62, -153.3) * mm});
            skLineSegment(sketch, "E55.0.15.3", {"start": v(7.62, -153.17) * mm, "end": v(7.62, -153.05) * mm});
            skLineSegment(sketch, "E55.0.16.0", {"start": v(7.62, -163.05) * mm, "end": v(12.7, -163.05) * mm});
            skLineSegment(sketch, "E55.0.16.1", {"start": v(7.62, -163.3) * mm, "end": v(12.7, -163.3) * mm});
            skLineSegment(sketch, "E55.0.16.2", {"start": v(7.62, -163.17) * mm, "end": v(7.62, -163.3) * mm});
            skLineSegment(sketch, "E55.0.16.3", {"start": v(7.62, -163.17) * mm, "end": v(7.62, -163.05) * mm});
            skLineSegment(sketch, "E55.0.17.0", {"start": v(7.62, -173.05) * mm, "end": v(12.7, -173.05) * mm});
            skLineSegment(sketch, "E55.0.17.1", {"start": v(7.62, -173.3) * mm, "end": v(12.7, -173.3) * mm});
            skLineSegment(sketch, "E55.0.17.2", {"start": v(7.62, -173.17) * mm, "end": v(7.62, -173.3) * mm});
            skLineSegment(sketch, "E55.0.17.3", {"start": v(7.62, -173.17) * mm, "end": v(7.62, -173.05) * mm});
            skLineSegment(sketch, "E55.0.18.0", {"start": v(7.62, -183.05) * mm, "end": v(12.7, -183.05) * mm});
            skLineSegment(sketch, "E55.0.18.1", {"start": v(7.62, -183.3) * mm, "end": v(12.7, -183.3) * mm});
            skLineSegment(sketch, "E55.0.18.2", {"start": v(7.62, -183.17) * mm, "end": v(7.62, -183.3) * mm});
            skLineSegment(sketch, "E55.0.18.3", {"start": v(7.62, -183.17) * mm, "end": v(7.62, -183.05) * mm});
            skLineSegment(sketch, "E55.0.19.0", {"start": v(7.62, -193.05) * mm, "end": v(12.7, -193.05) * mm});
            skLineSegment(sketch, "E55.0.19.1", {"start": v(7.62, -193.3) * mm, "end": v(12.7, -193.3) * mm});
            skLineSegment(sketch, "E55.0.19.2", {"start": v(7.62, -193.17) * mm, "end": v(7.62, -193.3) * mm});
            skLineSegment(sketch, "E55.0.19.3", {"start": v(7.62, -193.17) * mm, "end": v(7.62, -193.05) * mm});
            skLineSegment(sketch, "E55.0.20.0", {"start": v(7.62, -203.05) * mm, "end": v(12.7, -203.05) * mm});
            skLineSegment(sketch, "E55.0.20.1", {"start": v(7.62, -203.3) * mm, "end": v(12.7, -203.3) * mm});
            skLineSegment(sketch, "E55.0.20.2", {"start": v(7.62, -203.17) * mm, "end": v(7.62, -203.3) * mm});
            skLineSegment(sketch, "E55.0.20.3", {"start": v(7.62, -203.17) * mm, "end": v(7.62, -203.05) * mm});
            skLineSegment(sketch, "E55.0.21.0", {"start": v(7.62, -213.05) * mm, "end": v(12.7, -213.05) * mm});
            skLineSegment(sketch, "E55.0.21.1", {"start": v(7.62, -213.3) * mm, "end": v(12.7, -213.3) * mm});
            skLineSegment(sketch, "E55.0.21.2", {"start": v(7.62, -213.17) * mm, "end": v(7.62, -213.3) * mm});
            skLineSegment(sketch, "E55.0.21.3", {"start": v(7.62, -213.17) * mm, "end": v(7.62, -213.05) * mm});
            skLineSegment(sketch, "E55.0.22.0", {"start": v(7.62, -223.05) * mm, "end": v(12.7, -223.05) * mm});
            skLineSegment(sketch, "E55.0.22.1", {"start": v(7.62, -223.3) * mm, "end": v(12.7, -223.3) * mm});
            skLineSegment(sketch, "E55.0.22.2", {"start": v(7.62, -223.17) * mm, "end": v(7.62, -223.3) * mm});
            skLineSegment(sketch, "E55.0.22.3", {"start": v(7.62, -223.17) * mm, "end": v(7.62, -223.05) * mm});
            skLineSegment(sketch, "E55.0.23.0", {"start": v(7.62, -233.05) * mm, "end": v(12.7, -233.05) * mm});
            skLineSegment(sketch, "E55.0.23.1", {"start": v(7.62, -233.3) * mm, "end": v(12.7, -233.3) * mm});
            skLineSegment(sketch, "E55.0.23.2", {"start": v(7.62, -233.17) * mm, "end": v(7.62, -233.3) * mm});
            skLineSegment(sketch, "E55.0.23.3", {"start": v(7.62, -233.17) * mm, "end": v(7.62, -233.05) * mm});
            skLineSegment(sketch, "E55.0.24.0", {"start": v(7.62, -243.05) * mm, "end": v(12.7, -243.05) * mm});
            skLineSegment(sketch, "E55.0.24.1", {"start": v(7.62, -243.3) * mm, "end": v(12.7, -243.3) * mm});
            skLineSegment(sketch, "E55.0.24.2", {"start": v(7.62, -243.17) * mm, "end": v(7.62, -243.3) * mm});
            skLineSegment(sketch, "E55.0.24.3", {"start": v(7.62, -243.17) * mm, "end": v(7.62, -243.05) * mm});
            skLineSegment(sketch, "E55.0.25.0", {"start": v(7.62, -253.05) * mm, "end": v(12.7, -253.05) * mm});
            skLineSegment(sketch, "E55.0.25.1", {"start": v(7.62, -253.3) * mm, "end": v(12.7, -253.3) * mm});
            skLineSegment(sketch, "E55.0.25.2", {"start": v(7.62, -253.17) * mm, "end": v(7.62, -253.3) * mm});
            skLineSegment(sketch, "E55.0.25.3", {"start": v(7.62, -253.17) * mm, "end": v(7.62, -253.05) * mm});
            skLineSegment(sketch, "E55.0.26.0", {"start": v(7.62, -263.05) * mm, "end": v(12.7, -263.05) * mm});
            skLineSegment(sketch, "E55.0.26.1", {"start": v(7.62, -263.3) * mm, "end": v(12.7, -263.3) * mm});
            skLineSegment(sketch, "E55.0.26.2", {"start": v(7.62, -263.17) * mm, "end": v(7.62, -263.3) * mm});
            skLineSegment(sketch, "E55.0.26.3", {"start": v(7.62, -263.18) * mm, "end": v(7.62, -263.05) * mm});
            skLineSegment(sketch, "E55.0.27.0", {"start": v(7.62, -273.05) * mm, "end": v(12.7, -273.05) * mm});
            skLineSegment(sketch, "E55.0.27.1", {"start": v(7.62, -273.3) * mm, "end": v(12.7, -273.3) * mm});
            skLineSegment(sketch, "E55.0.27.2", {"start": v(7.62, -273.17) * mm, "end": v(7.62, -273.3) * mm});
            skLineSegment(sketch, "E55.0.27.3", {"start": v(7.62, -273.18) * mm, "end": v(7.62, -273.05) * mm});
            skLineSegment(sketch, "E55.0.28.0", {"start": v(7.62, -283.05) * mm, "end": v(12.7, -283.05) * mm});
            skLineSegment(sketch, "E55.0.28.1", {"start": v(7.62, -283.3) * mm, "end": v(12.7, -283.3) * mm});
            skLineSegment(sketch, "E55.0.28.2", {"start": v(7.62, -283.17) * mm, "end": v(7.62, -283.3) * mm});
            skLineSegment(sketch, "E55.0.28.3", {"start": v(7.62, -283.18) * mm, "end": v(7.62, -283.05) * mm});
            skLineSegment(sketch, "E55.0.29.0", {"start": v(7.62, -293.05) * mm, "end": v(12.7, -293.05) * mm});
            skLineSegment(sketch, "E55.0.29.1", {"start": v(7.62, -293.3) * mm, "end": v(12.7, -293.3) * mm});
            skLineSegment(sketch, "E55.0.29.2", {"start": v(7.62, -293.17) * mm, "end": v(7.62, -293.3) * mm});
            skLineSegment(sketch, "E55.0.29.3", {"start": v(7.62, -293.18) * mm, "end": v(7.62, -293.05) * mm});
            skLineSegment(sketch, "E55.0.30.0", {"start": v(7.62, -303.05) * mm, "end": v(12.7, -303.05) * mm});
            skLineSegment(sketch, "E55.0.30.1", {"start": v(7.62, -303.3) * mm, "end": v(12.7, -303.3) * mm});
            skLineSegment(sketch, "E55.0.30.2", {"start": v(7.62, -303.17) * mm, "end": v(7.62, -303.3) * mm});
            skLineSegment(sketch, "E55.0.30.3", {"start": v(7.62, -303.17) * mm, "end": v(7.62, -303.05) * mm});
            skLineSegment(sketch, "E55.direction1", {"start": v(7.62, -3.05) * mm, "end": v(33.02, -3.05) * mm, "construction": true});
            skLineSegment(sketch, "E55.direction2", {"start": v(7.62, -3.05) * mm, "end": v(7.62, -3.3) * mm, "construction": true});
            skPoint(sketch, "E56.startSnap0", {"position": v(7.62, -8.05) * mm});
            skLineSegment(sketch, "E57", {"start": v(10.16, -8.05) * mm, "end": v(10.16, -7.92) * mm});
            skLineSegment(sketch, "E58", {"start": v(10.16, -8.05) * mm, "end": v(10.16, -8.18) * mm});
            skLineSegment(sketch, "E59", {"start": v(10.16, -7.92) * mm, "end": v(12.7, -7.92) * mm});
            skLineSegment(sketch, "E60", {"start": v(10.16, -8.18) * mm, "end": v(12.7, -8.18) * mm});
            skPoint(sketch, "E56.end.orphan", {"position": v(12.7, -8.05) * mm});
            skLineSegment(sketch, "E61.0.1.0", {"start": v(10.16, -17.92) * mm, "end": v(12.7, -17.92) * mm});
            skLineSegment(sketch, "E61.0.1.1", {"start": v(10.16, -18.05) * mm, "end": v(10.16, -17.92) * mm});
            skLineSegment(sketch, "E61.0.1.2", {"start": v(10.16, -18.05) * mm, "end": v(10.16, -18.18) * mm});
            skLineSegment(sketch, "E61.0.1.3", {"start": v(10.16, -18.18) * mm, "end": v(12.7, -18.18) * mm});
            skLineSegment(sketch, "E61.0.2.0", {"start": v(10.16, -27.92) * mm, "end": v(12.7, -27.92) * mm});
            skLineSegment(sketch, "E61.0.2.1", {"start": v(10.16, -28.05) * mm, "end": v(10.16, -27.92) * mm});
            skLineSegment(sketch, "E61.0.2.2", {"start": v(10.16, -28.05) * mm, "end": v(10.16, -28.18) * mm});
            skLineSegment(sketch, "E61.0.2.3", {"start": v(10.16, -28.18) * mm, "end": v(12.7, -28.18) * mm});
            skLineSegment(sketch, "E61.0.3.0", {"start": v(10.16, -37.92) * mm, "end": v(12.7, -37.92) * mm});
            skLineSegment(sketch, "E61.0.3.1", {"start": v(10.16, -38.05) * mm, "end": v(10.16, -37.92) * mm});
            skLineSegment(sketch, "E61.0.3.2", {"start": v(10.16, -38.05) * mm, "end": v(10.16, -38.18) * mm});
            skLineSegment(sketch, "E61.0.3.3", {"start": v(10.16, -38.18) * mm, "end": v(12.7, -38.18) * mm});
            skLineSegment(sketch, "E61.0.4.0", {"start": v(10.16, -47.92) * mm, "end": v(12.7, -47.92) * mm});
            skLineSegment(sketch, "E61.0.4.1", {"start": v(10.16, -48.05) * mm, "end": v(10.16, -47.92) * mm});
            skLineSegment(sketch, "E61.0.4.2", {"start": v(10.16, -48.05) * mm, "end": v(10.16, -48.18) * mm});
            skLineSegment(sketch, "E61.0.4.3", {"start": v(10.16, -48.18) * mm, "end": v(12.7, -48.18) * mm});
            skLineSegment(sketch, "E61.0.5.0", {"start": v(10.16, -57.92) * mm, "end": v(12.7, -57.92) * mm});
            skLineSegment(sketch, "E61.0.5.1", {"start": v(10.16, -58.05) * mm, "end": v(10.16, -57.92) * mm});
            skLineSegment(sketch, "E61.0.5.2", {"start": v(10.16, -58.05) * mm, "end": v(10.16, -58.18) * mm});
            skLineSegment(sketch, "E61.0.5.3", {"start": v(10.16, -58.18) * mm, "end": v(12.7, -58.18) * mm});
            skLineSegment(sketch, "E61.0.6.0", {"start": v(10.16, -67.92) * mm, "end": v(12.7, -67.92) * mm});
            skLineSegment(sketch, "E61.0.6.1", {"start": v(10.16, -68.05) * mm, "end": v(10.16, -67.92) * mm});
            skLineSegment(sketch, "E61.0.6.2", {"start": v(10.16, -68.05) * mm, "end": v(10.16, -68.18) * mm});
            skLineSegment(sketch, "E61.0.6.3", {"start": v(10.16, -68.18) * mm, "end": v(12.7, -68.18) * mm});
            skLineSegment(sketch, "E61.0.7.0", {"start": v(10.16, -77.92) * mm, "end": v(12.7, -77.92) * mm});
            skLineSegment(sketch, "E61.0.7.1", {"start": v(10.16, -78.05) * mm, "end": v(10.16, -77.92) * mm});
            skLineSegment(sketch, "E61.0.7.2", {"start": v(10.16, -78.05) * mm, "end": v(10.16, -78.18) * mm});
            skLineSegment(sketch, "E61.0.7.3", {"start": v(10.16, -78.18) * mm, "end": v(12.7, -78.18) * mm});
            skLineSegment(sketch, "E61.0.8.0", {"start": v(10.16, -87.92) * mm, "end": v(12.7, -87.92) * mm});
            skLineSegment(sketch, "E61.0.8.1", {"start": v(10.16, -88.05) * mm, "end": v(10.16, -87.92) * mm});
            skLineSegment(sketch, "E61.0.8.2", {"start": v(10.16, -88.05) * mm, "end": v(10.16, -88.18) * mm});
            skLineSegment(sketch, "E61.0.8.3", {"start": v(10.16, -88.18) * mm, "end": v(12.7, -88.18) * mm});
            skLineSegment(sketch, "E61.0.9.0", {"start": v(10.16, -97.92) * mm, "end": v(12.7, -97.92) * mm});
            skLineSegment(sketch, "E61.0.9.1", {"start": v(10.16, -98.05) * mm, "end": v(10.16, -97.92) * mm});
            skLineSegment(sketch, "E61.0.9.2", {"start": v(10.16, -98.05) * mm, "end": v(10.16, -98.18) * mm});
            skLineSegment(sketch, "E61.0.9.3", {"start": v(10.16, -98.18) * mm, "end": v(12.7, -98.18) * mm});
            skLineSegment(sketch, "E61.0.10.0", {"start": v(10.16, -107.92) * mm, "end": v(12.7, -107.92) * mm});
            skLineSegment(sketch, "E61.0.10.1", {"start": v(10.16, -108.05) * mm, "end": v(10.16, -107.92) * mm});
            skLineSegment(sketch, "E61.0.10.2", {"start": v(10.16, -108.05) * mm, "end": v(10.16, -108.18) * mm});
            skLineSegment(sketch, "E61.0.10.3", {"start": v(10.16, -108.18) * mm, "end": v(12.7, -108.18) * mm});
            skLineSegment(sketch, "E61.0.11.0", {"start": v(10.16, -117.92) * mm, "end": v(12.7, -117.92) * mm});
            skLineSegment(sketch, "E61.0.11.1", {"start": v(10.16, -118.05) * mm, "end": v(10.16, -117.92) * mm});
            skLineSegment(sketch, "E61.0.11.2", {"start": v(10.16, -118.05) * mm, "end": v(10.16, -118.18) * mm});
            skLineSegment(sketch, "E61.0.11.3", {"start": v(10.16, -118.18) * mm, "end": v(12.7, -118.18) * mm});
            skLineSegment(sketch, "E61.0.12.0", {"start": v(10.16, -127.92) * mm, "end": v(12.7, -127.92) * mm});
            skLineSegment(sketch, "E61.0.12.1", {"start": v(10.16, -128.05) * mm, "end": v(10.16, -127.92) * mm});
            skLineSegment(sketch, "E61.0.12.2", {"start": v(10.16, -128.05) * mm, "end": v(10.16, -128.18) * mm});
            skLineSegment(sketch, "E61.0.12.3", {"start": v(10.16, -128.18) * mm, "end": v(12.7, -128.18) * mm});
            skLineSegment(sketch, "E61.0.13.0", {"start": v(10.16, -137.92) * mm, "end": v(12.7, -137.92) * mm});
            skLineSegment(sketch, "E61.0.13.1", {"start": v(10.16, -138.05) * mm, "end": v(10.16, -137.92) * mm});
            skLineSegment(sketch, "E61.0.13.2", {"start": v(10.16, -138.05) * mm, "end": v(10.16, -138.18) * mm});
            skLineSegment(sketch, "E61.0.13.3", {"start": v(10.16, -138.18) * mm, "end": v(12.7, -138.18) * mm});
            skLineSegment(sketch, "E61.0.14.0", {"start": v(10.16, -147.92) * mm, "end": v(12.7, -147.92) * mm});
            skLineSegment(sketch, "E61.0.14.1", {"start": v(10.16, -148.05) * mm, "end": v(10.16, -147.92) * mm});
            skLineSegment(sketch, "E61.0.14.2", {"start": v(10.16, -148.05) * mm, "end": v(10.16, -148.18) * mm});
            skLineSegment(sketch, "E61.0.14.3", {"start": v(10.16, -148.18) * mm, "end": v(12.7, -148.18) * mm});
            skLineSegment(sketch, "E61.0.15.0", {"start": v(10.16, -157.92) * mm, "end": v(12.7, -157.92) * mm});
            skLineSegment(sketch, "E61.0.15.1", {"start": v(10.16, -158.05) * mm, "end": v(10.16, -157.92) * mm});
            skLineSegment(sketch, "E61.0.15.2", {"start": v(10.16, -158.05) * mm, "end": v(10.16, -158.18) * mm});
            skLineSegment(sketch, "E61.0.15.3", {"start": v(10.16, -158.18) * mm, "end": v(12.7, -158.18) * mm});
            skLineSegment(sketch, "E61.0.16.0", {"start": v(10.16, -167.92) * mm, "end": v(12.7, -167.92) * mm});
            skLineSegment(sketch, "E61.0.16.1", {"start": v(10.16, -168.05) * mm, "end": v(10.16, -167.92) * mm});
            skLineSegment(sketch, "E61.0.16.2", {"start": v(10.16, -168.05) * mm, "end": v(10.16, -168.18) * mm});
            skLineSegment(sketch, "E61.0.16.3", {"start": v(10.16, -168.18) * mm, "end": v(12.7, -168.18) * mm});
            skLineSegment(sketch, "E61.0.17.0", {"start": v(10.16, -177.92) * mm, "end": v(12.7, -177.92) * mm});
            skLineSegment(sketch, "E61.0.17.1", {"start": v(10.16, -178.05) * mm, "end": v(10.16, -177.92) * mm});
            skLineSegment(sketch, "E61.0.17.2", {"start": v(10.16, -178.05) * mm, "end": v(10.16, -178.18) * mm});
            skLineSegment(sketch, "E61.0.17.3", {"start": v(10.16, -178.18) * mm, "end": v(12.7, -178.18) * mm});
            skLineSegment(sketch, "E61.0.18.0", {"start": v(10.16, -187.92) * mm, "end": v(12.7, -187.92) * mm});
            skLineSegment(sketch, "E61.0.18.1", {"start": v(10.16, -188.05) * mm, "end": v(10.16, -187.92) * mm});
            skLineSegment(sketch, "E61.0.18.2", {"start": v(10.16, -188.05) * mm, "end": v(10.16, -188.18) * mm});
            skLineSegment(sketch, "E61.0.18.3", {"start": v(10.16, -188.18) * mm, "end": v(12.7, -188.18) * mm});
            skLineSegment(sketch, "E61.0.19.0", {"start": v(10.16, -197.92) * mm, "end": v(12.7, -197.92) * mm});
            skLineSegment(sketch, "E61.0.19.1", {"start": v(10.16, -198.05) * mm, "end": v(10.16, -197.92) * mm});
            skLineSegment(sketch, "E61.0.19.2", {"start": v(10.16, -198.05) * mm, "end": v(10.16, -198.18) * mm});
            skLineSegment(sketch, "E61.0.19.3", {"start": v(10.16, -198.18) * mm, "end": v(12.7, -198.18) * mm});
            skLineSegment(sketch, "E61.0.20.0", {"start": v(10.16, -207.92) * mm, "end": v(12.7, -207.92) * mm});
            skLineSegment(sketch, "E61.0.20.1", {"start": v(10.16, -208.05) * mm, "end": v(10.16, -207.92) * mm});
            skLineSegment(sketch, "E61.0.20.2", {"start": v(10.16, -208.05) * mm, "end": v(10.16, -208.18) * mm});
            skLineSegment(sketch, "E61.0.20.3", {"start": v(10.16, -208.18) * mm, "end": v(12.7, -208.18) * mm});
            skLineSegment(sketch, "E61.0.21.0", {"start": v(10.16, -217.92) * mm, "end": v(12.7, -217.92) * mm});
            skLineSegment(sketch, "E61.0.21.1", {"start": v(10.16, -218.05) * mm, "end": v(10.16, -217.92) * mm});
            skLineSegment(sketch, "E61.0.21.2", {"start": v(10.16, -218.05) * mm, "end": v(10.16, -218.18) * mm});
            skLineSegment(sketch, "E61.0.21.3", {"start": v(10.16, -218.18) * mm, "end": v(12.7, -218.18) * mm});
            skLineSegment(sketch, "E61.0.22.0", {"start": v(10.16, -227.92) * mm, "end": v(12.7, -227.92) * mm});
            skLineSegment(sketch, "E61.0.22.1", {"start": v(10.16, -228.05) * mm, "end": v(10.16, -227.92) * mm});
            skLineSegment(sketch, "E61.0.22.2", {"start": v(10.16, -228.05) * mm, "end": v(10.16, -228.18) * mm});
            skLineSegment(sketch, "E61.0.22.3", {"start": v(10.16, -228.18) * mm, "end": v(12.7, -228.18) * mm});
            skLineSegment(sketch, "E61.0.23.0", {"start": v(10.16, -237.92) * mm, "end": v(12.7, -237.92) * mm});
            skLineSegment(sketch, "E61.0.23.1", {"start": v(10.16, -238.05) * mm, "end": v(10.16, -237.92) * mm});
            skLineSegment(sketch, "E61.0.23.2", {"start": v(10.16, -238.05) * mm, "end": v(10.16, -238.18) * mm});
            skLineSegment(sketch, "E61.0.23.3", {"start": v(10.16, -238.18) * mm, "end": v(12.7, -238.18) * mm});
            skLineSegment(sketch, "E61.0.24.0", {"start": v(10.16, -247.92) * mm, "end": v(12.7, -247.92) * mm});
            skLineSegment(sketch, "E61.0.24.1", {"start": v(10.16, -248.05) * mm, "end": v(10.16, -247.92) * mm});
            skLineSegment(sketch, "E61.0.24.2", {"start": v(10.16, -248.05) * mm, "end": v(10.16, -248.18) * mm});
            skLineSegment(sketch, "E61.0.24.3", {"start": v(10.16, -248.18) * mm, "end": v(12.7, -248.18) * mm});
            skLineSegment(sketch, "E61.0.25.0", {"start": v(10.16, -257.92) * mm, "end": v(12.7, -257.92) * mm});
            skLineSegment(sketch, "E61.0.25.1", {"start": v(10.16, -258.05) * mm, "end": v(10.16, -257.92) * mm});
            skLineSegment(sketch, "E61.0.25.2", {"start": v(10.16, -258.05) * mm, "end": v(10.16, -258.18) * mm});
            skLineSegment(sketch, "E61.0.25.3", {"start": v(10.16, -258.18) * mm, "end": v(12.7, -258.18) * mm});
            skLineSegment(sketch, "E61.0.26.0", {"start": v(10.16, -267.92) * mm, "end": v(12.7, -267.92) * mm});
            skLineSegment(sketch, "E61.0.26.1", {"start": v(10.16, -268.05) * mm, "end": v(10.16, -267.92) * mm});
            skLineSegment(sketch, "E61.0.26.2", {"start": v(10.16, -268.05) * mm, "end": v(10.16, -268.18) * mm});
            skLineSegment(sketch, "E61.0.26.3", {"start": v(10.16, -268.18) * mm, "end": v(12.7, -268.18) * mm});
            skLineSegment(sketch, "E61.0.27.0", {"start": v(10.16, -277.92) * mm, "end": v(12.7, -277.92) * mm});
            skLineSegment(sketch, "E61.0.27.1", {"start": v(10.16, -278.05) * mm, "end": v(10.16, -277.92) * mm});
            skLineSegment(sketch, "E61.0.27.2", {"start": v(10.16, -278.05) * mm, "end": v(10.16, -278.18) * mm});
            skLineSegment(sketch, "E61.0.27.3", {"start": v(10.16, -278.18) * mm, "end": v(12.7, -278.18) * mm});
            skLineSegment(sketch, "E61.0.28.0", {"start": v(10.16, -287.92) * mm, "end": v(12.7, -287.92) * mm});
            skLineSegment(sketch, "E61.0.28.1", {"start": v(10.16, -288.05) * mm, "end": v(10.16, -287.92) * mm});
            skLineSegment(sketch, "E61.0.28.2", {"start": v(10.16, -288.05) * mm, "end": v(10.16, -288.18) * mm});
            skLineSegment(sketch, "E61.0.28.3", {"start": v(10.16, -288.18) * mm, "end": v(12.7, -288.18) * mm});
            skLineSegment(sketch, "E61.0.29.0", {"start": v(10.16, -297.92) * mm, "end": v(12.7, -297.92) * mm});
            skLineSegment(sketch, "E61.0.29.1", {"start": v(10.16, -298.05) * mm, "end": v(10.16, -297.92) * mm});
            skLineSegment(sketch, "E61.0.29.2", {"start": v(10.16, -298.05) * mm, "end": v(10.16, -298.18) * mm});
            skLineSegment(sketch, "E61.0.29.3", {"start": v(10.16, -298.18) * mm, "end": v(12.7, -298.18) * mm});
            skLineSegment(sketch, "E61.0.30.0", {"start": v(10.16, -307.92) * mm, "end": v(12.7, -307.92) * mm});
            skLineSegment(sketch, "E61.0.30.1", {"start": v(10.16, -308.05) * mm, "end": v(10.16, -307.92) * mm});
            skLineSegment(sketch, "E61.0.30.2", {"start": v(10.16, -308.05) * mm, "end": v(10.16, -308.18) * mm});
            skLineSegment(sketch, "E61.0.30.3", {"start": v(10.16, -308.18) * mm, "end": v(12.7, -308.18) * mm});
            skLineSegment(sketch, "E61.direction1", {"start": v(10.16, -7.92) * mm, "end": v(35.56, -7.92) * mm, "construction": true});
            skLineSegment(sketch, "E61.direction2", {"start": v(10.16, -7.92) * mm, "end": v(10.16, -17.92) * mm, "construction": true});
            skLineSegment(sketch, "E62.trimOffspring", {"start": v(7.62, -13.05) * mm, "end": v(7.62, -13.17) * mm});
            skLineSegment(sketch, "E63", {"start": v(7.62, -4.18) * mm, "end": v(7.62, -4.05) * mm});
            skLineSegment(sketch, "E64.trimOffspring", {"start": v(7.62, -4.05) * mm, "end": v(7.62, -4.18) * mm});
            skLineSegment(sketch, "E65", {"start": v(12.7, -4.05) * mm, "end": v(11.43, -4.05) * mm});
            skLineSegment(sketch, "E66", {"start": v(11.43, -4.05) * mm, "end": v(11.43, -4.3) * mm});
            skLineSegment(sketch, "E67", {"start": v(11.43, -4.3) * mm, "end": v(12.7, -4.3) * mm});
            skLineSegment(sketch, "E68.0.1.0", {"start": v(12.7, -5.05) * mm, "end": v(11.43, -5.05) * mm});
            skLineSegment(sketch, "E68.0.1.1", {"start": v(11.43, -5.3) * mm, "end": v(12.7, -5.3) * mm});
            skLineSegment(sketch, "E68.0.1.2", {"start": v(11.43, -5.05) * mm, "end": v(11.43, -5.3) * mm});
            skLineSegment(sketch, "E68.0.2.0", {"start": v(12.7, -6.05) * mm, "end": v(11.43, -6.05) * mm});
            skLineSegment(sketch, "E68.0.2.1", {"start": v(11.43, -6.3) * mm, "end": v(12.7, -6.3) * mm});
            skLineSegment(sketch, "E68.0.2.2", {"start": v(11.43, -6.05) * mm, "end": v(11.43, -6.3) * mm});
            skLineSegment(sketch, "E68.0.3.0", {"start": v(12.7, -7.05) * mm, "end": v(11.43, -7.05) * mm});
            skLineSegment(sketch, "E68.0.3.1", {"start": v(11.43, -7.3) * mm, "end": v(12.7, -7.3) * mm});
            skLineSegment(sketch, "E68.0.3.2", {"start": v(11.43, -7.05) * mm, "end": v(11.43, -7.3) * mm});
            skLineSegment(sketch, "E68.0.4.0", {"start": v(12.7, -8.05) * mm, "end": v(11.43, -8.05) * mm});
            skLineSegment(sketch, "E68.0.4.1", {"start": v(11.43, -8.3) * mm, "end": v(12.7, -8.3) * mm});
            skLineSegment(sketch, "E68.0.4.2", {"start": v(11.43, -8.05) * mm, "end": v(11.43, -8.3) * mm});
            skLineSegment(sketch, "E68.0.5.0", {"start": v(12.7, -9.05) * mm, "end": v(11.43, -9.05) * mm});
            skLineSegment(sketch, "E68.0.5.1", {"start": v(11.43, -9.3) * mm, "end": v(12.7, -9.3) * mm});
            skLineSegment(sketch, "E68.0.5.2", {"start": v(11.43, -9.05) * mm, "end": v(11.43, -9.3) * mm});
            skLineSegment(sketch, "E68.0.6.0", {"start": v(12.7, -10.05) * mm, "end": v(11.43, -10.05) * mm});
            skLineSegment(sketch, "E68.0.6.1", {"start": v(11.43, -10.3) * mm, "end": v(12.7, -10.3) * mm});
            skLineSegment(sketch, "E68.0.6.2", {"start": v(11.43, -10.05) * mm, "end": v(11.43, -10.3) * mm});
            skLineSegment(sketch, "E68.0.7.0", {"start": v(12.7, -11.05) * mm, "end": v(11.43, -11.05) * mm});
            skLineSegment(sketch, "E68.0.7.1", {"start": v(11.43, -11.3) * mm, "end": v(12.7, -11.3) * mm});
            skLineSegment(sketch, "E68.0.7.2", {"start": v(11.43, -11.05) * mm, "end": v(11.43, -11.3) * mm});
            skLineSegment(sketch, "E68.0.8.0", {"start": v(12.7, -12.05) * mm, "end": v(11.43, -12.05) * mm});
            skLineSegment(sketch, "E68.0.8.1", {"start": v(11.43, -12.3) * mm, "end": v(12.7, -12.3) * mm});
            skLineSegment(sketch, "E68.0.8.2", {"start": v(11.43, -12.05) * mm, "end": v(11.43, -12.3) * mm});
            skLineSegment(sketch, "E68.0.9.0", {"start": v(12.7, -13.05) * mm, "end": v(11.43, -13.05) * mm});
            skLineSegment(sketch, "E68.0.9.1", {"start": v(11.43, -13.3) * mm, "end": v(12.7, -13.3) * mm});
            skLineSegment(sketch, "E68.0.9.2", {"start": v(11.43, -13.05) * mm, "end": v(11.43, -13.3) * mm});
            skLineSegment(sketch, "E68.0.10.0", {"start": v(12.7, -14.05) * mm, "end": v(11.43, -14.05) * mm});
            skLineSegment(sketch, "E68.0.10.1", {"start": v(11.43, -14.3) * mm, "end": v(12.7, -14.3) * mm});
            skLineSegment(sketch, "E68.0.10.2", {"start": v(11.43, -14.05) * mm, "end": v(11.43, -14.3) * mm});
            skLineSegment(sketch, "E68.0.11.0", {"start": v(12.7, -15.05) * mm, "end": v(11.43, -15.05) * mm});
            skLineSegment(sketch, "E68.0.11.1", {"start": v(11.43, -15.3) * mm, "end": v(12.7, -15.3) * mm});
            skLineSegment(sketch, "E68.0.11.2", {"start": v(11.43, -15.05) * mm, "end": v(11.43, -15.3) * mm});
            skLineSegment(sketch, "E68.0.12.0", {"start": v(12.7, -16.05) * mm, "end": v(11.43, -16.05) * mm});
            skLineSegment(sketch, "E68.0.12.1", {"start": v(11.43, -16.3) * mm, "end": v(12.7, -16.3) * mm});
            skLineSegment(sketch, "E68.0.12.2", {"start": v(11.43, -16.05) * mm, "end": v(11.43, -16.3) * mm});
            skLineSegment(sketch, "E68.0.13.0", {"start": v(12.7, -17.05) * mm, "end": v(11.43, -17.05) * mm});
            skLineSegment(sketch, "E68.0.13.1", {"start": v(11.43, -17.3) * mm, "end": v(12.7, -17.3) * mm});
            skLineSegment(sketch, "E68.0.13.2", {"start": v(11.43, -17.05) * mm, "end": v(11.43, -17.3) * mm});
            skLineSegment(sketch, "E68.0.14.0", {"start": v(12.7, -18.05) * mm, "end": v(11.43, -18.05) * mm});
            skLineSegment(sketch, "E68.0.14.1", {"start": v(11.43, -18.3) * mm, "end": v(12.7, -18.3) * mm});
            skLineSegment(sketch, "E68.0.14.2", {"start": v(11.43, -18.05) * mm, "end": v(11.43, -18.3) * mm});
            skLineSegment(sketch, "E68.0.15.0", {"start": v(12.7, -19.05) * mm, "end": v(11.43, -19.05) * mm});
            skLineSegment(sketch, "E68.0.15.1", {"start": v(11.43, -19.3) * mm, "end": v(12.7, -19.3) * mm});
            skLineSegment(sketch, "E68.0.15.2", {"start": v(11.43, -19.05) * mm, "end": v(11.43, -19.3) * mm});
            skLineSegment(sketch, "E68.0.16.0", {"start": v(12.7, -20.05) * mm, "end": v(11.43, -20.05) * mm});
            skLineSegment(sketch, "E68.0.16.1", {"start": v(11.43, -20.3) * mm, "end": v(12.7, -20.3) * mm});
            skLineSegment(sketch, "E68.0.16.2", {"start": v(11.43, -20.05) * mm, "end": v(11.43, -20.3) * mm});
            skLineSegment(sketch, "E68.0.17.0", {"start": v(12.7, -21.05) * mm, "end": v(11.43, -21.05) * mm});
            skLineSegment(sketch, "E68.0.17.1", {"start": v(11.43, -21.3) * mm, "end": v(12.7, -21.3) * mm});
            skLineSegment(sketch, "E68.0.17.2", {"start": v(11.43, -21.05) * mm, "end": v(11.43, -21.3) * mm});
            skLineSegment(sketch, "E68.0.18.0", {"start": v(12.7, -22.05) * mm, "end": v(11.43, -22.05) * mm});
            skLineSegment(sketch, "E68.0.18.1", {"start": v(11.43, -22.3) * mm, "end": v(12.7, -22.3) * mm});
            skLineSegment(sketch, "E68.0.18.2", {"start": v(11.43, -22.05) * mm, "end": v(11.43, -22.3) * mm});
            skLineSegment(sketch, "E68.0.19.0", {"start": v(12.7, -23.05) * mm, "end": v(11.43, -23.05) * mm});
            skLineSegment(sketch, "E68.0.19.1", {"start": v(11.43, -23.3) * mm, "end": v(12.7, -23.3) * mm});
            skLineSegment(sketch, "E68.0.19.2", {"start": v(11.43, -23.05) * mm, "end": v(11.43, -23.3) * mm});
            skLineSegment(sketch, "E68.0.20.0", {"start": v(12.7, -24.05) * mm, "end": v(11.43, -24.05) * mm});
            skLineSegment(sketch, "E68.0.20.1", {"start": v(11.43, -24.3) * mm, "end": v(12.7, -24.3) * mm});
            skLineSegment(sketch, "E68.0.20.2", {"start": v(11.43, -24.05) * mm, "end": v(11.43, -24.3) * mm});
            skLineSegment(sketch, "E68.0.21.0", {"start": v(12.7, -25.05) * mm, "end": v(11.43, -25.05) * mm});
            skLineSegment(sketch, "E68.0.21.1", {"start": v(11.43, -25.3) * mm, "end": v(12.7, -25.3) * mm});
            skLineSegment(sketch, "E68.0.21.2", {"start": v(11.43, -25.05) * mm, "end": v(11.43, -25.3) * mm});
            skLineSegment(sketch, "E68.0.22.0", {"start": v(12.7, -26.05) * mm, "end": v(11.43, -26.05) * mm});
            skLineSegment(sketch, "E68.0.22.1", {"start": v(11.43, -26.3) * mm, "end": v(12.7, -26.3) * mm});
            skLineSegment(sketch, "E68.0.22.2", {"start": v(11.43, -26.05) * mm, "end": v(11.43, -26.3) * mm});
            skLineSegment(sketch, "E68.0.23.0", {"start": v(12.7, -27.05) * mm, "end": v(11.43, -27.05) * mm});
            skLineSegment(sketch, "E68.0.23.1", {"start": v(11.43, -27.3) * mm, "end": v(12.7, -27.3) * mm});
            skLineSegment(sketch, "E68.0.23.2", {"start": v(11.43, -27.05) * mm, "end": v(11.43, -27.3) * mm});
            skLineSegment(sketch, "E68.0.24.0", {"start": v(12.7, -28.05) * mm, "end": v(11.43, -28.05) * mm});
            skLineSegment(sketch, "E68.0.24.1", {"start": v(11.43, -28.3) * mm, "end": v(12.7, -28.3) * mm});
            skLineSegment(sketch, "E68.0.24.2", {"start": v(11.43, -28.05) * mm, "end": v(11.43, -28.3) * mm});
            skLineSegment(sketch, "E68.0.25.0", {"start": v(12.7, -29.05) * mm, "end": v(11.43, -29.05) * mm});
            skLineSegment(sketch, "E68.0.25.1", {"start": v(11.43, -29.3) * mm, "end": v(12.7, -29.3) * mm});
            skLineSegment(sketch, "E68.0.25.2", {"start": v(11.43, -29.05) * mm, "end": v(11.43, -29.3) * mm});
            skLineSegment(sketch, "E68.0.26.0", {"start": v(12.7, -30.05) * mm, "end": v(11.43, -30.05) * mm});
            skLineSegment(sketch, "E68.0.26.1", {"start": v(11.43, -30.3) * mm, "end": v(12.7, -30.3) * mm});
            skLineSegment(sketch, "E68.0.26.2", {"start": v(11.43, -30.05) * mm, "end": v(11.43, -30.3) * mm});
            skLineSegment(sketch, "E68.0.27.0", {"start": v(12.7, -31.05) * mm, "end": v(11.43, -31.05) * mm});
            skLineSegment(sketch, "E68.0.27.1", {"start": v(11.43, -31.3) * mm, "end": v(12.7, -31.3) * mm});
            skLineSegment(sketch, "E68.0.27.2", {"start": v(11.43, -31.05) * mm, "end": v(11.43, -31.3) * mm});
            skLineSegment(sketch, "E68.0.28.0", {"start": v(12.7, -32.05) * mm, "end": v(11.43, -32.05) * mm});
            skLineSegment(sketch, "E68.0.28.1", {"start": v(11.43, -32.3) * mm, "end": v(12.7, -32.3) * mm});
            skLineSegment(sketch, "E68.0.28.2", {"start": v(11.43, -32.05) * mm, "end": v(11.43, -32.3) * mm});
            skLineSegment(sketch, "E68.0.29.0", {"start": v(12.7, -33.05) * mm, "end": v(11.43, -33.05) * mm});
            skLineSegment(sketch, "E68.0.29.1", {"start": v(11.43, -33.3) * mm, "end": v(12.7, -33.3) * mm});
            skLineSegment(sketch, "E68.0.29.2", {"start": v(11.43, -33.05) * mm, "end": v(11.43, -33.3) * mm});
            skLineSegment(sketch, "E68.0.30.0", {"start": v(12.7, -34.05) * mm, "end": v(11.43, -34.05) * mm});
            skLineSegment(sketch, "E68.0.30.1", {"start": v(11.43, -34.3) * mm, "end": v(12.7, -34.3) * mm});
            skLineSegment(sketch, "E68.0.30.2", {"start": v(11.43, -34.05) * mm, "end": v(11.43, -34.3) * mm});
            skLineSegment(sketch, "E68.0.31.0", {"start": v(12.7, -35.05) * mm, "end": v(11.43, -35.05) * mm});
            skLineSegment(sketch, "E68.0.31.1", {"start": v(11.43, -35.3) * mm, "end": v(12.7, -35.3) * mm});
            skLineSegment(sketch, "E68.0.31.2", {"start": v(11.43, -35.05) * mm, "end": v(11.43, -35.3) * mm});
            skLineSegment(sketch, "E68.0.32.0", {"start": v(12.7, -36.05) * mm, "end": v(11.43, -36.05) * mm});
            skLineSegment(sketch, "E68.0.32.1", {"start": v(11.43, -36.3) * mm, "end": v(12.7, -36.3) * mm});
            skLineSegment(sketch, "E68.0.32.2", {"start": v(11.43, -36.05) * mm, "end": v(11.43, -36.3) * mm});
            skLineSegment(sketch, "E68.0.33.0", {"start": v(12.7, -37.05) * mm, "end": v(11.43, -37.05) * mm});
            skLineSegment(sketch, "E68.0.33.1", {"start": v(11.43, -37.3) * mm, "end": v(12.7, -37.3) * mm});
            skLineSegment(sketch, "E68.0.33.2", {"start": v(11.43, -37.05) * mm, "end": v(11.43, -37.3) * mm});
            skLineSegment(sketch, "E68.0.34.0", {"start": v(12.7, -38.05) * mm, "end": v(11.43, -38.05) * mm});
            skLineSegment(sketch, "E68.0.34.1", {"start": v(11.43, -38.3) * mm, "end": v(12.7, -38.3) * mm});
            skLineSegment(sketch, "E68.0.34.2", {"start": v(11.43, -38.05) * mm, "end": v(11.43, -38.3) * mm});
            skLineSegment(sketch, "E68.0.35.0", {"start": v(12.7, -39.05) * mm, "end": v(11.43, -39.05) * mm});
            skLineSegment(sketch, "E68.0.35.1", {"start": v(11.43, -39.3) * mm, "end": v(12.7, -39.3) * mm});
            skLineSegment(sketch, "E68.0.35.2", {"start": v(11.43, -39.05) * mm, "end": v(11.43, -39.3) * mm});
            skLineSegment(sketch, "E68.0.36.0", {"start": v(12.7, -40.05) * mm, "end": v(11.43, -40.05) * mm});
            skLineSegment(sketch, "E68.0.36.1", {"start": v(11.43, -40.3) * mm, "end": v(12.7, -40.3) * mm});
            skLineSegment(sketch, "E68.0.36.2", {"start": v(11.43, -40.05) * mm, "end": v(11.43, -40.3) * mm});
            skLineSegment(sketch, "E68.0.37.0", {"start": v(12.7, -41.05) * mm, "end": v(11.43, -41.05) * mm});
            skLineSegment(sketch, "E68.0.37.1", {"start": v(11.43, -41.3) * mm, "end": v(12.7, -41.3) * mm});
            skLineSegment(sketch, "E68.0.37.2", {"start": v(11.43, -41.05) * mm, "end": v(11.43, -41.3) * mm});
            skLineSegment(sketch, "E68.0.38.0", {"start": v(12.7, -42.05) * mm, "end": v(11.43, -42.05) * mm});
            skLineSegment(sketch, "E68.0.38.1", {"start": v(11.43, -42.3) * mm, "end": v(12.7, -42.3) * mm});
            skLineSegment(sketch, "E68.0.38.2", {"start": v(11.43, -42.05) * mm, "end": v(11.43, -42.3) * mm});
            skLineSegment(sketch, "E68.0.39.0", {"start": v(12.7, -43.05) * mm, "end": v(11.43, -43.05) * mm});
            skLineSegment(sketch, "E68.0.39.1", {"start": v(11.43, -43.3) * mm, "end": v(12.7, -43.3) * mm});
            skLineSegment(sketch, "E68.0.39.2", {"start": v(11.43, -43.05) * mm, "end": v(11.43, -43.3) * mm});
            skLineSegment(sketch, "E68.0.40.0", {"start": v(12.7, -44.05) * mm, "end": v(11.43, -44.05) * mm});
            skLineSegment(sketch, "E68.0.40.1", {"start": v(11.43, -44.3) * mm, "end": v(12.7, -44.3) * mm});
            skLineSegment(sketch, "E68.0.40.2", {"start": v(11.43, -44.05) * mm, "end": v(11.43, -44.3) * mm});
            skLineSegment(sketch, "E68.0.41.0", {"start": v(12.7, -45.05) * mm, "end": v(11.43, -45.05) * mm});
            skLineSegment(sketch, "E68.0.41.1", {"start": v(11.43, -45.3) * mm, "end": v(12.7, -45.3) * mm});
            skLineSegment(sketch, "E68.0.41.2", {"start": v(11.43, -45.05) * mm, "end": v(11.43, -45.3) * mm});
            skLineSegment(sketch, "E68.0.42.0", {"start": v(12.7, -46.05) * mm, "end": v(11.43, -46.05) * mm});
            skLineSegment(sketch, "E68.0.42.1", {"start": v(11.43, -46.3) * mm, "end": v(12.7, -46.3) * mm});
            skLineSegment(sketch, "E68.0.42.2", {"start": v(11.43, -46.05) * mm, "end": v(11.43, -46.3) * mm});
            skLineSegment(sketch, "E68.0.43.0", {"start": v(12.7, -47.05) * mm, "end": v(11.43, -47.05) * mm});
            skLineSegment(sketch, "E68.0.43.1", {"start": v(11.43, -47.3) * mm, "end": v(12.7, -47.3) * mm});
            skLineSegment(sketch, "E68.0.43.2", {"start": v(11.43, -47.05) * mm, "end": v(11.43, -47.3) * mm});
            skLineSegment(sketch, "E68.0.44.0", {"start": v(12.7, -48.05) * mm, "end": v(11.43, -48.05) * mm});
            skLineSegment(sketch, "E68.0.44.1", {"start": v(11.43, -48.3) * mm, "end": v(12.7, -48.3) * mm});
            skLineSegment(sketch, "E68.0.44.2", {"start": v(11.43, -48.05) * mm, "end": v(11.43, -48.3) * mm});
            skLineSegment(sketch, "E68.0.45.0", {"start": v(12.7, -49.05) * mm, "end": v(11.43, -49.05) * mm});
            skLineSegment(sketch, "E68.0.45.1", {"start": v(11.43, -49.3) * mm, "end": v(12.7, -49.3) * mm});
            skLineSegment(sketch, "E68.0.45.2", {"start": v(11.43, -49.05) * mm, "end": v(11.43, -49.3) * mm});
            skLineSegment(sketch, "E68.0.46.0", {"start": v(12.7, -50.05) * mm, "end": v(11.43, -50.05) * mm});
            skLineSegment(sketch, "E68.0.46.1", {"start": v(11.43, -50.3) * mm, "end": v(12.7, -50.3) * mm});
            skLineSegment(sketch, "E68.0.46.2", {"start": v(11.43, -50.05) * mm, "end": v(11.43, -50.3) * mm});
            skLineSegment(sketch, "E68.0.47.0", {"start": v(12.7, -51.05) * mm, "end": v(11.43, -51.05) * mm});
            skLineSegment(sketch, "E68.0.47.1", {"start": v(11.43, -51.3) * mm, "end": v(12.7, -51.3) * mm});
            skLineSegment(sketch, "E68.0.47.2", {"start": v(11.43, -51.05) * mm, "end": v(11.43, -51.3) * mm});
            skLineSegment(sketch, "E68.0.48.0", {"start": v(12.7, -52.05) * mm, "end": v(11.43, -52.05) * mm});
            skLineSegment(sketch, "E68.0.48.1", {"start": v(11.43, -52.3) * mm, "end": v(12.7, -52.3) * mm});
            skLineSegment(sketch, "E68.0.48.2", {"start": v(11.43, -52.05) * mm, "end": v(11.43, -52.3) * mm});
            skLineSegment(sketch, "E68.0.49.0", {"start": v(12.7, -53.05) * mm, "end": v(11.43, -53.05) * mm});
            skLineSegment(sketch, "E68.0.49.1", {"start": v(11.43, -53.3) * mm, "end": v(12.7, -53.3) * mm});
            skLineSegment(sketch, "E68.0.49.2", {"start": v(11.43, -53.05) * mm, "end": v(11.43, -53.3) * mm});
            skLineSegment(sketch, "E68.0.50.0", {"start": v(12.7, -54.05) * mm, "end": v(11.43, -54.05) * mm});
            skLineSegment(sketch, "E68.0.50.1", {"start": v(11.43, -54.3) * mm, "end": v(12.7, -54.3) * mm});
            skLineSegment(sketch, "E68.0.50.2", {"start": v(11.43, -54.05) * mm, "end": v(11.43, -54.3) * mm});
            skLineSegment(sketch, "E68.0.51.0", {"start": v(12.7, -55.05) * mm, "end": v(11.43, -55.05) * mm});
            skLineSegment(sketch, "E68.0.51.1", {"start": v(11.43, -55.3) * mm, "end": v(12.7, -55.3) * mm});
            skLineSegment(sketch, "E68.0.51.2", {"start": v(11.43, -55.05) * mm, "end": v(11.43, -55.3) * mm});
            skLineSegment(sketch, "E68.0.52.0", {"start": v(12.7, -56.05) * mm, "end": v(11.43, -56.05) * mm});
            skLineSegment(sketch, "E68.0.52.1", {"start": v(11.43, -56.3) * mm, "end": v(12.7, -56.3) * mm});
            skLineSegment(sketch, "E68.0.52.2", {"start": v(11.43, -56.05) * mm, "end": v(11.43, -56.3) * mm});
            skLineSegment(sketch, "E68.0.53.0", {"start": v(12.7, -57.05) * mm, "end": v(11.43, -57.05) * mm});
            skLineSegment(sketch, "E68.0.53.1", {"start": v(11.43, -57.3) * mm, "end": v(12.7, -57.3) * mm});
            skLineSegment(sketch, "E68.0.53.2", {"start": v(11.43, -57.05) * mm, "end": v(11.43, -57.3) * mm});
            skLineSegment(sketch, "E68.0.54.0", {"start": v(12.7, -58.05) * mm, "end": v(11.43, -58.05) * mm});
            skLineSegment(sketch, "E68.0.54.1", {"start": v(11.43, -58.3) * mm, "end": v(12.7, -58.3) * mm});
            skLineSegment(sketch, "E68.0.54.2", {"start": v(11.43, -58.05) * mm, "end": v(11.43, -58.3) * mm});
            skLineSegment(sketch, "E68.0.55.0", {"start": v(12.7, -59.05) * mm, "end": v(11.43, -59.05) * mm});
            skLineSegment(sketch, "E68.0.55.1", {"start": v(11.43, -59.3) * mm, "end": v(12.7, -59.3) * mm});
            skLineSegment(sketch, "E68.0.55.2", {"start": v(11.43, -59.05) * mm, "end": v(11.43, -59.3) * mm});
            skLineSegment(sketch, "E68.0.56.0", {"start": v(12.7, -60.05) * mm, "end": v(11.43, -60.05) * mm});
            skLineSegment(sketch, "E68.0.56.1", {"start": v(11.43, -60.3) * mm, "end": v(12.7, -60.3) * mm});
            skLineSegment(sketch, "E68.0.56.2", {"start": v(11.43, -60.05) * mm, "end": v(11.43, -60.3) * mm});
            skLineSegment(sketch, "E68.0.57.0", {"start": v(12.7, -61.05) * mm, "end": v(11.43, -61.05) * mm});
            skLineSegment(sketch, "E68.0.57.1", {"start": v(11.43, -61.3) * mm, "end": v(12.7, -61.3) * mm});
            skLineSegment(sketch, "E68.0.57.2", {"start": v(11.43, -61.05) * mm, "end": v(11.43, -61.3) * mm});
            skLineSegment(sketch, "E68.0.58.0", {"start": v(12.7, -62.05) * mm, "end": v(11.43, -62.05) * mm});
            skLineSegment(sketch, "E68.0.58.1", {"start": v(11.43, -62.3) * mm, "end": v(12.7, -62.3) * mm});
            skLineSegment(sketch, "E68.0.58.2", {"start": v(11.43, -62.05) * mm, "end": v(11.43, -62.3) * mm});
            skLineSegment(sketch, "E68.0.59.0", {"start": v(12.7, -63.05) * mm, "end": v(11.43, -63.05) * mm});
            skLineSegment(sketch, "E68.0.59.1", {"start": v(11.43, -63.3) * mm, "end": v(12.7, -63.3) * mm});
            skLineSegment(sketch, "E68.0.59.2", {"start": v(11.43, -63.05) * mm, "end": v(11.43, -63.3) * mm});
            skLineSegment(sketch, "E68.0.60.0", {"start": v(12.7, -64.05) * mm, "end": v(11.43, -64.05) * mm});
            skLineSegment(sketch, "E68.0.60.1", {"start": v(11.43, -64.3) * mm, "end": v(12.7, -64.3) * mm});
            skLineSegment(sketch, "E68.0.60.2", {"start": v(11.43, -64.05) * mm, "end": v(11.43, -64.3) * mm});
            skLineSegment(sketch, "E68.0.61.0", {"start": v(12.7, -65.05) * mm, "end": v(11.43, -65.05) * mm});
            skLineSegment(sketch, "E68.0.61.1", {"start": v(11.43, -65.3) * mm, "end": v(12.7, -65.3) * mm});
            skLineSegment(sketch, "E68.0.61.2", {"start": v(11.43, -65.05) * mm, "end": v(11.43, -65.3) * mm});
            skLineSegment(sketch, "E68.0.62.0", {"start": v(12.7, -66.05) * mm, "end": v(11.43, -66.05) * mm});
            skLineSegment(sketch, "E68.0.62.1", {"start": v(11.43, -66.3) * mm, "end": v(12.7, -66.3) * mm});
            skLineSegment(sketch, "E68.0.62.2", {"start": v(11.43, -66.05) * mm, "end": v(11.43, -66.3) * mm});
            skLineSegment(sketch, "E68.0.63.0", {"start": v(12.7, -67.05) * mm, "end": v(11.43, -67.05) * mm});
            skLineSegment(sketch, "E68.0.63.1", {"start": v(11.43, -67.3) * mm, "end": v(12.7, -67.3) * mm});
            skLineSegment(sketch, "E68.0.63.2", {"start": v(11.43, -67.05) * mm, "end": v(11.43, -67.3) * mm});
            skLineSegment(sketch, "E68.0.64.0", {"start": v(12.7, -68.05) * mm, "end": v(11.43, -68.05) * mm});
            skLineSegment(sketch, "E68.0.64.1", {"start": v(11.43, -68.3) * mm, "end": v(12.7, -68.3) * mm});
            skLineSegment(sketch, "E68.0.64.2", {"start": v(11.43, -68.05) * mm, "end": v(11.43, -68.3) * mm});
            skLineSegment(sketch, "E68.0.65.0", {"start": v(12.7, -69.05) * mm, "end": v(11.43, -69.05) * mm});
            skLineSegment(sketch, "E68.0.65.1", {"start": v(11.43, -69.3) * mm, "end": v(12.7, -69.3) * mm});
            skLineSegment(sketch, "E68.0.65.2", {"start": v(11.43, -69.05) * mm, "end": v(11.43, -69.3) * mm});
            skLineSegment(sketch, "E68.0.66.0", {"start": v(12.7, -70.05) * mm, "end": v(11.43, -70.05) * mm});
            skLineSegment(sketch, "E68.0.66.1", {"start": v(11.43, -70.3) * mm, "end": v(12.7, -70.3) * mm});
            skLineSegment(sketch, "E68.0.66.2", {"start": v(11.43, -70.05) * mm, "end": v(11.43, -70.3) * mm});
            skLineSegment(sketch, "E68.0.67.0", {"start": v(12.7, -71.05) * mm, "end": v(11.43, -71.05) * mm});
            skLineSegment(sketch, "E68.0.67.1", {"start": v(11.43, -71.3) * mm, "end": v(12.7, -71.3) * mm});
            skLineSegment(sketch, "E68.0.67.2", {"start": v(11.43, -71.05) * mm, "end": v(11.43, -71.3) * mm});
            skLineSegment(sketch, "E68.0.68.0", {"start": v(12.7, -72.05) * mm, "end": v(11.43, -72.05) * mm});
            skLineSegment(sketch, "E68.0.68.1", {"start": v(11.43, -72.3) * mm, "end": v(12.7, -72.3) * mm});
            skLineSegment(sketch, "E68.0.68.2", {"start": v(11.43, -72.05) * mm, "end": v(11.43, -72.3) * mm});
            skLineSegment(sketch, "E68.0.69.0", {"start": v(12.7, -73.05) * mm, "end": v(11.43, -73.05) * mm});
            skLineSegment(sketch, "E68.0.69.1", {"start": v(11.43, -73.3) * mm, "end": v(12.7, -73.3) * mm});
            skLineSegment(sketch, "E68.0.69.2", {"start": v(11.43, -73.05) * mm, "end": v(11.43, -73.3) * mm});
            skLineSegment(sketch, "E68.0.70.0", {"start": v(12.7, -74.05) * mm, "end": v(11.43, -74.05) * mm});
            skLineSegment(sketch, "E68.0.70.1", {"start": v(11.43, -74.3) * mm, "end": v(12.7, -74.3) * mm});
            skLineSegment(sketch, "E68.0.70.2", {"start": v(11.43, -74.05) * mm, "end": v(11.43, -74.3) * mm});
            skLineSegment(sketch, "E68.0.71.0", {"start": v(12.7, -75.05) * mm, "end": v(11.43, -75.05) * mm});
            skLineSegment(sketch, "E68.0.71.1", {"start": v(11.43, -75.3) * mm, "end": v(12.7, -75.3) * mm});
            skLineSegment(sketch, "E68.0.71.2", {"start": v(11.43, -75.05) * mm, "end": v(11.43, -75.3) * mm});
            skLineSegment(sketch, "E68.0.72.0", {"start": v(12.7, -76.05) * mm, "end": v(11.43, -76.05) * mm});
            skLineSegment(sketch, "E68.0.72.1", {"start": v(11.43, -76.3) * mm, "end": v(12.7, -76.3) * mm});
            skLineSegment(sketch, "E68.0.72.2", {"start": v(11.43, -76.05) * mm, "end": v(11.43, -76.3) * mm});
            skLineSegment(sketch, "E68.0.73.0", {"start": v(12.7, -77.05) * mm, "end": v(11.43, -77.05) * mm});
            skLineSegment(sketch, "E68.0.73.1", {"start": v(11.43, -77.3) * mm, "end": v(12.7, -77.3) * mm});
            skLineSegment(sketch, "E68.0.73.2", {"start": v(11.43, -77.05) * mm, "end": v(11.43, -77.3) * mm});
            skLineSegment(sketch, "E68.0.74.0", {"start": v(12.7, -78.05) * mm, "end": v(11.43, -78.05) * mm});
            skLineSegment(sketch, "E68.0.74.1", {"start": v(11.43, -78.3) * mm, "end": v(12.7, -78.3) * mm});
            skLineSegment(sketch, "E68.0.74.2", {"start": v(11.43, -78.05) * mm, "end": v(11.43, -78.3) * mm});
            skLineSegment(sketch, "E68.0.75.0", {"start": v(12.7, -79.05) * mm, "end": v(11.43, -79.05) * mm});
            skLineSegment(sketch, "E68.0.75.1", {"start": v(11.43, -79.3) * mm, "end": v(12.7, -79.3) * mm});
            skLineSegment(sketch, "E68.0.75.2", {"start": v(11.43, -79.05) * mm, "end": v(11.43, -79.3) * mm});
            skLineSegment(sketch, "E68.0.76.0", {"start": v(12.7, -80.05) * mm, "end": v(11.43, -80.05) * mm});
            skLineSegment(sketch, "E68.0.76.1", {"start": v(11.43, -80.3) * mm, "end": v(12.7, -80.3) * mm});
            skLineSegment(sketch, "E68.0.76.2", {"start": v(11.43, -80.05) * mm, "end": v(11.43, -80.3) * mm});
            skLineSegment(sketch, "E68.0.77.0", {"start": v(12.7, -81.05) * mm, "end": v(11.43, -81.05) * mm});
            skLineSegment(sketch, "E68.0.77.1", {"start": v(11.43, -81.3) * mm, "end": v(12.7, -81.3) * mm});
            skLineSegment(sketch, "E68.0.77.2", {"start": v(11.43, -81.05) * mm, "end": v(11.43, -81.3) * mm});
            skLineSegment(sketch, "E68.0.78.0", {"start": v(12.7, -82.05) * mm, "end": v(11.43, -82.05) * mm});
            skLineSegment(sketch, "E68.0.78.1", {"start": v(11.43, -82.3) * mm, "end": v(12.7, -82.3) * mm});
            skLineSegment(sketch, "E68.0.78.2", {"start": v(11.43, -82.05) * mm, "end": v(11.43, -82.3) * mm});
            skLineSegment(sketch, "E68.0.79.0", {"start": v(12.7, -83.05) * mm, "end": v(11.43, -83.05) * mm});
            skLineSegment(sketch, "E68.0.79.1", {"start": v(11.43, -83.3) * mm, "end": v(12.7, -83.3) * mm});
            skLineSegment(sketch, "E68.0.79.2", {"start": v(11.43, -83.05) * mm, "end": v(11.43, -83.3) * mm});
            skLineSegment(sketch, "E68.0.80.0", {"start": v(12.7, -84.05) * mm, "end": v(11.43, -84.05) * mm});
            skLineSegment(sketch, "E68.0.80.1", {"start": v(11.43, -84.3) * mm, "end": v(12.7, -84.3) * mm});
            skLineSegment(sketch, "E68.0.80.2", {"start": v(11.43, -84.05) * mm, "end": v(11.43, -84.3) * mm});
            skLineSegment(sketch, "E68.0.81.0", {"start": v(12.7, -85.05) * mm, "end": v(11.43, -85.05) * mm});
            skLineSegment(sketch, "E68.0.81.1", {"start": v(11.43, -85.3) * mm, "end": v(12.7, -85.3) * mm});
            skLineSegment(sketch, "E68.0.81.2", {"start": v(11.43, -85.05) * mm, "end": v(11.43, -85.3) * mm});
            skLineSegment(sketch, "E68.0.82.0", {"start": v(12.7, -86.05) * mm, "end": v(11.43, -86.05) * mm});
            skLineSegment(sketch, "E68.0.82.1", {"start": v(11.43, -86.3) * mm, "end": v(12.7, -86.3) * mm});
            skLineSegment(sketch, "E68.0.82.2", {"start": v(11.43, -86.05) * mm, "end": v(11.43, -86.3) * mm});
            skLineSegment(sketch, "E68.0.83.0", {"start": v(12.7, -87.05) * mm, "end": v(11.43, -87.05) * mm});
            skLineSegment(sketch, "E68.0.83.1", {"start": v(11.43, -87.3) * mm, "end": v(12.7, -87.3) * mm});
            skLineSegment(sketch, "E68.0.83.2", {"start": v(11.43, -87.05) * mm, "end": v(11.43, -87.3) * mm});
            skLineSegment(sketch, "E68.0.84.0", {"start": v(12.7, -88.05) * mm, "end": v(11.43, -88.05) * mm});
            skLineSegment(sketch, "E68.0.84.1", {"start": v(11.43, -88.3) * mm, "end": v(12.7, -88.3) * mm});
            skLineSegment(sketch, "E68.0.84.2", {"start": v(11.43, -88.05) * mm, "end": v(11.43, -88.3) * mm});
            skLineSegment(sketch, "E68.0.85.0", {"start": v(12.7, -89.05) * mm, "end": v(11.43, -89.05) * mm});
            skLineSegment(sketch, "E68.0.85.1", {"start": v(11.43, -89.3) * mm, "end": v(12.7, -89.3) * mm});
            skLineSegment(sketch, "E68.0.85.2", {"start": v(11.43, -89.05) * mm, "end": v(11.43, -89.3) * mm});
            skLineSegment(sketch, "E68.0.86.0", {"start": v(12.7, -90.05) * mm, "end": v(11.43, -90.05) * mm});
            skLineSegment(sketch, "E68.0.86.1", {"start": v(11.43, -90.3) * mm, "end": v(12.7, -90.3) * mm});
            skLineSegment(sketch, "E68.0.86.2", {"start": v(11.43, -90.05) * mm, "end": v(11.43, -90.3) * mm});
            skLineSegment(sketch, "E68.0.87.0", {"start": v(12.7, -91.05) * mm, "end": v(11.43, -91.05) * mm});
            skLineSegment(sketch, "E68.0.87.1", {"start": v(11.43, -91.3) * mm, "end": v(12.7, -91.3) * mm});
            skLineSegment(sketch, "E68.0.87.2", {"start": v(11.43, -91.05) * mm, "end": v(11.43, -91.3) * mm});
            skLineSegment(sketch, "E68.0.88.0", {"start": v(12.7, -92.05) * mm, "end": v(11.43, -92.05) * mm});
            skLineSegment(sketch, "E68.0.88.1", {"start": v(11.43, -92.3) * mm, "end": v(12.7, -92.3) * mm});
            skLineSegment(sketch, "E68.0.88.2", {"start": v(11.43, -92.05) * mm, "end": v(11.43, -92.3) * mm});
            skLineSegment(sketch, "E68.0.89.0", {"start": v(12.7, -93.05) * mm, "end": v(11.43, -93.05) * mm});
            skLineSegment(sketch, "E68.0.89.1", {"start": v(11.43, -93.3) * mm, "end": v(12.7, -93.3) * mm});
            skLineSegment(sketch, "E68.0.89.2", {"start": v(11.43, -93.05) * mm, "end": v(11.43, -93.3) * mm});
            skLineSegment(sketch, "E68.0.90.0", {"start": v(12.7, -94.05) * mm, "end": v(11.43, -94.05) * mm});
            skLineSegment(sketch, "E68.0.90.1", {"start": v(11.43, -94.3) * mm, "end": v(12.7, -94.3) * mm});
            skLineSegment(sketch, "E68.0.90.2", {"start": v(11.43, -94.05) * mm, "end": v(11.43, -94.3) * mm});
            skLineSegment(sketch, "E68.0.91.0", {"start": v(12.7, -95.05) * mm, "end": v(11.43, -95.05) * mm});
            skLineSegment(sketch, "E68.0.91.1", {"start": v(11.43, -95.3) * mm, "end": v(12.7, -95.3) * mm});
            skLineSegment(sketch, "E68.0.91.2", {"start": v(11.43, -95.05) * mm, "end": v(11.43, -95.3) * mm});
            skLineSegment(sketch, "E68.0.92.0", {"start": v(12.7, -96.05) * mm, "end": v(11.43, -96.05) * mm});
            skLineSegment(sketch, "E68.0.92.1", {"start": v(11.43, -96.3) * mm, "end": v(12.7, -96.3) * mm});
            skLineSegment(sketch, "E68.0.92.2", {"start": v(11.43, -96.05) * mm, "end": v(11.43, -96.3) * mm});
            skLineSegment(sketch, "E68.0.93.0", {"start": v(12.7, -97.05) * mm, "end": v(11.43, -97.05) * mm});
            skLineSegment(sketch, "E68.0.93.1", {"start": v(11.43, -97.3) * mm, "end": v(12.7, -97.3) * mm});
            skLineSegment(sketch, "E68.0.93.2", {"start": v(11.43, -97.05) * mm, "end": v(11.43, -97.3) * mm});
            skLineSegment(sketch, "E68.0.94.0", {"start": v(12.7, -98.05) * mm, "end": v(11.43, -98.05) * mm});
            skLineSegment(sketch, "E68.0.94.1", {"start": v(11.43, -98.3) * mm, "end": v(12.7, -98.3) * mm});
            skLineSegment(sketch, "E68.0.94.2", {"start": v(11.43, -98.05) * mm, "end": v(11.43, -98.3) * mm});
            skLineSegment(sketch, "E68.0.95.0", {"start": v(12.7, -99.05) * mm, "end": v(11.43, -99.05) * mm});
            skLineSegment(sketch, "E68.0.95.1", {"start": v(11.43, -99.3) * mm, "end": v(12.7, -99.3) * mm});
            skLineSegment(sketch, "E68.0.95.2", {"start": v(11.43, -99.05) * mm, "end": v(11.43, -99.3) * mm});
            skLineSegment(sketch, "E68.0.96.0", {"start": v(12.7, -100.05) * mm, "end": v(11.43, -100.05) * mm});
            skLineSegment(sketch, "E68.0.96.1", {"start": v(11.43, -100.3) * mm, "end": v(12.7, -100.3) * mm});
            skLineSegment(sketch, "E68.0.96.2", {"start": v(11.43, -100.05) * mm, "end": v(11.43, -100.3) * mm});
            skLineSegment(sketch, "E68.0.97.0", {"start": v(12.7, -101.05) * mm, "end": v(11.43, -101.05) * mm});
            skLineSegment(sketch, "E68.0.97.1", {"start": v(11.43, -101.3) * mm, "end": v(12.7, -101.3) * mm});
            skLineSegment(sketch, "E68.0.97.2", {"start": v(11.43, -101.05) * mm, "end": v(11.43, -101.3) * mm});
            skLineSegment(sketch, "E68.0.98.0", {"start": v(12.7, -102.05) * mm, "end": v(11.43, -102.05) * mm});
            skLineSegment(sketch, "E68.0.98.1", {"start": v(11.43, -102.3) * mm, "end": v(12.7, -102.3) * mm});
            skLineSegment(sketch, "E68.0.98.2", {"start": v(11.43, -102.05) * mm, "end": v(11.43, -102.3) * mm});
            skLineSegment(sketch, "E68.0.99.0", {"start": v(12.7, -103.05) * mm, "end": v(11.43, -103.05) * mm});
            skLineSegment(sketch, "E68.0.99.1", {"start": v(11.43, -103.3) * mm, "end": v(12.7, -103.3) * mm});
            skLineSegment(sketch, "E68.0.99.2", {"start": v(11.43, -103.05) * mm, "end": v(11.43, -103.3) * mm});
            skLineSegment(sketch, "E68.direction1", {"start": v(11.43, -4.05) * mm, "end": v(36.83, -4.05) * mm, "construction": true});
            skLineSegment(sketch, "E68.direction2", {"start": v(11.43, -4.05) * mm, "end": v(11.43, -5.05) * mm, "construction": true});
            skLineSegment(sketch, "E69.0.2.0", {"start": v(12.7, -104.05) * mm, "end": v(11.43, -104.05) * mm});
            skLineSegment(sketch, "E69.0.2.1", {"start": v(11.43, -104.3) * mm, "end": v(12.7, -104.3) * mm});
            skLineSegment(sketch, "E69.0.2.2", {"start": v(11.43, -104.05) * mm, "end": v(11.43, -104.3) * mm});
            skLineSegment(sketch, "E69.0.3.0", {"start": v(12.7, -105.05) * mm, "end": v(11.43, -105.05) * mm});
            skLineSegment(sketch, "E69.0.3.1", {"start": v(11.43, -105.3) * mm, "end": v(12.7, -105.3) * mm});
            skLineSegment(sketch, "E69.0.3.2", {"start": v(11.43, -105.05) * mm, "end": v(11.43, -105.3) * mm});
            skLineSegment(sketch, "E69.0.4.0", {"start": v(12.7, -106.05) * mm, "end": v(11.43, -106.05) * mm});
            skLineSegment(sketch, "E69.0.4.1", {"start": v(11.43, -106.3) * mm, "end": v(12.7, -106.3) * mm});
            skLineSegment(sketch, "E69.0.4.2", {"start": v(11.43, -106.05) * mm, "end": v(11.43, -106.3) * mm});
            skLineSegment(sketch, "E69.0.5.0", {"start": v(12.7, -107.05) * mm, "end": v(11.43, -107.05) * mm});
            skLineSegment(sketch, "E69.0.5.1", {"start": v(11.43, -107.3) * mm, "end": v(12.7, -107.3) * mm});
            skLineSegment(sketch, "E69.0.5.2", {"start": v(11.43, -107.05) * mm, "end": v(11.43, -107.3) * mm});
            skLineSegment(sketch, "E69.0.6.0", {"start": v(12.7, -108.05) * mm, "end": v(11.43, -108.05) * mm});
            skLineSegment(sketch, "E69.0.6.1", {"start": v(11.43, -108.3) * mm, "end": v(12.7, -108.3) * mm});
            skLineSegment(sketch, "E69.0.6.2", {"start": v(11.43, -108.05) * mm, "end": v(11.43, -108.3) * mm});
            skLineSegment(sketch, "E69.0.7.0", {"start": v(12.7, -109.05) * mm, "end": v(11.43, -109.05) * mm});
            skLineSegment(sketch, "E69.0.7.1", {"start": v(11.43, -109.3) * mm, "end": v(12.7, -109.3) * mm});
            skLineSegment(sketch, "E69.0.7.2", {"start": v(11.43, -109.05) * mm, "end": v(11.43, -109.3) * mm});
            skLineSegment(sketch, "E69.0.8.0", {"start": v(12.7, -110.05) * mm, "end": v(11.43, -110.05) * mm});
            skLineSegment(sketch, "E69.0.8.1", {"start": v(11.43, -110.3) * mm, "end": v(12.7, -110.3) * mm});
            skLineSegment(sketch, "E69.0.8.2", {"start": v(11.43, -110.05) * mm, "end": v(11.43, -110.3) * mm});
            skLineSegment(sketch, "E69.0.9.0", {"start": v(12.7, -111.05) * mm, "end": v(11.43, -111.05) * mm});
            skLineSegment(sketch, "E69.0.9.1", {"start": v(11.43, -111.3) * mm, "end": v(12.7, -111.3) * mm});
            skLineSegment(sketch, "E69.0.9.2", {"start": v(11.43, -111.05) * mm, "end": v(11.43, -111.3) * mm});
            skLineSegment(sketch, "E69.0.10.0", {"start": v(12.7, -112.05) * mm, "end": v(11.43, -112.05) * mm});
            skLineSegment(sketch, "E69.0.10.1", {"start": v(11.43, -112.3) * mm, "end": v(12.7, -112.3) * mm});
            skLineSegment(sketch, "E69.0.10.2", {"start": v(11.43, -112.05) * mm, "end": v(11.43, -112.3) * mm});
            skLineSegment(sketch, "E69.0.11.0", {"start": v(12.7, -113.05) * mm, "end": v(11.43, -113.05) * mm});
            skLineSegment(sketch, "E69.0.11.1", {"start": v(11.43, -113.3) * mm, "end": v(12.7, -113.3) * mm});
            skLineSegment(sketch, "E69.0.11.2", {"start": v(11.43, -113.05) * mm, "end": v(11.43, -113.3) * mm});
            skLineSegment(sketch, "E69.0.12.0", {"start": v(12.7, -114.05) * mm, "end": v(11.43, -114.05) * mm});
            skLineSegment(sketch, "E69.0.12.1", {"start": v(11.43, -114.3) * mm, "end": v(12.7, -114.3) * mm});
            skLineSegment(sketch, "E69.0.12.2", {"start": v(11.43, -114.05) * mm, "end": v(11.43, -114.3) * mm});
            skLineSegment(sketch, "E69.0.13.0", {"start": v(12.7, -115.05) * mm, "end": v(11.43, -115.05) * mm});
            skLineSegment(sketch, "E69.0.13.1", {"start": v(11.43, -115.3) * mm, "end": v(12.7, -115.3) * mm});
            skLineSegment(sketch, "E69.0.13.2", {"start": v(11.43, -115.05) * mm, "end": v(11.43, -115.3) * mm});
            skLineSegment(sketch, "E69.0.14.0", {"start": v(12.7, -116.05) * mm, "end": v(11.43, -116.05) * mm});
            skLineSegment(sketch, "E69.0.14.1", {"start": v(11.43, -116.3) * mm, "end": v(12.7, -116.3) * mm});
            skLineSegment(sketch, "E69.0.14.2", {"start": v(11.43, -116.05) * mm, "end": v(11.43, -116.3) * mm});
            skLineSegment(sketch, "E69.0.15.0", {"start": v(12.7, -117.05) * mm, "end": v(11.43, -117.05) * mm});
            skLineSegment(sketch, "E69.0.15.1", {"start": v(11.43, -117.3) * mm, "end": v(12.7, -117.3) * mm});
            skLineSegment(sketch, "E69.0.15.2", {"start": v(11.43, -117.05) * mm, "end": v(11.43, -117.3) * mm});
            skLineSegment(sketch, "E69.0.16.0", {"start": v(12.7, -118.05) * mm, "end": v(11.43, -118.05) * mm});
            skLineSegment(sketch, "E69.0.16.1", {"start": v(11.43, -118.3) * mm, "end": v(12.7, -118.3) * mm});
            skLineSegment(sketch, "E69.0.16.2", {"start": v(11.43, -118.05) * mm, "end": v(11.43, -118.3) * mm});
            skLineSegment(sketch, "E69.0.17.0", {"start": v(12.7, -119.05) * mm, "end": v(11.43, -119.05) * mm});
            skLineSegment(sketch, "E69.0.17.1", {"start": v(11.43, -119.3) * mm, "end": v(12.7, -119.3) * mm});
            skLineSegment(sketch, "E69.0.17.2", {"start": v(11.43, -119.05) * mm, "end": v(11.43, -119.3) * mm});
            skLineSegment(sketch, "E69.0.18.0", {"start": v(12.7, -120.05) * mm, "end": v(11.43, -120.05) * mm});
            skLineSegment(sketch, "E69.0.18.1", {"start": v(11.43, -120.3) * mm, "end": v(12.7, -120.3) * mm});
            skLineSegment(sketch, "E69.0.18.2", {"start": v(11.43, -120.05) * mm, "end": v(11.43, -120.3) * mm});
            skLineSegment(sketch, "E69.0.19.0", {"start": v(12.7, -121.05) * mm, "end": v(11.43, -121.05) * mm});
            skLineSegment(sketch, "E69.0.19.1", {"start": v(11.43, -121.3) * mm, "end": v(12.7, -121.3) * mm});
            skLineSegment(sketch, "E69.0.19.2", {"start": v(11.43, -121.05) * mm, "end": v(11.43, -121.3) * mm});
            skLineSegment(sketch, "E69.0.20.0", {"start": v(12.7, -122.05) * mm, "end": v(11.43, -122.05) * mm});
            skLineSegment(sketch, "E69.0.20.1", {"start": v(11.43, -122.3) * mm, "end": v(12.7, -122.3) * mm});
            skLineSegment(sketch, "E69.0.20.2", {"start": v(11.43, -122.05) * mm, "end": v(11.43, -122.3) * mm});
            skLineSegment(sketch, "E69.0.21.0", {"start": v(12.7, -123.05) * mm, "end": v(11.43, -123.05) * mm});
            skLineSegment(sketch, "E69.0.21.1", {"start": v(11.43, -123.3) * mm, "end": v(12.7, -123.3) * mm});
            skLineSegment(sketch, "E69.0.21.2", {"start": v(11.43, -123.05) * mm, "end": v(11.43, -123.3) * mm});
            skLineSegment(sketch, "E69.0.22.0", {"start": v(12.7, -124.05) * mm, "end": v(11.43, -124.05) * mm});
            skLineSegment(sketch, "E69.0.22.1", {"start": v(11.43, -124.3) * mm, "end": v(12.7, -124.3) * mm});
            skLineSegment(sketch, "E69.0.22.2", {"start": v(11.43, -124.05) * mm, "end": v(11.43, -124.3) * mm});
            skLineSegment(sketch, "E69.0.23.0", {"start": v(12.7, -125.05) * mm, "end": v(11.43, -125.05) * mm});
            skLineSegment(sketch, "E69.0.23.1", {"start": v(11.43, -125.3) * mm, "end": v(12.7, -125.3) * mm});
            skLineSegment(sketch, "E69.0.23.2", {"start": v(11.43, -125.05) * mm, "end": v(11.43, -125.3) * mm});
            skLineSegment(sketch, "E69.0.24.0", {"start": v(12.7, -126.05) * mm, "end": v(11.43, -126.05) * mm});
            skLineSegment(sketch, "E69.0.24.1", {"start": v(11.43, -126.3) * mm, "end": v(12.7, -126.3) * mm});
            skLineSegment(sketch, "E69.0.24.2", {"start": v(11.43, -126.05) * mm, "end": v(11.43, -126.3) * mm});
            skLineSegment(sketch, "E69.0.25.0", {"start": v(12.7, -127.05) * mm, "end": v(11.43, -127.05) * mm});
            skLineSegment(sketch, "E69.0.25.1", {"start": v(11.43, -127.3) * mm, "end": v(12.7, -127.3) * mm});
            skLineSegment(sketch, "E69.0.25.2", {"start": v(11.43, -127.05) * mm, "end": v(11.43, -127.3) * mm});
            skLineSegment(sketch, "E69.0.26.0", {"start": v(12.7, -128.05) * mm, "end": v(11.43, -128.05) * mm});
            skLineSegment(sketch, "E69.0.26.1", {"start": v(11.43, -128.3) * mm, "end": v(12.7, -128.3) * mm});
            skLineSegment(sketch, "E69.0.26.2", {"start": v(11.43, -128.05) * mm, "end": v(11.43, -128.3) * mm});
            skLineSegment(sketch, "E69.0.27.0", {"start": v(12.7, -129.05) * mm, "end": v(11.43, -129.05) * mm});
            skLineSegment(sketch, "E69.0.27.1", {"start": v(11.43, -129.3) * mm, "end": v(12.7, -129.3) * mm});
            skLineSegment(sketch, "E69.0.27.2", {"start": v(11.43, -129.05) * mm, "end": v(11.43, -129.3) * mm});
            skLineSegment(sketch, "E69.0.28.0", {"start": v(12.7, -130.05) * mm, "end": v(11.43, -130.05) * mm});
            skLineSegment(sketch, "E69.0.28.1", {"start": v(11.43, -130.3) * mm, "end": v(12.7, -130.3) * mm});
            skLineSegment(sketch, "E69.0.28.2", {"start": v(11.43, -130.05) * mm, "end": v(11.43, -130.3) * mm});
            skLineSegment(sketch, "E69.0.29.0", {"start": v(12.7, -131.05) * mm, "end": v(11.43, -131.05) * mm});
            skLineSegment(sketch, "E69.0.29.1", {"start": v(11.43, -131.3) * mm, "end": v(12.7, -131.3) * mm});
            skLineSegment(sketch, "E69.0.29.2", {"start": v(11.43, -131.05) * mm, "end": v(11.43, -131.3) * mm});
            skLineSegment(sketch, "E69.0.30.0", {"start": v(12.7, -132.05) * mm, "end": v(11.43, -132.05) * mm});
            skLineSegment(sketch, "E69.0.30.1", {"start": v(11.43, -132.3) * mm, "end": v(12.7, -132.3) * mm});
            skLineSegment(sketch, "E69.0.30.2", {"start": v(11.43, -132.05) * mm, "end": v(11.43, -132.3) * mm});
            skLineSegment(sketch, "E69.0.31.0", {"start": v(12.7, -133.05) * mm, "end": v(11.43, -133.05) * mm});
            skLineSegment(sketch, "E69.0.31.1", {"start": v(11.43, -133.3) * mm, "end": v(12.7, -133.3) * mm});
            skLineSegment(sketch, "E69.0.31.2", {"start": v(11.43, -133.05) * mm, "end": v(11.43, -133.3) * mm});
            skLineSegment(sketch, "E69.0.32.0", {"start": v(12.7, -134.05) * mm, "end": v(11.43, -134.05) * mm});
            skLineSegment(sketch, "E69.0.32.1", {"start": v(11.43, -134.3) * mm, "end": v(12.7, -134.3) * mm});
            skLineSegment(sketch, "E69.0.32.2", {"start": v(11.43, -134.05) * mm, "end": v(11.43, -134.3) * mm});
            skLineSegment(sketch, "E69.0.33.0", {"start": v(12.7, -135.05) * mm, "end": v(11.43, -135.05) * mm});
            skLineSegment(sketch, "E69.0.33.1", {"start": v(11.43, -135.3) * mm, "end": v(12.7, -135.3) * mm});
            skLineSegment(sketch, "E69.0.33.2", {"start": v(11.43, -135.05) * mm, "end": v(11.43, -135.3) * mm});
            skLineSegment(sketch, "E69.0.34.0", {"start": v(12.7, -136.05) * mm, "end": v(11.43, -136.05) * mm});
            skLineSegment(sketch, "E69.0.34.1", {"start": v(11.43, -136.3) * mm, "end": v(12.7, -136.3) * mm});
            skLineSegment(sketch, "E69.0.34.2", {"start": v(11.43, -136.05) * mm, "end": v(11.43, -136.3) * mm});
            skLineSegment(sketch, "E69.0.35.0", {"start": v(12.7, -137.05) * mm, "end": v(11.43, -137.05) * mm});
            skLineSegment(sketch, "E69.0.35.1", {"start": v(11.43, -137.3) * mm, "end": v(12.7, -137.3) * mm});
            skLineSegment(sketch, "E69.0.35.2", {"start": v(11.43, -137.05) * mm, "end": v(11.43, -137.3) * mm});
            skLineSegment(sketch, "E69.0.36.0", {"start": v(12.7, -138.05) * mm, "end": v(11.43, -138.05) * mm});
            skLineSegment(sketch, "E69.0.36.1", {"start": v(11.43, -138.3) * mm, "end": v(12.7, -138.3) * mm});
            skLineSegment(sketch, "E69.0.36.2", {"start": v(11.43, -138.05) * mm, "end": v(11.43, -138.3) * mm});
            skLineSegment(sketch, "E69.0.37.0", {"start": v(12.7, -139.05) * mm, "end": v(11.43, -139.05) * mm});
            skLineSegment(sketch, "E69.0.37.1", {"start": v(11.43, -139.3) * mm, "end": v(12.7, -139.3) * mm});
            skLineSegment(sketch, "E69.0.37.2", {"start": v(11.43, -139.05) * mm, "end": v(11.43, -139.3) * mm});
            skLineSegment(sketch, "E69.0.38.0", {"start": v(12.7, -140.05) * mm, "end": v(11.43, -140.05) * mm});
            skLineSegment(sketch, "E69.0.38.1", {"start": v(11.43, -140.3) * mm, "end": v(12.7, -140.3) * mm});
            skLineSegment(sketch, "E69.0.38.2", {"start": v(11.43, -140.05) * mm, "end": v(11.43, -140.3) * mm});
            skLineSegment(sketch, "E69.0.39.0", {"start": v(12.7, -141.05) * mm, "end": v(11.43, -141.05) * mm});
            skLineSegment(sketch, "E69.0.39.1", {"start": v(11.43, -141.3) * mm, "end": v(12.7, -141.3) * mm});
            skLineSegment(sketch, "E69.0.39.2", {"start": v(11.43, -141.05) * mm, "end": v(11.43, -141.3) * mm});
            skLineSegment(sketch, "E69.0.40.0", {"start": v(12.7, -142.05) * mm, "end": v(11.43, -142.05) * mm});
            skLineSegment(sketch, "E69.0.40.1", {"start": v(11.43, -142.3) * mm, "end": v(12.7, -142.3) * mm});
            skLineSegment(sketch, "E69.0.40.2", {"start": v(11.43, -142.05) * mm, "end": v(11.43, -142.3) * mm});
            skLineSegment(sketch, "E69.0.41.0", {"start": v(12.7, -143.05) * mm, "end": v(11.43, -143.05) * mm});
            skLineSegment(sketch, "E69.0.41.1", {"start": v(11.43, -143.3) * mm, "end": v(12.7, -143.3) * mm});
            skLineSegment(sketch, "E69.0.41.2", {"start": v(11.43, -143.05) * mm, "end": v(11.43, -143.3) * mm});
            skLineSegment(sketch, "E69.0.42.0", {"start": v(12.7, -144.05) * mm, "end": v(11.43, -144.05) * mm});
            skLineSegment(sketch, "E69.0.42.1", {"start": v(11.43, -144.3) * mm, "end": v(12.7, -144.3) * mm});
            skLineSegment(sketch, "E69.0.42.2", {"start": v(11.43, -144.05) * mm, "end": v(11.43, -144.3) * mm});
            skLineSegment(sketch, "E69.0.43.0", {"start": v(12.7, -145.05) * mm, "end": v(11.43, -145.05) * mm});
            skLineSegment(sketch, "E69.0.43.1", {"start": v(11.43, -145.3) * mm, "end": v(12.7, -145.3) * mm});
            skLineSegment(sketch, "E69.0.43.2", {"start": v(11.43, -145.05) * mm, "end": v(11.43, -145.3) * mm});
            skLineSegment(sketch, "E69.0.44.0", {"start": v(12.7, -146.05) * mm, "end": v(11.43, -146.05) * mm});
            skLineSegment(sketch, "E69.0.44.1", {"start": v(11.43, -146.3) * mm, "end": v(12.7, -146.3) * mm});
            skLineSegment(sketch, "E69.0.44.2", {"start": v(11.43, -146.05) * mm, "end": v(11.43, -146.3) * mm});
            skLineSegment(sketch, "E69.0.45.0", {"start": v(12.7, -147.05) * mm, "end": v(11.43, -147.05) * mm});
            skLineSegment(sketch, "E69.0.45.1", {"start": v(11.43, -147.3) * mm, "end": v(12.7, -147.3) * mm});
            skLineSegment(sketch, "E69.0.45.2", {"start": v(11.43, -147.05) * mm, "end": v(11.43, -147.3) * mm});
            skLineSegment(sketch, "E69.0.46.0", {"start": v(12.7, -148.05) * mm, "end": v(11.43, -148.05) * mm});
            skLineSegment(sketch, "E69.0.46.1", {"start": v(11.43, -148.3) * mm, "end": v(12.7, -148.3) * mm});
            skLineSegment(sketch, "E69.0.46.2", {"start": v(11.43, -148.05) * mm, "end": v(11.43, -148.3) * mm});
            skLineSegment(sketch, "E69.0.47.0", {"start": v(12.7, -149.05) * mm, "end": v(11.43, -149.05) * mm});
            skLineSegment(sketch, "E69.0.47.1", {"start": v(11.43, -149.3) * mm, "end": v(12.7, -149.3) * mm});
            skLineSegment(sketch, "E69.0.47.2", {"start": v(11.43, -149.05) * mm, "end": v(11.43, -149.3) * mm});
            skLineSegment(sketch, "E69.0.48.0", {"start": v(12.7, -150.05) * mm, "end": v(11.43, -150.05) * mm});
            skLineSegment(sketch, "E69.0.48.1", {"start": v(11.43, -150.3) * mm, "end": v(12.7, -150.3) * mm});
            skLineSegment(sketch, "E69.0.48.2", {"start": v(11.43, -150.05) * mm, "end": v(11.43, -150.3) * mm});
            skLineSegment(sketch, "E69.0.49.0", {"start": v(12.7, -151.05) * mm, "end": v(11.43, -151.05) * mm});
            skLineSegment(sketch, "E69.0.49.1", {"start": v(11.43, -151.3) * mm, "end": v(12.7, -151.3) * mm});
            skLineSegment(sketch, "E69.0.49.2", {"start": v(11.43, -151.05) * mm, "end": v(11.43, -151.3) * mm});
            skLineSegment(sketch, "E69.0.50.0", {"start": v(12.7, -152.05) * mm, "end": v(11.43, -152.05) * mm});
            skLineSegment(sketch, "E69.0.50.1", {"start": v(11.43, -152.3) * mm, "end": v(12.7, -152.3) * mm});
            skLineSegment(sketch, "E69.0.50.2", {"start": v(11.43, -152.05) * mm, "end": v(11.43, -152.3) * mm});
            skLineSegment(sketch, "E69.0.51.0", {"start": v(12.7, -153.05) * mm, "end": v(11.43, -153.05) * mm});
            skLineSegment(sketch, "E69.0.51.1", {"start": v(11.43, -153.3) * mm, "end": v(12.7, -153.3) * mm});
            skLineSegment(sketch, "E69.0.51.2", {"start": v(11.43, -153.05) * mm, "end": v(11.43, -153.3) * mm});
            skLineSegment(sketch, "E69.0.52.0", {"start": v(12.7, -154.05) * mm, "end": v(11.43, -154.05) * mm});
            skLineSegment(sketch, "E69.0.52.1", {"start": v(11.43, -154.3) * mm, "end": v(12.7, -154.3) * mm});
            skLineSegment(sketch, "E69.0.52.2", {"start": v(11.43, -154.05) * mm, "end": v(11.43, -154.3) * mm});
            skLineSegment(sketch, "E69.0.53.0", {"start": v(12.7, -155.05) * mm, "end": v(11.43, -155.05) * mm});
            skLineSegment(sketch, "E69.0.53.1", {"start": v(11.43, -155.3) * mm, "end": v(12.7, -155.3) * mm});
            skLineSegment(sketch, "E69.0.53.2", {"start": v(11.43, -155.05) * mm, "end": v(11.43, -155.3) * mm});
            skLineSegment(sketch, "E69.0.54.0", {"start": v(12.7, -156.05) * mm, "end": v(11.43, -156.05) * mm});
            skLineSegment(sketch, "E69.0.54.1", {"start": v(11.43, -156.3) * mm, "end": v(12.7, -156.3) * mm});
            skLineSegment(sketch, "E69.0.54.2", {"start": v(11.43, -156.05) * mm, "end": v(11.43, -156.3) * mm});
            skLineSegment(sketch, "E69.0.55.0", {"start": v(12.7, -157.05) * mm, "end": v(11.43, -157.05) * mm});
            skLineSegment(sketch, "E69.0.55.1", {"start": v(11.43, -157.3) * mm, "end": v(12.7, -157.3) * mm});
            skLineSegment(sketch, "E69.0.55.2", {"start": v(11.43, -157.05) * mm, "end": v(11.43, -157.3) * mm});
            skLineSegment(sketch, "E69.0.56.0", {"start": v(12.7, -158.05) * mm, "end": v(11.43, -158.05) * mm});
            skLineSegment(sketch, "E69.0.56.1", {"start": v(11.43, -158.3) * mm, "end": v(12.7, -158.3) * mm});
            skLineSegment(sketch, "E69.0.56.2", {"start": v(11.43, -158.05) * mm, "end": v(11.43, -158.3) * mm});
            skLineSegment(sketch, "E69.0.57.0", {"start": v(12.7, -159.05) * mm, "end": v(11.43, -159.05) * mm});
            skLineSegment(sketch, "E69.0.57.1", {"start": v(11.43, -159.3) * mm, "end": v(12.7, -159.3) * mm});
            skLineSegment(sketch, "E69.0.57.2", {"start": v(11.43, -159.05) * mm, "end": v(11.43, -159.3) * mm});
            skLineSegment(sketch, "E69.0.58.0", {"start": v(12.7, -160.05) * mm, "end": v(11.43, -160.05) * mm});
            skLineSegment(sketch, "E69.0.58.1", {"start": v(11.43, -160.3) * mm, "end": v(12.7, -160.3) * mm});
            skLineSegment(sketch, "E69.0.58.2", {"start": v(11.43, -160.05) * mm, "end": v(11.43, -160.3) * mm});
            skLineSegment(sketch, "E69.0.59.0", {"start": v(12.7, -161.05) * mm, "end": v(11.43, -161.05) * mm});
            skLineSegment(sketch, "E69.0.59.1", {"start": v(11.43, -161.3) * mm, "end": v(12.7, -161.3) * mm});
            skLineSegment(sketch, "E69.0.59.2", {"start": v(11.43, -161.05) * mm, "end": v(11.43, -161.3) * mm});
            skLineSegment(sketch, "E69.0.60.0", {"start": v(12.7, -162.05) * mm, "end": v(11.43, -162.05) * mm});
            skLineSegment(sketch, "E69.0.60.1", {"start": v(11.43, -162.3) * mm, "end": v(12.7, -162.3) * mm});
            skLineSegment(sketch, "E69.0.60.2", {"start": v(11.43, -162.05) * mm, "end": v(11.43, -162.3) * mm});
            skLineSegment(sketch, "E69.0.61.0", {"start": v(12.7, -163.05) * mm, "end": v(11.43, -163.05) * mm});
            skLineSegment(sketch, "E69.0.61.1", {"start": v(11.43, -163.3) * mm, "end": v(12.7, -163.3) * mm});
            skLineSegment(sketch, "E69.0.61.2", {"start": v(11.43, -163.05) * mm, "end": v(11.43, -163.3) * mm});
            skLineSegment(sketch, "E69.0.62.0", {"start": v(12.7, -164.05) * mm, "end": v(11.43, -164.05) * mm});
            skLineSegment(sketch, "E69.0.62.1", {"start": v(11.43, -164.3) * mm, "end": v(12.7, -164.3) * mm});
            skLineSegment(sketch, "E69.0.62.2", {"start": v(11.43, -164.05) * mm, "end": v(11.43, -164.3) * mm});
            skLineSegment(sketch, "E69.0.63.0", {"start": v(12.7, -165.05) * mm, "end": v(11.43, -165.05) * mm});
            skLineSegment(sketch, "E69.0.63.1", {"start": v(11.43, -165.3) * mm, "end": v(12.7, -165.3) * mm});
            skLineSegment(sketch, "E69.0.63.2", {"start": v(11.43, -165.05) * mm, "end": v(11.43, -165.3) * mm});
            skLineSegment(sketch, "E69.0.64.0", {"start": v(12.7, -166.05) * mm, "end": v(11.43, -166.05) * mm});
            skLineSegment(sketch, "E69.0.64.1", {"start": v(11.43, -166.3) * mm, "end": v(12.7, -166.3) * mm});
            skLineSegment(sketch, "E69.0.64.2", {"start": v(11.43, -166.05) * mm, "end": v(11.43, -166.3) * mm});
            skLineSegment(sketch, "E69.0.65.0", {"start": v(12.7, -167.05) * mm, "end": v(11.43, -167.05) * mm});
            skLineSegment(sketch, "E69.0.65.1", {"start": v(11.43, -167.3) * mm, "end": v(12.7, -167.3) * mm});
            skLineSegment(sketch, "E69.0.65.2", {"start": v(11.43, -167.05) * mm, "end": v(11.43, -167.3) * mm});
            skLineSegment(sketch, "E69.0.66.0", {"start": v(12.7, -168.05) * mm, "end": v(11.43, -168.05) * mm});
            skLineSegment(sketch, "E69.0.66.1", {"start": v(11.43, -168.3) * mm, "end": v(12.7, -168.3) * mm});
            skLineSegment(sketch, "E69.0.66.2", {"start": v(11.43, -168.05) * mm, "end": v(11.43, -168.3) * mm});
            skLineSegment(sketch, "E69.0.67.0", {"start": v(12.7, -169.05) * mm, "end": v(11.43, -169.05) * mm});
            skLineSegment(sketch, "E69.0.67.1", {"start": v(11.43, -169.3) * mm, "end": v(12.7, -169.3) * mm});
            skLineSegment(sketch, "E69.0.67.2", {"start": v(11.43, -169.05) * mm, "end": v(11.43, -169.3) * mm});
            skLineSegment(sketch, "E69.0.68.0", {"start": v(12.7, -170.05) * mm, "end": v(11.43, -170.05) * mm});
            skLineSegment(sketch, "E69.0.68.1", {"start": v(11.43, -170.3) * mm, "end": v(12.7, -170.3) * mm});
            skLineSegment(sketch, "E69.0.68.2", {"start": v(11.43, -170.05) * mm, "end": v(11.43, -170.3) * mm});
            skLineSegment(sketch, "E69.0.69.0", {"start": v(12.7, -171.05) * mm, "end": v(11.43, -171.05) * mm});
            skLineSegment(sketch, "E69.0.69.1", {"start": v(11.43, -171.3) * mm, "end": v(12.7, -171.3) * mm});
            skLineSegment(sketch, "E69.0.69.2", {"start": v(11.43, -171.05) * mm, "end": v(11.43, -171.3) * mm});
            skLineSegment(sketch, "E69.0.70.0", {"start": v(12.7, -172.05) * mm, "end": v(11.43, -172.05) * mm});
            skLineSegment(sketch, "E69.0.70.1", {"start": v(11.43, -172.3) * mm, "end": v(12.7, -172.3) * mm});
            skLineSegment(sketch, "E69.0.70.2", {"start": v(11.43, -172.05) * mm, "end": v(11.43, -172.3) * mm});
            skLineSegment(sketch, "E69.0.71.0", {"start": v(12.7, -173.05) * mm, "end": v(11.43, -173.05) * mm});
            skLineSegment(sketch, "E69.0.71.1", {"start": v(11.43, -173.3) * mm, "end": v(12.7, -173.3) * mm});
            skLineSegment(sketch, "E69.0.71.2", {"start": v(11.43, -173.05) * mm, "end": v(11.43, -173.3) * mm});
            skLineSegment(sketch, "E69.0.72.0", {"start": v(12.7, -174.05) * mm, "end": v(11.43, -174.05) * mm});
            skLineSegment(sketch, "E69.0.72.1", {"start": v(11.43, -174.3) * mm, "end": v(12.7, -174.3) * mm});
            skLineSegment(sketch, "E69.0.72.2", {"start": v(11.43, -174.05) * mm, "end": v(11.43, -174.3) * mm});
            skLineSegment(sketch, "E69.0.73.0", {"start": v(12.7, -175.05) * mm, "end": v(11.43, -175.05) * mm});
            skLineSegment(sketch, "E69.0.73.1", {"start": v(11.43, -175.3) * mm, "end": v(12.7, -175.3) * mm});
            skLineSegment(sketch, "E69.0.73.2", {"start": v(11.43, -175.05) * mm, "end": v(11.43, -175.3) * mm});
            skLineSegment(sketch, "E69.0.74.0", {"start": v(12.7, -176.05) * mm, "end": v(11.43, -176.05) * mm});
            skLineSegment(sketch, "E69.0.74.1", {"start": v(11.43, -176.3) * mm, "end": v(12.7, -176.3) * mm});
            skLineSegment(sketch, "E69.0.74.2", {"start": v(11.43, -176.05) * mm, "end": v(11.43, -176.3) * mm});
            skLineSegment(sketch, "E69.0.75.0", {"start": v(12.7, -177.05) * mm, "end": v(11.43, -177.05) * mm});
            skLineSegment(sketch, "E69.0.75.1", {"start": v(11.43, -177.3) * mm, "end": v(12.7, -177.3) * mm});
            skLineSegment(sketch, "E69.0.75.2", {"start": v(11.43, -177.05) * mm, "end": v(11.43, -177.3) * mm});
            skLineSegment(sketch, "E69.0.76.0", {"start": v(12.7, -178.05) * mm, "end": v(11.43, -178.05) * mm});
            skLineSegment(sketch, "E69.0.76.1", {"start": v(11.43, -178.3) * mm, "end": v(12.7, -178.3) * mm});
            skLineSegment(sketch, "E69.0.76.2", {"start": v(11.43, -178.05) * mm, "end": v(11.43, -178.3) * mm});
            skLineSegment(sketch, "E69.0.77.0", {"start": v(12.7, -179.05) * mm, "end": v(11.43, -179.05) * mm});
            skLineSegment(sketch, "E69.0.77.1", {"start": v(11.43, -179.3) * mm, "end": v(12.7, -179.3) * mm});
            skLineSegment(sketch, "E69.0.77.2", {"start": v(11.43, -179.05) * mm, "end": v(11.43, -179.3) * mm});
            skLineSegment(sketch, "E69.0.78.0", {"start": v(12.7, -180.05) * mm, "end": v(11.43, -180.05) * mm});
            skLineSegment(sketch, "E69.0.78.1", {"start": v(11.43, -180.3) * mm, "end": v(12.7, -180.3) * mm});
            skLineSegment(sketch, "E69.0.78.2", {"start": v(11.43, -180.05) * mm, "end": v(11.43, -180.3) * mm});
            skLineSegment(sketch, "E69.0.79.0", {"start": v(12.7, -181.05) * mm, "end": v(11.43, -181.05) * mm});
            skLineSegment(sketch, "E69.0.79.1", {"start": v(11.43, -181.3) * mm, "end": v(12.7, -181.3) * mm});
            skLineSegment(sketch, "E69.0.79.2", {"start": v(11.43, -181.05) * mm, "end": v(11.43, -181.3) * mm});
            skLineSegment(sketch, "E69.0.80.0", {"start": v(12.7, -182.05) * mm, "end": v(11.43, -182.05) * mm});
            skLineSegment(sketch, "E69.0.80.1", {"start": v(11.43, -182.3) * mm, "end": v(12.7, -182.3) * mm});
            skLineSegment(sketch, "E69.0.80.2", {"start": v(11.43, -182.05) * mm, "end": v(11.43, -182.3) * mm});
            skLineSegment(sketch, "E69.0.81.0", {"start": v(12.7, -183.05) * mm, "end": v(11.43, -183.05) * mm});
            skLineSegment(sketch, "E69.0.81.1", {"start": v(11.43, -183.3) * mm, "end": v(12.7, -183.3) * mm});
            skLineSegment(sketch, "E69.0.81.2", {"start": v(11.43, -183.05) * mm, "end": v(11.43, -183.3) * mm});
            skLineSegment(sketch, "E69.0.82.0", {"start": v(12.7, -184.05) * mm, "end": v(11.43, -184.05) * mm});
            skLineSegment(sketch, "E69.0.82.1", {"start": v(11.43, -184.3) * mm, "end": v(12.7, -184.3) * mm});
            skLineSegment(sketch, "E69.0.82.2", {"start": v(11.43, -184.05) * mm, "end": v(11.43, -184.3) * mm});
            skLineSegment(sketch, "E69.0.83.0", {"start": v(12.7, -185.05) * mm, "end": v(11.43, -185.05) * mm});
            skLineSegment(sketch, "E69.0.83.1", {"start": v(11.43, -185.3) * mm, "end": v(12.7, -185.3) * mm});
            skLineSegment(sketch, "E69.0.83.2", {"start": v(11.43, -185.05) * mm, "end": v(11.43, -185.3) * mm});
            skLineSegment(sketch, "E69.0.84.0", {"start": v(12.7, -186.05) * mm, "end": v(11.43, -186.05) * mm});
            skLineSegment(sketch, "E69.0.84.1", {"start": v(11.43, -186.3) * mm, "end": v(12.7, -186.3) * mm});
            skLineSegment(sketch, "E69.0.84.2", {"start": v(11.43, -186.05) * mm, "end": v(11.43, -186.3) * mm});
            skLineSegment(sketch, "E69.0.85.0", {"start": v(12.7, -187.05) * mm, "end": v(11.43, -187.05) * mm});
            skLineSegment(sketch, "E69.0.85.1", {"start": v(11.43, -187.3) * mm, "end": v(12.7, -187.3) * mm});
            skLineSegment(sketch, "E69.0.85.2", {"start": v(11.43, -187.05) * mm, "end": v(11.43, -187.3) * mm});
            skLineSegment(sketch, "E69.0.86.0", {"start": v(12.7, -188.05) * mm, "end": v(11.43, -188.05) * mm});
            skLineSegment(sketch, "E69.0.86.1", {"start": v(11.43, -188.3) * mm, "end": v(12.7, -188.3) * mm});
            skLineSegment(sketch, "E69.0.86.2", {"start": v(11.43, -188.05) * mm, "end": v(11.43, -188.3) * mm});
            skLineSegment(sketch, "E69.0.87.0", {"start": v(12.7, -189.05) * mm, "end": v(11.43, -189.05) * mm});
            skLineSegment(sketch, "E69.0.87.1", {"start": v(11.43, -189.3) * mm, "end": v(12.7, -189.3) * mm});
            skLineSegment(sketch, "E69.0.87.2", {"start": v(11.43, -189.05) * mm, "end": v(11.43, -189.3) * mm});
            skLineSegment(sketch, "E69.0.88.0", {"start": v(12.7, -190.05) * mm, "end": v(11.43, -190.05) * mm});
            skLineSegment(sketch, "E69.0.88.1", {"start": v(11.43, -190.3) * mm, "end": v(12.7, -190.3) * mm});
            skLineSegment(sketch, "E69.0.88.2", {"start": v(11.43, -190.05) * mm, "end": v(11.43, -190.3) * mm});
            skLineSegment(sketch, "E69.0.89.0", {"start": v(12.7, -191.05) * mm, "end": v(11.43, -191.05) * mm});
            skLineSegment(sketch, "E69.0.89.1", {"start": v(11.43, -191.3) * mm, "end": v(12.7, -191.3) * mm});
            skLineSegment(sketch, "E69.0.89.2", {"start": v(11.43, -191.05) * mm, "end": v(11.43, -191.3) * mm});
            skLineSegment(sketch, "E69.0.90.0", {"start": v(12.7, -192.05) * mm, "end": v(11.43, -192.05) * mm});
            skLineSegment(sketch, "E69.0.90.1", {"start": v(11.43, -192.3) * mm, "end": v(12.7, -192.3) * mm});
            skLineSegment(sketch, "E69.0.90.2", {"start": v(11.43, -192.05) * mm, "end": v(11.43, -192.3) * mm});
            skLineSegment(sketch, "E69.0.91.0", {"start": v(12.7, -193.05) * mm, "end": v(11.43, -193.05) * mm});
            skLineSegment(sketch, "E69.0.91.1", {"start": v(11.43, -193.3) * mm, "end": v(12.7, -193.3) * mm});
            skLineSegment(sketch, "E69.0.91.2", {"start": v(11.43, -193.05) * mm, "end": v(11.43, -193.3) * mm});
            skLineSegment(sketch, "E69.0.92.0", {"start": v(12.7, -194.05) * mm, "end": v(11.43, -194.05) * mm});
            skLineSegment(sketch, "E69.0.92.1", {"start": v(11.43, -194.3) * mm, "end": v(12.7, -194.3) * mm});
            skLineSegment(sketch, "E69.0.92.2", {"start": v(11.43, -194.05) * mm, "end": v(11.43, -194.3) * mm});
            skLineSegment(sketch, "E69.0.93.0", {"start": v(12.7, -195.05) * mm, "end": v(11.43, -195.05) * mm});
            skLineSegment(sketch, "E69.0.93.1", {"start": v(11.43, -195.3) * mm, "end": v(12.7, -195.3) * mm});
            skLineSegment(sketch, "E69.0.93.2", {"start": v(11.43, -195.05) * mm, "end": v(11.43, -195.3) * mm});
            skLineSegment(sketch, "E69.0.94.0", {"start": v(12.7, -196.05) * mm, "end": v(11.43, -196.05) * mm});
            skLineSegment(sketch, "E69.0.94.1", {"start": v(11.43, -196.3) * mm, "end": v(12.7, -196.3) * mm});
            skLineSegment(sketch, "E69.0.94.2", {"start": v(11.43, -196.05) * mm, "end": v(11.43, -196.3) * mm});
            skLineSegment(sketch, "E69.0.95.0", {"start": v(12.7, -197.05) * mm, "end": v(11.43, -197.05) * mm});
            skLineSegment(sketch, "E69.0.95.1", {"start": v(11.43, -197.3) * mm, "end": v(12.7, -197.3) * mm});
            skLineSegment(sketch, "E69.0.95.2", {"start": v(11.43, -197.05) * mm, "end": v(11.43, -197.3) * mm});
            skLineSegment(sketch, "E69.0.96.0", {"start": v(12.7, -198.05) * mm, "end": v(11.43, -198.05) * mm});
            skLineSegment(sketch, "E69.0.96.1", {"start": v(11.43, -198.3) * mm, "end": v(12.7, -198.3) * mm});
            skLineSegment(sketch, "E69.0.96.2", {"start": v(11.43, -198.05) * mm, "end": v(11.43, -198.3) * mm});
            skLineSegment(sketch, "E69.0.97.0", {"start": v(12.7, -199.05) * mm, "end": v(11.43, -199.05) * mm});
            skLineSegment(sketch, "E69.0.97.1", {"start": v(11.43, -199.3) * mm, "end": v(12.7, -199.3) * mm});
            skLineSegment(sketch, "E69.0.97.2", {"start": v(11.43, -199.05) * mm, "end": v(11.43, -199.3) * mm});
            skLineSegment(sketch, "E69.0.98.0", {"start": v(12.7, -200.05) * mm, "end": v(11.43, -200.05) * mm});
            skLineSegment(sketch, "E69.0.98.1", {"start": v(11.43, -200.3) * mm, "end": v(12.7, -200.3) * mm});
            skLineSegment(sketch, "E69.0.98.2", {"start": v(11.43, -200.05) * mm, "end": v(11.43, -200.3) * mm});
            skLineSegment(sketch, "E69.0.99.0", {"start": v(12.7, -201.05) * mm, "end": v(11.43, -201.05) * mm});
            skLineSegment(sketch, "E69.0.99.1", {"start": v(11.43, -201.3) * mm, "end": v(12.7, -201.3) * mm});
            skLineSegment(sketch, "E69.0.99.2", {"start": v(11.43, -201.05) * mm, "end": v(11.43, -201.3) * mm});
            skLineSegment(sketch, "E69.direction1", {"start": v(11.43, -102.05) * mm, "end": v(36.83, -102.05) * mm, "construction": true});
            skLineSegment(sketch, "E69.direction2", {"start": v(11.43, -102.05) * mm, "end": v(11.43, -103.05) * mm, "construction": true});
            skLineSegment(sketch, "E70.0.1.0", {"start": v(12.7, -202.05) * mm, "end": v(11.43, -202.05) * mm});
            skLineSegment(sketch, "E70.0.1.1", {"start": v(11.43, -202.05) * mm, "end": v(11.43, -202.3) * mm});
            skLineSegment(sketch, "E70.0.1.2", {"start": v(11.43, -202.3) * mm, "end": v(12.7, -202.3) * mm});
            skLineSegment(sketch, "E70.0.2.0", {"start": v(12.7, -203.05) * mm, "end": v(11.43, -203.05) * mm});
            skLineSegment(sketch, "E70.0.2.1", {"start": v(11.43, -203.05) * mm, "end": v(11.43, -203.3) * mm});
            skLineSegment(sketch, "E70.0.2.2", {"start": v(11.43, -203.3) * mm, "end": v(12.7, -203.3) * mm});
            skLineSegment(sketch, "E70.0.3.0", {"start": v(12.7, -204.05) * mm, "end": v(11.43, -204.05) * mm});
            skLineSegment(sketch, "E70.0.3.1", {"start": v(11.43, -204.05) * mm, "end": v(11.43, -204.3) * mm});
            skLineSegment(sketch, "E70.0.3.2", {"start": v(11.43, -204.3) * mm, "end": v(12.7, -204.3) * mm});
            skLineSegment(sketch, "E70.0.4.0", {"start": v(12.7, -205.05) * mm, "end": v(11.43, -205.05) * mm});
            skLineSegment(sketch, "E70.0.4.1", {"start": v(11.43, -205.05) * mm, "end": v(11.43, -205.3) * mm});
            skLineSegment(sketch, "E70.0.4.2", {"start": v(11.43, -205.3) * mm, "end": v(12.7, -205.3) * mm});
            skLineSegment(sketch, "E70.0.5.0", {"start": v(12.7, -206.05) * mm, "end": v(11.43, -206.05) * mm});
            skLineSegment(sketch, "E70.0.5.1", {"start": v(11.43, -206.05) * mm, "end": v(11.43, -206.3) * mm});
            skLineSegment(sketch, "E70.0.5.2", {"start": v(11.43, -206.3) * mm, "end": v(12.7, -206.3) * mm});
            skLineSegment(sketch, "E70.0.6.0", {"start": v(12.7, -207.05) * mm, "end": v(11.43, -207.05) * mm});
            skLineSegment(sketch, "E70.0.6.1", {"start": v(11.43, -207.05) * mm, "end": v(11.43, -207.3) * mm});
            skLineSegment(sketch, "E70.0.6.2", {"start": v(11.43, -207.3) * mm, "end": v(12.7, -207.3) * mm});
            skLineSegment(sketch, "E70.0.7.0", {"start": v(12.7, -208.05) * mm, "end": v(11.43, -208.05) * mm});
            skLineSegment(sketch, "E70.0.7.1", {"start": v(11.43, -208.05) * mm, "end": v(11.43, -208.3) * mm});
            skLineSegment(sketch, "E70.0.7.2", {"start": v(11.43, -208.3) * mm, "end": v(12.7, -208.3) * mm});
            skLineSegment(sketch, "E70.0.8.0", {"start": v(12.7, -209.05) * mm, "end": v(11.43, -209.05) * mm});
            skLineSegment(sketch, "E70.0.8.1", {"start": v(11.43, -209.05) * mm, "end": v(11.43, -209.3) * mm});
            skLineSegment(sketch, "E70.0.8.2", {"start": v(11.43, -209.3) * mm, "end": v(12.7, -209.3) * mm});
            skLineSegment(sketch, "E70.0.9.0", {"start": v(12.7, -210.05) * mm, "end": v(11.43, -210.05) * mm});
            skLineSegment(sketch, "E70.0.9.1", {"start": v(11.43, -210.05) * mm, "end": v(11.43, -210.3) * mm});
            skLineSegment(sketch, "E70.0.9.2", {"start": v(11.43, -210.3) * mm, "end": v(12.7, -210.3) * mm});
            skLineSegment(sketch, "E70.0.10.0", {"start": v(12.7, -211.05) * mm, "end": v(11.43, -211.05) * mm});
            skLineSegment(sketch, "E70.0.10.1", {"start": v(11.43, -211.05) * mm, "end": v(11.43, -211.3) * mm});
            skLineSegment(sketch, "E70.0.10.2", {"start": v(11.43, -211.3) * mm, "end": v(12.7, -211.3) * mm});
            skLineSegment(sketch, "E70.0.11.0", {"start": v(12.7, -212.05) * mm, "end": v(11.43, -212.05) * mm});
            skLineSegment(sketch, "E70.0.11.1", {"start": v(11.43, -212.05) * mm, "end": v(11.43, -212.3) * mm});
            skLineSegment(sketch, "E70.0.11.2", {"start": v(11.43, -212.3) * mm, "end": v(12.7, -212.3) * mm});
            skLineSegment(sketch, "E70.0.12.0", {"start": v(12.7, -213.05) * mm, "end": v(11.43, -213.05) * mm});
            skLineSegment(sketch, "E70.0.12.1", {"start": v(11.43, -213.05) * mm, "end": v(11.43, -213.3) * mm});
            skLineSegment(sketch, "E70.0.12.2", {"start": v(11.43, -213.3) * mm, "end": v(12.7, -213.3) * mm});
            skLineSegment(sketch, "E70.0.13.0", {"start": v(12.7, -214.05) * mm, "end": v(11.43, -214.05) * mm});
            skLineSegment(sketch, "E70.0.13.1", {"start": v(11.43, -214.05) * mm, "end": v(11.43, -214.3) * mm});
            skLineSegment(sketch, "E70.0.13.2", {"start": v(11.43, -214.3) * mm, "end": v(12.7, -214.3) * mm});
            skLineSegment(sketch, "E70.0.14.0", {"start": v(12.7, -215.05) * mm, "end": v(11.43, -215.05) * mm});
            skLineSegment(sketch, "E70.0.14.1", {"start": v(11.43, -215.05) * mm, "end": v(11.43, -215.3) * mm});
            skLineSegment(sketch, "E70.0.14.2", {"start": v(11.43, -215.3) * mm, "end": v(12.7, -215.3) * mm});
            skLineSegment(sketch, "E70.0.15.0", {"start": v(12.7, -216.05) * mm, "end": v(11.43, -216.05) * mm});
            skLineSegment(sketch, "E70.0.15.1", {"start": v(11.43, -216.05) * mm, "end": v(11.43, -216.3) * mm});
            skLineSegment(sketch, "E70.0.15.2", {"start": v(11.43, -216.3) * mm, "end": v(12.7, -216.3) * mm});
            skLineSegment(sketch, "E70.0.16.0", {"start": v(12.7, -217.05) * mm, "end": v(11.43, -217.05) * mm});
            skLineSegment(sketch, "E70.0.16.1", {"start": v(11.43, -217.05) * mm, "end": v(11.43, -217.3) * mm});
            skLineSegment(sketch, "E70.0.16.2", {"start": v(11.43, -217.3) * mm, "end": v(12.7, -217.3) * mm});
            skLineSegment(sketch, "E70.0.17.0", {"start": v(12.7, -218.05) * mm, "end": v(11.43, -218.05) * mm});
            skLineSegment(sketch, "E70.0.17.1", {"start": v(11.43, -218.05) * mm, "end": v(11.43, -218.3) * mm});
            skLineSegment(sketch, "E70.0.17.2", {"start": v(11.43, -218.3) * mm, "end": v(12.7, -218.3) * mm});
            skLineSegment(sketch, "E70.0.18.0", {"start": v(12.7, -219.05) * mm, "end": v(11.43, -219.05) * mm});
            skLineSegment(sketch, "E70.0.18.1", {"start": v(11.43, -219.05) * mm, "end": v(11.43, -219.3) * mm});
            skLineSegment(sketch, "E70.0.18.2", {"start": v(11.43, -219.3) * mm, "end": v(12.7, -219.3) * mm});
            skLineSegment(sketch, "E70.0.19.0", {"start": v(12.7, -220.05) * mm, "end": v(11.43, -220.05) * mm});
            skLineSegment(sketch, "E70.0.19.1", {"start": v(11.43, -220.05) * mm, "end": v(11.43, -220.3) * mm});
            skLineSegment(sketch, "E70.0.19.2", {"start": v(11.43, -220.3) * mm, "end": v(12.7, -220.3) * mm});
            skLineSegment(sketch, "E70.0.20.0", {"start": v(12.7, -221.05) * mm, "end": v(11.43, -221.05) * mm});
            skLineSegment(sketch, "E70.0.20.1", {"start": v(11.43, -221.05) * mm, "end": v(11.43, -221.3) * mm});
            skLineSegment(sketch, "E70.0.20.2", {"start": v(11.43, -221.3) * mm, "end": v(12.7, -221.3) * mm});
            skLineSegment(sketch, "E70.0.21.0", {"start": v(12.7, -222.05) * mm, "end": v(11.43, -222.05) * mm});
            skLineSegment(sketch, "E70.0.21.1", {"start": v(11.43, -222.05) * mm, "end": v(11.43, -222.3) * mm});
            skLineSegment(sketch, "E70.0.21.2", {"start": v(11.43, -222.3) * mm, "end": v(12.7, -222.3) * mm});
            skLineSegment(sketch, "E70.0.22.0", {"start": v(12.7, -223.05) * mm, "end": v(11.43, -223.05) * mm});
            skLineSegment(sketch, "E70.0.22.1", {"start": v(11.43, -223.05) * mm, "end": v(11.43, -223.3) * mm});
            skLineSegment(sketch, "E70.0.22.2", {"start": v(11.43, -223.3) * mm, "end": v(12.7, -223.3) * mm});
            skLineSegment(sketch, "E70.0.23.0", {"start": v(12.7, -224.05) * mm, "end": v(11.43, -224.05) * mm});
            skLineSegment(sketch, "E70.0.23.1", {"start": v(11.43, -224.05) * mm, "end": v(11.43, -224.3) * mm});
            skLineSegment(sketch, "E70.0.23.2", {"start": v(11.43, -224.3) * mm, "end": v(12.7, -224.3) * mm});
            skLineSegment(sketch, "E70.0.24.0", {"start": v(12.7, -225.05) * mm, "end": v(11.43, -225.05) * mm});
            skLineSegment(sketch, "E70.0.24.1", {"start": v(11.43, -225.05) * mm, "end": v(11.43, -225.3) * mm});
            skLineSegment(sketch, "E70.0.24.2", {"start": v(11.43, -225.3) * mm, "end": v(12.7, -225.3) * mm});
            skLineSegment(sketch, "E70.0.25.0", {"start": v(12.7, -226.05) * mm, "end": v(11.43, -226.05) * mm});
            skLineSegment(sketch, "E70.0.25.1", {"start": v(11.43, -226.05) * mm, "end": v(11.43, -226.3) * mm});
            skLineSegment(sketch, "E70.0.25.2", {"start": v(11.43, -226.3) * mm, "end": v(12.7, -226.3) * mm});
            skLineSegment(sketch, "E70.0.26.0", {"start": v(12.7, -227.05) * mm, "end": v(11.43, -227.05) * mm});
            skLineSegment(sketch, "E70.0.26.1", {"start": v(11.43, -227.05) * mm, "end": v(11.43, -227.3) * mm});
            skLineSegment(sketch, "E70.0.26.2", {"start": v(11.43, -227.3) * mm, "end": v(12.7, -227.3) * mm});
            skLineSegment(sketch, "E70.0.27.0", {"start": v(12.7, -228.05) * mm, "end": v(11.43, -228.05) * mm});
            skLineSegment(sketch, "E70.0.27.1", {"start": v(11.43, -228.05) * mm, "end": v(11.43, -228.3) * mm});
            skLineSegment(sketch, "E70.0.27.2", {"start": v(11.43, -228.3) * mm, "end": v(12.7, -228.3) * mm});
            skLineSegment(sketch, "E70.0.28.0", {"start": v(12.7, -229.05) * mm, "end": v(11.43, -229.05) * mm});
            skLineSegment(sketch, "E70.0.28.1", {"start": v(11.43, -229.05) * mm, "end": v(11.43, -229.3) * mm});
            skLineSegment(sketch, "E70.0.28.2", {"start": v(11.43, -229.3) * mm, "end": v(12.7, -229.3) * mm});
            skLineSegment(sketch, "E70.0.29.0", {"start": v(12.7, -230.05) * mm, "end": v(11.43, -230.05) * mm});
            skLineSegment(sketch, "E70.0.29.1", {"start": v(11.43, -230.05) * mm, "end": v(11.43, -230.3) * mm});
            skLineSegment(sketch, "E70.0.29.2", {"start": v(11.43, -230.3) * mm, "end": v(12.7, -230.3) * mm});
            skLineSegment(sketch, "E70.0.30.0", {"start": v(12.7, -231.05) * mm, "end": v(11.43, -231.05) * mm});
            skLineSegment(sketch, "E70.0.30.1", {"start": v(11.43, -231.05) * mm, "end": v(11.43, -231.3) * mm});
            skLineSegment(sketch, "E70.0.30.2", {"start": v(11.43, -231.3) * mm, "end": v(12.7, -231.3) * mm});
            skLineSegment(sketch, "E70.0.31.0", {"start": v(12.7, -232.05) * mm, "end": v(11.43, -232.05) * mm});
            skLineSegment(sketch, "E70.0.31.1", {"start": v(11.43, -232.05) * mm, "end": v(11.43, -232.3) * mm});
            skLineSegment(sketch, "E70.0.31.2", {"start": v(11.43, -232.3) * mm, "end": v(12.7, -232.3) * mm});
            skLineSegment(sketch, "E70.0.32.0", {"start": v(12.7, -233.05) * mm, "end": v(11.43, -233.05) * mm});
            skLineSegment(sketch, "E70.0.32.1", {"start": v(11.43, -233.05) * mm, "end": v(11.43, -233.3) * mm});
            skLineSegment(sketch, "E70.0.32.2", {"start": v(11.43, -233.3) * mm, "end": v(12.7, -233.3) * mm});
            skLineSegment(sketch, "E70.0.33.0", {"start": v(12.7, -234.05) * mm, "end": v(11.43, -234.05) * mm});
            skLineSegment(sketch, "E70.0.33.1", {"start": v(11.43, -234.05) * mm, "end": v(11.43, -234.3) * mm});
            skLineSegment(sketch, "E70.0.33.2", {"start": v(11.43, -234.3) * mm, "end": v(12.7, -234.3) * mm});
            skLineSegment(sketch, "E70.0.34.0", {"start": v(12.7, -235.05) * mm, "end": v(11.43, -235.05) * mm});
            skLineSegment(sketch, "E70.0.34.1", {"start": v(11.43, -235.05) * mm, "end": v(11.43, -235.3) * mm});
            skLineSegment(sketch, "E70.0.34.2", {"start": v(11.43, -235.3) * mm, "end": v(12.7, -235.3) * mm});
            skLineSegment(sketch, "E70.0.35.0", {"start": v(12.7, -236.05) * mm, "end": v(11.43, -236.05) * mm});
            skLineSegment(sketch, "E70.0.35.1", {"start": v(11.43, -236.05) * mm, "end": v(11.43, -236.3) * mm});
            skLineSegment(sketch, "E70.0.35.2", {"start": v(11.43, -236.3) * mm, "end": v(12.7, -236.3) * mm});
            skLineSegment(sketch, "E70.0.36.0", {"start": v(12.7, -237.05) * mm, "end": v(11.43, -237.05) * mm});
            skLineSegment(sketch, "E70.0.36.1", {"start": v(11.43, -237.05) * mm, "end": v(11.43, -237.3) * mm});
            skLineSegment(sketch, "E70.0.36.2", {"start": v(11.43, -237.3) * mm, "end": v(12.7, -237.3) * mm});
            skLineSegment(sketch, "E70.0.37.0", {"start": v(12.7, -238.05) * mm, "end": v(11.43, -238.05) * mm});
            skLineSegment(sketch, "E70.0.37.1", {"start": v(11.43, -238.05) * mm, "end": v(11.43, -238.3) * mm});
            skLineSegment(sketch, "E70.0.37.2", {"start": v(11.43, -238.3) * mm, "end": v(12.7, -238.3) * mm});
            skLineSegment(sketch, "E70.0.38.0", {"start": v(12.7, -239.05) * mm, "end": v(11.43, -239.05) * mm});
            skLineSegment(sketch, "E70.0.38.1", {"start": v(11.43, -239.05) * mm, "end": v(11.43, -239.3) * mm});
            skLineSegment(sketch, "E70.0.38.2", {"start": v(11.43, -239.3) * mm, "end": v(12.7, -239.3) * mm});
            skLineSegment(sketch, "E70.0.39.0", {"start": v(12.7, -240.05) * mm, "end": v(11.43, -240.05) * mm});
            skLineSegment(sketch, "E70.0.39.1", {"start": v(11.43, -240.05) * mm, "end": v(11.43, -240.3) * mm});
            skLineSegment(sketch, "E70.0.39.2", {"start": v(11.43, -240.3) * mm, "end": v(12.7, -240.3) * mm});
            skLineSegment(sketch, "E70.0.40.0", {"start": v(12.7, -241.05) * mm, "end": v(11.43, -241.05) * mm});
            skLineSegment(sketch, "E70.0.40.1", {"start": v(11.43, -241.05) * mm, "end": v(11.43, -241.3) * mm});
            skLineSegment(sketch, "E70.0.40.2", {"start": v(11.43, -241.3) * mm, "end": v(12.7, -241.3) * mm});
            skLineSegment(sketch, "E70.0.41.0", {"start": v(12.7, -242.05) * mm, "end": v(11.43, -242.05) * mm});
            skLineSegment(sketch, "E70.0.41.1", {"start": v(11.43, -242.05) * mm, "end": v(11.43, -242.3) * mm});
            skLineSegment(sketch, "E70.0.41.2", {"start": v(11.43, -242.3) * mm, "end": v(12.7, -242.3) * mm});
            skLineSegment(sketch, "E70.0.42.0", {"start": v(12.7, -243.05) * mm, "end": v(11.43, -243.05) * mm});
            skLineSegment(sketch, "E70.0.42.1", {"start": v(11.43, -243.05) * mm, "end": v(11.43, -243.3) * mm});
            skLineSegment(sketch, "E70.0.42.2", {"start": v(11.43, -243.3) * mm, "end": v(12.7, -243.3) * mm});
            skLineSegment(sketch, "E70.0.43.0", {"start": v(12.7, -244.05) * mm, "end": v(11.43, -244.05) * mm});
            skLineSegment(sketch, "E70.0.43.1", {"start": v(11.43, -244.05) * mm, "end": v(11.43, -244.3) * mm});
            skLineSegment(sketch, "E70.0.43.2", {"start": v(11.43, -244.3) * mm, "end": v(12.7, -244.3) * mm});
            skLineSegment(sketch, "E70.0.44.0", {"start": v(12.7, -245.05) * mm, "end": v(11.43, -245.05) * mm});
            skLineSegment(sketch, "E70.0.44.1", {"start": v(11.43, -245.05) * mm, "end": v(11.43, -245.3) * mm});
            skLineSegment(sketch, "E70.0.44.2", {"start": v(11.43, -245.3) * mm, "end": v(12.7, -245.3) * mm});
            skLineSegment(sketch, "E70.0.45.0", {"start": v(12.7, -246.05) * mm, "end": v(11.43, -246.05) * mm});
            skLineSegment(sketch, "E70.0.45.1", {"start": v(11.43, -246.05) * mm, "end": v(11.43, -246.3) * mm});
            skLineSegment(sketch, "E70.0.45.2", {"start": v(11.43, -246.3) * mm, "end": v(12.7, -246.3) * mm});
            skLineSegment(sketch, "E70.0.46.0", {"start": v(12.7, -247.05) * mm, "end": v(11.43, -247.05) * mm});
            skLineSegment(sketch, "E70.0.46.1", {"start": v(11.43, -247.05) * mm, "end": v(11.43, -247.3) * mm});
            skLineSegment(sketch, "E70.0.46.2", {"start": v(11.43, -247.3) * mm, "end": v(12.7, -247.3) * mm});
            skLineSegment(sketch, "E70.0.47.0", {"start": v(12.7, -248.05) * mm, "end": v(11.43, -248.05) * mm});
            skLineSegment(sketch, "E70.0.47.1", {"start": v(11.43, -248.05) * mm, "end": v(11.43, -248.3) * mm});
            skLineSegment(sketch, "E70.0.47.2", {"start": v(11.43, -248.3) * mm, "end": v(12.7, -248.3) * mm});
            skLineSegment(sketch, "E70.0.48.0", {"start": v(12.7, -249.05) * mm, "end": v(11.43, -249.05) * mm});
            skLineSegment(sketch, "E70.0.48.1", {"start": v(11.43, -249.05) * mm, "end": v(11.43, -249.3) * mm});
            skLineSegment(sketch, "E70.0.48.2", {"start": v(11.43, -249.3) * mm, "end": v(12.7, -249.3) * mm});
            skLineSegment(sketch, "E70.0.49.0", {"start": v(12.7, -250.05) * mm, "end": v(11.43, -250.05) * mm});
            skLineSegment(sketch, "E70.0.49.1", {"start": v(11.43, -250.05) * mm, "end": v(11.43, -250.3) * mm});
            skLineSegment(sketch, "E70.0.49.2", {"start": v(11.43, -250.3) * mm, "end": v(12.7, -250.3) * mm});
            skLineSegment(sketch, "E70.0.50.0", {"start": v(12.7, -251.05) * mm, "end": v(11.43, -251.05) * mm});
            skLineSegment(sketch, "E70.0.50.1", {"start": v(11.43, -251.05) * mm, "end": v(11.43, -251.3) * mm});
            skLineSegment(sketch, "E70.0.50.2", {"start": v(11.43, -251.3) * mm, "end": v(12.7, -251.3) * mm});
            skLineSegment(sketch, "E70.0.51.0", {"start": v(12.7, -252.05) * mm, "end": v(11.43, -252.05) * mm});
            skLineSegment(sketch, "E70.0.51.1", {"start": v(11.43, -252.05) * mm, "end": v(11.43, -252.3) * mm});
            skLineSegment(sketch, "E70.0.51.2", {"start": v(11.43, -252.3) * mm, "end": v(12.7, -252.3) * mm});
            skLineSegment(sketch, "E70.0.52.0", {"start": v(12.7, -253.05) * mm, "end": v(11.43, -253.05) * mm});
            skLineSegment(sketch, "E70.0.52.1", {"start": v(11.43, -253.05) * mm, "end": v(11.43, -253.3) * mm});
            skLineSegment(sketch, "E70.0.52.2", {"start": v(11.43, -253.3) * mm, "end": v(12.7, -253.3) * mm});
            skLineSegment(sketch, "E70.0.53.0", {"start": v(12.7, -254.05) * mm, "end": v(11.43, -254.05) * mm});
            skLineSegment(sketch, "E70.0.53.1", {"start": v(11.43, -254.05) * mm, "end": v(11.43, -254.3) * mm});
            skLineSegment(sketch, "E70.0.53.2", {"start": v(11.43, -254.3) * mm, "end": v(12.7, -254.3) * mm});
            skLineSegment(sketch, "E70.0.54.0", {"start": v(12.7, -255.05) * mm, "end": v(11.43, -255.05) * mm});
            skLineSegment(sketch, "E70.0.54.1", {"start": v(11.43, -255.05) * mm, "end": v(11.43, -255.3) * mm});
            skLineSegment(sketch, "E70.0.54.2", {"start": v(11.43, -255.3) * mm, "end": v(12.7, -255.3) * mm});
            skLineSegment(sketch, "E70.0.55.0", {"start": v(12.7, -256.05) * mm, "end": v(11.43, -256.05) * mm});
            skLineSegment(sketch, "E70.0.55.1", {"start": v(11.43, -256.05) * mm, "end": v(11.43, -256.3) * mm});
            skLineSegment(sketch, "E70.0.55.2", {"start": v(11.43, -256.3) * mm, "end": v(12.7, -256.3) * mm});
            skLineSegment(sketch, "E70.0.56.0", {"start": v(12.7, -257.05) * mm, "end": v(11.43, -257.05) * mm});
            skLineSegment(sketch, "E70.0.56.1", {"start": v(11.43, -257.05) * mm, "end": v(11.43, -257.3) * mm});
            skLineSegment(sketch, "E70.0.56.2", {"start": v(11.43, -257.3) * mm, "end": v(12.7, -257.3) * mm});
            skLineSegment(sketch, "E70.0.57.0", {"start": v(12.7, -258.05) * mm, "end": v(11.43, -258.05) * mm});
            skLineSegment(sketch, "E70.0.57.1", {"start": v(11.43, -258.05) * mm, "end": v(11.43, -258.3) * mm});
            skLineSegment(sketch, "E70.0.57.2", {"start": v(11.43, -258.3) * mm, "end": v(12.7, -258.3) * mm});
            skLineSegment(sketch, "E70.0.58.0", {"start": v(12.7, -259.05) * mm, "end": v(11.43, -259.05) * mm});
            skLineSegment(sketch, "E70.0.58.1", {"start": v(11.43, -259.05) * mm, "end": v(11.43, -259.3) * mm});
            skLineSegment(sketch, "E70.0.58.2", {"start": v(11.43, -259.3) * mm, "end": v(12.7, -259.3) * mm});
            skLineSegment(sketch, "E70.0.59.0", {"start": v(12.7, -260.05) * mm, "end": v(11.43, -260.05) * mm});
            skLineSegment(sketch, "E70.0.59.1", {"start": v(11.43, -260.05) * mm, "end": v(11.43, -260.3) * mm});
            skLineSegment(sketch, "E70.0.59.2", {"start": v(11.43, -260.3) * mm, "end": v(12.7, -260.3) * mm});
            skLineSegment(sketch, "E70.0.60.0", {"start": v(12.7, -261.05) * mm, "end": v(11.43, -261.05) * mm});
            skLineSegment(sketch, "E70.0.60.1", {"start": v(11.43, -261.05) * mm, "end": v(11.43, -261.3) * mm});
            skLineSegment(sketch, "E70.0.60.2", {"start": v(11.43, -261.3) * mm, "end": v(12.7, -261.3) * mm});
            skLineSegment(sketch, "E70.0.61.0", {"start": v(12.7, -262.05) * mm, "end": v(11.43, -262.05) * mm});
            skLineSegment(sketch, "E70.0.61.1", {"start": v(11.43, -262.05) * mm, "end": v(11.43, -262.3) * mm});
            skLineSegment(sketch, "E70.0.61.2", {"start": v(11.43, -262.3) * mm, "end": v(12.7, -262.3) * mm});
            skLineSegment(sketch, "E70.0.62.0", {"start": v(12.7, -263.05) * mm, "end": v(11.43, -263.05) * mm});
            skLineSegment(sketch, "E70.0.62.1", {"start": v(11.43, -263.05) * mm, "end": v(11.43, -263.3) * mm});
            skLineSegment(sketch, "E70.0.62.2", {"start": v(11.43, -263.3) * mm, "end": v(12.7, -263.3) * mm});
            skLineSegment(sketch, "E70.0.63.0", {"start": v(12.7, -264.05) * mm, "end": v(11.43, -264.05) * mm});
            skLineSegment(sketch, "E70.0.63.1", {"start": v(11.43, -264.05) * mm, "end": v(11.43, -264.3) * mm});
            skLineSegment(sketch, "E70.0.63.2", {"start": v(11.43, -264.3) * mm, "end": v(12.7, -264.3) * mm});
            skLineSegment(sketch, "E70.0.64.0", {"start": v(12.7, -265.05) * mm, "end": v(11.43, -265.05) * mm});
            skLineSegment(sketch, "E70.0.64.1", {"start": v(11.43, -265.05) * mm, "end": v(11.43, -265.3) * mm});
            skLineSegment(sketch, "E70.0.64.2", {"start": v(11.43, -265.3) * mm, "end": v(12.7, -265.3) * mm});
            skLineSegment(sketch, "E70.0.65.0", {"start": v(12.7, -266.05) * mm, "end": v(11.43, -266.05) * mm});
            skLineSegment(sketch, "E70.0.65.1", {"start": v(11.43, -266.05) * mm, "end": v(11.43, -266.3) * mm});
            skLineSegment(sketch, "E70.0.65.2", {"start": v(11.43, -266.3) * mm, "end": v(12.7, -266.3) * mm});
            skLineSegment(sketch, "E70.0.66.0", {"start": v(12.7, -267.05) * mm, "end": v(11.43, -267.05) * mm});
            skLineSegment(sketch, "E70.0.66.1", {"start": v(11.43, -267.05) * mm, "end": v(11.43, -267.3) * mm});
            skLineSegment(sketch, "E70.0.66.2", {"start": v(11.43, -267.3) * mm, "end": v(12.7, -267.3) * mm});
            skLineSegment(sketch, "E70.0.67.0", {"start": v(12.7, -268.05) * mm, "end": v(11.43, -268.05) * mm});
            skLineSegment(sketch, "E70.0.67.1", {"start": v(11.43, -268.05) * mm, "end": v(11.43, -268.3) * mm});
            skLineSegment(sketch, "E70.0.67.2", {"start": v(11.43, -268.3) * mm, "end": v(12.7, -268.3) * mm});
            skLineSegment(sketch, "E70.0.68.0", {"start": v(12.7, -269.05) * mm, "end": v(11.43, -269.05) * mm});
            skLineSegment(sketch, "E70.0.68.1", {"start": v(11.43, -269.05) * mm, "end": v(11.43, -269.3) * mm});
            skLineSegment(sketch, "E70.0.68.2", {"start": v(11.43, -269.3) * mm, "end": v(12.7, -269.3) * mm});
            skLineSegment(sketch, "E70.0.69.0", {"start": v(12.7, -270.05) * mm, "end": v(11.43, -270.05) * mm});
            skLineSegment(sketch, "E70.0.69.1", {"start": v(11.43, -270.05) * mm, "end": v(11.43, -270.3) * mm});
            skLineSegment(sketch, "E70.0.69.2", {"start": v(11.43, -270.3) * mm, "end": v(12.7, -270.3) * mm});
            skLineSegment(sketch, "E70.0.70.0", {"start": v(12.7, -271.05) * mm, "end": v(11.43, -271.05) * mm});
            skLineSegment(sketch, "E70.0.70.1", {"start": v(11.43, -271.05) * mm, "end": v(11.43, -271.3) * mm});
            skLineSegment(sketch, "E70.0.70.2", {"start": v(11.43, -271.3) * mm, "end": v(12.7, -271.3) * mm});
            skLineSegment(sketch, "E70.0.71.0", {"start": v(12.7, -272.05) * mm, "end": v(11.43, -272.05) * mm});
            skLineSegment(sketch, "E70.0.71.1", {"start": v(11.43, -272.05) * mm, "end": v(11.43, -272.3) * mm});
            skLineSegment(sketch, "E70.0.71.2", {"start": v(11.43, -272.3) * mm, "end": v(12.7, -272.3) * mm});
            skLineSegment(sketch, "E70.0.72.0", {"start": v(12.7, -273.05) * mm, "end": v(11.43, -273.05) * mm});
            skLineSegment(sketch, "E70.0.72.1", {"start": v(11.43, -273.05) * mm, "end": v(11.43, -273.3) * mm});
            skLineSegment(sketch, "E70.0.72.2", {"start": v(11.43, -273.3) * mm, "end": v(12.7, -273.3) * mm});
            skLineSegment(sketch, "E70.0.73.0", {"start": v(12.7, -274.05) * mm, "end": v(11.43, -274.05) * mm});
            skLineSegment(sketch, "E70.0.73.1", {"start": v(11.43, -274.05) * mm, "end": v(11.43, -274.3) * mm});
            skLineSegment(sketch, "E70.0.73.2", {"start": v(11.43, -274.3) * mm, "end": v(12.7, -274.3) * mm});
            skLineSegment(sketch, "E70.0.74.0", {"start": v(12.7, -275.05) * mm, "end": v(11.43, -275.05) * mm});
            skLineSegment(sketch, "E70.0.74.1", {"start": v(11.43, -275.05) * mm, "end": v(11.43, -275.3) * mm});
            skLineSegment(sketch, "E70.0.74.2", {"start": v(11.43, -275.3) * mm, "end": v(12.7, -275.3) * mm});
            skLineSegment(sketch, "E70.0.75.0", {"start": v(12.7, -276.05) * mm, "end": v(11.43, -276.05) * mm});
            skLineSegment(sketch, "E70.0.75.1", {"start": v(11.43, -276.05) * mm, "end": v(11.43, -276.3) * mm});
            skLineSegment(sketch, "E70.0.75.2", {"start": v(11.43, -276.3) * mm, "end": v(12.7, -276.3) * mm});
            skLineSegment(sketch, "E70.0.76.0", {"start": v(12.7, -277.05) * mm, "end": v(11.43, -277.05) * mm});
            skLineSegment(sketch, "E70.0.76.1", {"start": v(11.43, -277.05) * mm, "end": v(11.43, -277.3) * mm});
            skLineSegment(sketch, "E70.0.76.2", {"start": v(11.43, -277.3) * mm, "end": v(12.7, -277.3) * mm});
            skLineSegment(sketch, "E70.0.77.0", {"start": v(12.7, -278.05) * mm, "end": v(11.43, -278.05) * mm});
            skLineSegment(sketch, "E70.0.77.1", {"start": v(11.43, -278.05) * mm, "end": v(11.43, -278.3) * mm});
            skLineSegment(sketch, "E70.0.77.2", {"start": v(11.43, -278.3) * mm, "end": v(12.7, -278.3) * mm});
            skLineSegment(sketch, "E70.0.78.0", {"start": v(12.7, -279.05) * mm, "end": v(11.43, -279.05) * mm});
            skLineSegment(sketch, "E70.0.78.1", {"start": v(11.43, -279.05) * mm, "end": v(11.43, -279.3) * mm});
            skLineSegment(sketch, "E70.0.78.2", {"start": v(11.43, -279.3) * mm, "end": v(12.7, -279.3) * mm});
            skLineSegment(sketch, "E70.0.79.0", {"start": v(12.7, -280.05) * mm, "end": v(11.43, -280.05) * mm});
            skLineSegment(sketch, "E70.0.79.1", {"start": v(11.43, -280.05) * mm, "end": v(11.43, -280.3) * mm});
            skLineSegment(sketch, "E70.0.79.2", {"start": v(11.43, -280.3) * mm, "end": v(12.7, -280.3) * mm});
            skLineSegment(sketch, "E70.0.80.0", {"start": v(12.7, -281.05) * mm, "end": v(11.43, -281.05) * mm});
            skLineSegment(sketch, "E70.0.80.1", {"start": v(11.43, -281.05) * mm, "end": v(11.43, -281.3) * mm});
            skLineSegment(sketch, "E70.0.80.2", {"start": v(11.43, -281.3) * mm, "end": v(12.7, -281.3) * mm});
            skLineSegment(sketch, "E70.0.81.0", {"start": v(12.7, -282.05) * mm, "end": v(11.43, -282.05) * mm});
            skLineSegment(sketch, "E70.0.81.1", {"start": v(11.43, -282.05) * mm, "end": v(11.43, -282.3) * mm});
            skLineSegment(sketch, "E70.0.81.2", {"start": v(11.43, -282.3) * mm, "end": v(12.7, -282.3) * mm});
            skLineSegment(sketch, "E70.0.82.0", {"start": v(12.7, -283.05) * mm, "end": v(11.43, -283.05) * mm});
            skLineSegment(sketch, "E70.0.82.1", {"start": v(11.43, -283.05) * mm, "end": v(11.43, -283.3) * mm});
            skLineSegment(sketch, "E70.0.82.2", {"start": v(11.43, -283.3) * mm, "end": v(12.7, -283.3) * mm});
            skLineSegment(sketch, "E70.0.83.0", {"start": v(12.7, -284.05) * mm, "end": v(11.43, -284.05) * mm});
            skLineSegment(sketch, "E70.0.83.1", {"start": v(11.43, -284.05) * mm, "end": v(11.43, -284.3) * mm});
            skLineSegment(sketch, "E70.0.83.2", {"start": v(11.43, -284.3) * mm, "end": v(12.7, -284.3) * mm});
            skLineSegment(sketch, "E70.0.84.0", {"start": v(12.7, -285.05) * mm, "end": v(11.43, -285.05) * mm});
            skLineSegment(sketch, "E70.0.84.1", {"start": v(11.43, -285.05) * mm, "end": v(11.43, -285.3) * mm});
            skLineSegment(sketch, "E70.0.84.2", {"start": v(11.43, -285.3) * mm, "end": v(12.7, -285.3) * mm});
            skLineSegment(sketch, "E70.0.85.0", {"start": v(12.7, -286.05) * mm, "end": v(11.43, -286.05) * mm});
            skLineSegment(sketch, "E70.0.85.1", {"start": v(11.43, -286.05) * mm, "end": v(11.43, -286.3) * mm});
            skLineSegment(sketch, "E70.0.85.2", {"start": v(11.43, -286.3) * mm, "end": v(12.7, -286.3) * mm});
            skLineSegment(sketch, "E70.0.86.0", {"start": v(12.7, -287.05) * mm, "end": v(11.43, -287.05) * mm});
            skLineSegment(sketch, "E70.0.86.1", {"start": v(11.43, -287.05) * mm, "end": v(11.43, -287.3) * mm});
            skLineSegment(sketch, "E70.0.86.2", {"start": v(11.43, -287.3) * mm, "end": v(12.7, -287.3) * mm});
            skLineSegment(sketch, "E70.0.87.0", {"start": v(12.7, -288.05) * mm, "end": v(11.43, -288.05) * mm});
            skLineSegment(sketch, "E70.0.87.1", {"start": v(11.43, -288.05) * mm, "end": v(11.43, -288.3) * mm});
            skLineSegment(sketch, "E70.0.87.2", {"start": v(11.43, -288.3) * mm, "end": v(12.7, -288.3) * mm});
            skLineSegment(sketch, "E70.0.88.0", {"start": v(12.7, -289.05) * mm, "end": v(11.43, -289.05) * mm});
            skLineSegment(sketch, "E70.0.88.1", {"start": v(11.43, -289.05) * mm, "end": v(11.43, -289.3) * mm});
            skLineSegment(sketch, "E70.0.88.2", {"start": v(11.43, -289.3) * mm, "end": v(12.7, -289.3) * mm});
            skLineSegment(sketch, "E70.0.89.0", {"start": v(12.7, -290.05) * mm, "end": v(11.43, -290.05) * mm});
            skLineSegment(sketch, "E70.0.89.1", {"start": v(11.43, -290.05) * mm, "end": v(11.43, -290.3) * mm});
            skLineSegment(sketch, "E70.0.89.2", {"start": v(11.43, -290.3) * mm, "end": v(12.7, -290.3) * mm});
            skLineSegment(sketch, "E70.0.90.0", {"start": v(12.7, -291.05) * mm, "end": v(11.43, -291.05) * mm});
            skLineSegment(sketch, "E70.0.90.1", {"start": v(11.43, -291.05) * mm, "end": v(11.43, -291.3) * mm});
            skLineSegment(sketch, "E70.0.90.2", {"start": v(11.43, -291.3) * mm, "end": v(12.7, -291.3) * mm});
            skLineSegment(sketch, "E70.0.91.0", {"start": v(12.7, -292.05) * mm, "end": v(11.43, -292.05) * mm});
            skLineSegment(sketch, "E70.0.91.1", {"start": v(11.43, -292.05) * mm, "end": v(11.43, -292.3) * mm});
            skLineSegment(sketch, "E70.0.91.2", {"start": v(11.43, -292.3) * mm, "end": v(12.7, -292.3) * mm});
            skLineSegment(sketch, "E70.0.92.0", {"start": v(12.7, -293.05) * mm, "end": v(11.43, -293.05) * mm});
            skLineSegment(sketch, "E70.0.92.1", {"start": v(11.43, -293.05) * mm, "end": v(11.43, -293.3) * mm});
            skLineSegment(sketch, "E70.0.92.2", {"start": v(11.43, -293.3) * mm, "end": v(12.7, -293.3) * mm});
            skLineSegment(sketch, "E70.0.93.0", {"start": v(12.7, -294.05) * mm, "end": v(11.43, -294.05) * mm});
            skLineSegment(sketch, "E70.0.93.1", {"start": v(11.43, -294.05) * mm, "end": v(11.43, -294.3) * mm});
            skLineSegment(sketch, "E70.0.93.2", {"start": v(11.43, -294.3) * mm, "end": v(12.7, -294.3) * mm});
            skLineSegment(sketch, "E70.0.94.0", {"start": v(12.7, -295.05) * mm, "end": v(11.43, -295.05) * mm});
            skLineSegment(sketch, "E70.0.94.1", {"start": v(11.43, -295.05) * mm, "end": v(11.43, -295.3) * mm});
            skLineSegment(sketch, "E70.0.94.2", {"start": v(11.43, -295.3) * mm, "end": v(12.7, -295.3) * mm});
            skLineSegment(sketch, "E70.0.95.0", {"start": v(12.7, -296.05) * mm, "end": v(11.43, -296.05) * mm});
            skLineSegment(sketch, "E70.0.95.1", {"start": v(11.43, -296.05) * mm, "end": v(11.43, -296.3) * mm});
            skLineSegment(sketch, "E70.0.95.2", {"start": v(11.43, -296.3) * mm, "end": v(12.7, -296.3) * mm});
            skLineSegment(sketch, "E70.0.96.0", {"start": v(12.7, -297.05) * mm, "end": v(11.43, -297.05) * mm});
            skLineSegment(sketch, "E70.0.96.1", {"start": v(11.43, -297.05) * mm, "end": v(11.43, -297.3) * mm});
            skLineSegment(sketch, "E70.0.96.2", {"start": v(11.43, -297.3) * mm, "end": v(12.7, -297.3) * mm});
            skLineSegment(sketch, "E70.0.97.0", {"start": v(12.7, -298.05) * mm, "end": v(11.43, -298.05) * mm});
            skLineSegment(sketch, "E70.0.97.1", {"start": v(11.43, -298.05) * mm, "end": v(11.43, -298.3) * mm});
            skLineSegment(sketch, "E70.0.97.2", {"start": v(11.43, -298.3) * mm, "end": v(12.7, -298.3) * mm});
            skLineSegment(sketch, "E70.0.98.0", {"start": v(12.7, -299.05) * mm, "end": v(11.43, -299.05) * mm});
            skLineSegment(sketch, "E70.0.98.1", {"start": v(11.43, -299.05) * mm, "end": v(11.43, -299.3) * mm});
            skLineSegment(sketch, "E70.0.98.2", {"start": v(11.43, -299.3) * mm, "end": v(12.7, -299.3) * mm});
            skLineSegment(sketch, "E70.0.99.0", {"start": v(12.7, -300.05) * mm, "end": v(11.43, -300.05) * mm});
            skLineSegment(sketch, "E70.0.99.1", {"start": v(11.43, -300.05) * mm, "end": v(11.43, -300.3) * mm});
            skLineSegment(sketch, "E70.0.99.2", {"start": v(11.43, -300.3) * mm, "end": v(12.7, -300.3) * mm});
            skLineSegment(sketch, "E70.direction1", {"start": v(11.43, -201.05) * mm, "end": v(36.83, -201.05) * mm, "construction": true});
            skLineSegment(sketch, "E70.direction2", {"start": v(11.43, -201.05) * mm, "end": v(11.43, -202.05) * mm, "construction": true});
            skLineSegment(sketch, "E71.0.1.0", {"start": v(12.7, -301.05) * mm, "end": v(11.43, -301.05) * mm});
            skLineSegment(sketch, "E71.0.1.1", {"start": v(11.43, -301.3) * mm, "end": v(12.7, -301.3) * mm});
            skLineSegment(sketch, "E71.0.1.2", {"start": v(11.43, -301.05) * mm, "end": v(11.43, -301.3) * mm});
            skLineSegment(sketch, "E71.0.2.0", {"start": v(12.7, -302.05) * mm, "end": v(11.43, -302.05) * mm});
            skLineSegment(sketch, "E71.0.2.1", {"start": v(11.43, -302.3) * mm, "end": v(12.7, -302.3) * mm});
            skLineSegment(sketch, "E71.0.2.2", {"start": v(11.43, -302.05) * mm, "end": v(11.43, -302.3) * mm});
            skLineSegment(sketch, "E71.0.3.0", {"start": v(12.7, -303.05) * mm, "end": v(11.43, -303.05) * mm});
            skLineSegment(sketch, "E71.0.3.1", {"start": v(11.43, -303.3) * mm, "end": v(12.7, -303.3) * mm});
            skLineSegment(sketch, "E71.0.3.2", {"start": v(11.43, -303.05) * mm, "end": v(11.43, -303.3) * mm});
            skLineSegment(sketch, "E71.0.4.0", {"start": v(12.7, -304.05) * mm, "end": v(11.43, -304.05) * mm});
            skLineSegment(sketch, "E71.0.4.1", {"start": v(11.43, -304.3) * mm, "end": v(12.7, -304.3) * mm});
            skLineSegment(sketch, "E71.0.4.2", {"start": v(11.43, -304.05) * mm, "end": v(11.43, -304.3) * mm});
            skLineSegment(sketch, "E71.0.5.0", {"start": v(12.7, -305.05) * mm, "end": v(11.43, -305.05) * mm});
            skLineSegment(sketch, "E71.0.5.1", {"start": v(11.43, -305.3) * mm, "end": v(12.7, -305.3) * mm});
            skLineSegment(sketch, "E71.0.5.2", {"start": v(11.43, -305.05) * mm, "end": v(11.43, -305.3) * mm});
            skLineSegment(sketch, "E71.0.6.0", {"start": v(12.7, -306.05) * mm, "end": v(11.43, -306.05) * mm});
            skLineSegment(sketch, "E71.0.6.1", {"start": v(11.43, -306.3) * mm, "end": v(12.7, -306.3) * mm});
            skLineSegment(sketch, "E71.0.6.2", {"start": v(11.43, -306.05) * mm, "end": v(11.43, -306.3) * mm});
            skLineSegment(sketch, "E71.0.7.0", {"start": v(12.7, -307.05) * mm, "end": v(11.43, -307.05) * mm});
            skLineSegment(sketch, "E71.0.7.1", {"start": v(11.43, -307.3) * mm, "end": v(12.7, -307.3) * mm});
            skLineSegment(sketch, "E71.0.7.2", {"start": v(11.43, -307.05) * mm, "end": v(11.43, -307.3) * mm});
            skLineSegment(sketch, "E71.direction1", {"start": v(11.43, -300.05) * mm, "end": v(36.83, -300.05) * mm, "construction": true});
            skLineSegment(sketch, "E71.direction2", {"start": v(11.43, -300.05) * mm, "end": v(11.43, -301.05) * mm, "construction": true});
            skSolve(sketch);
        }
        {
            var Q0;
            Q0 = qSketchRegion(id + "F4", true);
            extrude(context, id + "F5", {"entities" : qUnion([Q0]), "operationType" : NewBodyOperationType.REMOVE, "oppositeDirection" : true, "depth" : 3.17 * mm});
        }
        {
            var Q0;
            Q0=makeQuery(id+"F1.opExtrude","SWEPT_FACE",FACE,{"disambiguationData":[OSD([sQuery(id+"F0.wireOp",EDGE,"E7")])]});
            var sketch = newSketch(context, id + "F6", { "sketchPlane" : qUnion([Q0])});
            skText(sketch, "E72", { "text": "INCH", "fontName": "OpenSans-Regular.ttf"});
            skLineSegment(sketch, "E73", {"start": v(-5.36, -283.77) * mm, "end": v(-2.33, -283.77) * mm});
            skLineSegment(sketch, "E74", {"start": v(-5.36, -281.2) * mm, "end": v(-2.33, -281.2) * mm});
            skLineSegment(sketch, "E75.0.1.0", {"start": v(-5.36, -258.37) * mm, "end": v(-2.33, -258.37) * mm});
            skLineSegment(sketch, "E75.0.1.1", {"start": v(-5.36, -255.8) * mm, "end": v(-2.33, -255.8) * mm});
            skLineSegment(sketch, "E75.0.2.0", {"start": v(-5.36, -232.97) * mm, "end": v(-2.33, -232.97) * mm});
            skLineSegment(sketch, "E75.0.2.1", {"start": v(-5.36, -230.4) * mm, "end": v(-2.33, -230.4) * mm});
            skLineSegment(sketch, "E75.0.3.0", {"start": v(-5.36, -207.57) * mm, "end": v(-2.33, -207.57) * mm});
            skLineSegment(sketch, "E75.0.3.1", {"start": v(-5.36, -205) * mm, "end": v(-2.33, -205) * mm});
            skLineSegment(sketch, "E75.0.4.0", {"start": v(-5.36, -182.17) * mm, "end": v(-2.33, -182.17) * mm});
            skLineSegment(sketch, "E75.0.4.1", {"start": v(-5.36, -179.6) * mm, "end": v(-2.33, -179.6) * mm});
            skLineSegment(sketch, "E75.0.5.0", {"start": v(-5.36, -156.77) * mm, "end": v(-2.33, -156.77) * mm});
            skLineSegment(sketch, "E75.0.5.1", {"start": v(-5.36, -154.2) * mm, "end": v(-2.33, -154.2) * mm});
            skLineSegment(sketch, "E75.0.6.0", {"start": v(-5.36, -131.37) * mm, "end": v(-2.33, -131.37) * mm});
            skLineSegment(sketch, "E75.0.6.1", {"start": v(-5.36, -128.8) * mm, "end": v(-2.33, -128.8) * mm});
            skLineSegment(sketch, "E75.0.7.0", {"start": v(-5.36, -105.97) * mm, "end": v(-2.33, -105.97) * mm});
            skLineSegment(sketch, "E75.0.7.1", {"start": v(-5.36, -103.4) * mm, "end": v(-2.33, -103.4) * mm});
            skLineSegment(sketch, "E75.0.8.0", {"start": v(-5.36, -80.57) * mm, "end": v(-2.33, -80.57) * mm});
            skLineSegment(sketch, "E75.0.8.1", {"start": v(-5.36, -78) * mm, "end": v(-2.33, -78) * mm});
            skLineSegment(sketch, "E75.0.9.0", {"start": v(-5.36, -55.17) * mm, "end": v(-2.33, -55.17) * mm});
            skLineSegment(sketch, "E75.0.9.1", {"start": v(-5.36, -52.6) * mm, "end": v(-2.33, -52.6) * mm});
            skLineSegment(sketch, "E75.0.10.0", {"start": v(-5.36, -29.77) * mm, "end": v(-2.33, -29.77) * mm});
            skLineSegment(sketch, "E75.0.10.1", {"start": v(-5.36, -27.2) * mm, "end": v(-2.33, -27.2) * mm});
            skLineSegment(sketch, "E75.0.11.0", {"start": v(-5.36, -4.37) * mm, "end": v(-2.33, -4.37) * mm});
            skLineSegment(sketch, "E75.direction1", {"start": v(-5.36, -283.77) * mm, "end": v(20.04, -283.77) * mm, "construction": true});
            skLineSegment(sketch, "E75.direction2", {"start": v(-5.36, -283.77) * mm, "end": v(-5.36, -258.37) * mm, "construction": true});
            skText(sketch, "E76", { "text": "1", "fontName": "OpenSans-Regular.ttf"});
            skText(sketch, "E77", { "text": "2", "fontName": "OpenSans-Regular.ttf"});
            skText(sketch, "E78", { "text": "3", "fontName": "OpenSans-Regular.ttf"});
            skText(sketch, "E79", { "text": "4", "fontName": "OpenSans-Regular.ttf"});
            skText(sketch, "E80", { "text": "5", "fontName": "OpenSans-Regular.ttf"});
            skText(sketch, "E81", { "text": "6", "fontName": "OpenSans-Regular.ttf"});
            skText(sketch, "E82", { "text": "7", "fontName": "OpenSans-Regular.ttf"});
            skText(sketch, "E83", { "text": "8", "fontName": "OpenSans-Regular.ttf"});
            skText(sketch, "E84", { "text": "9", "fontName": "OpenSans-Regular.ttf"});
            skText(sketch, "E85", { "text": "10", "fontName": "OpenSans-Regular.ttf"});
            skText(sketch, "E86", { "text": "11", "fontName": "OpenSans-Regular.ttf"});
            skText(sketch, "E87", { "text": "12", "fontName": "OpenSans-Regular.ttf"});
            const initialGuessF6  = {"E72": [-0.00233, -0.31024, 0, 1, 0.00303], "E76": [-0.00274, -0.28332, 0, 1, 0.00257], "E77": [-0.0028, -0.25817, 0, 1, 0.00257], "E78": [-0.00284, -0.23277, 0, 1, 0.00257], "E79": [-0.00286, -0.2074, 0, 1, 0.00257], "E80": [-0.00271, -0.18187, 0, 1, 0.00257], "E81": [-0.00273, -0.15663, 0, 1, 0.00257], "E82": [-0.00284, -0.13102, 0, 1, 0.00257], "E83": [-0.00274, -0.10582, 0, 1, 0.00257], "E84": [-0.0028, -0.08032, 0, 1, 0.00257], "E85": [-0.0028, -0.05595, 0, 1, 0.00257], "E86": [-0.00284, -0.03018, 0, 1, 0.00257], "E87": [-0.00282, -0.00524, 0, 1, 0.00257]};
            skSetInitialGuess(sketch, initialGuessF6);
            skSolve(sketch);
        }
        {
            var Q0;
            Q0 = qSketchRegion(id + "F6", true);
            extrude(context, id + "F7", {"entities" : qUnion([Q0]), "operationType" : NewBodyOperationType.REMOVE, "oppositeDirection" : true, "depth" : 1.27 * mm});
        }
        {
            var Q0;
            {var subQ0=sQuery(id+"F0.wireOp",EDGE,"E7");var subQ3=sQuery(id+"F0.wireOp",EDGE,"E3");Q0=makeQuery(id+"F7.boolean.opBoolean","SPLIT",FACE,{"disambiguationData":[TD([makeQuery(id+"F1.opExtrude","SWEPT_FACE",FACE,{"disambiguationData":[OSD([subQ3])]})])],"derivedFrom":makeQuery(id+"F1.opExtrude","SWEPT_FACE",FACE,{"disambiguationData":[OSD([subQ0])]})});}
            var sketch = newSketch(context, id + "F8", { "sketchPlane" : qUnion([Q0])});
            skText(sketch, "E88", { "text": "cm\n", "fontName": "OpenSans-Regular.ttf"});
            skLineSegment(sketch, "E89", {"start": v(6.14, -7.35) * mm, "end": v(3.56, -7.35) * mm});
            skLineSegment(sketch, "E90", {"start": v(6.14, -12.16) * mm, "end": v(3.56, -12.16) * mm});
            skLineSegment(sketch, "E91", {"start": v(6.14, -14.24) * mm, "end": v(3.56, -14.24) * mm});
            skLineSegment(sketch, "E92.0.1.0", {"start": v(6.14, -22.16) * mm, "end": v(3.56, -22.16) * mm});
            skLineSegment(sketch, "E92.0.1.1", {"start": v(6.14, -24.24) * mm, "end": v(3.56, -24.24) * mm});
            skLineSegment(sketch, "E92.0.2.0", {"start": v(6.14, -32.16) * mm, "end": v(3.56, -32.16) * mm});
            skLineSegment(sketch, "E92.0.2.1", {"start": v(6.14, -34.24) * mm, "end": v(3.56, -34.24) * mm});
            skLineSegment(sketch, "E92.0.3.0", {"start": v(6.14, -42.16) * mm, "end": v(3.56, -42.16) * mm});
            skLineSegment(sketch, "E92.0.3.1", {"start": v(6.14, -44.24) * mm, "end": v(3.56, -44.24) * mm});
            skLineSegment(sketch, "E92.0.4.0", {"start": v(6.14, -52.16) * mm, "end": v(3.56, -52.16) * mm});
            skLineSegment(sketch, "E92.0.4.1", {"start": v(6.14, -54.24) * mm, "end": v(3.56, -54.24) * mm});
            skLineSegment(sketch, "E92.0.5.0", {"start": v(6.14, -62.16) * mm, "end": v(3.56, -62.16) * mm});
            skLineSegment(sketch, "E92.0.5.1", {"start": v(6.14, -64.24) * mm, "end": v(3.56, -64.24) * mm});
            skLineSegment(sketch, "E92.0.6.0", {"start": v(6.14, -72.16) * mm, "end": v(3.56, -72.16) * mm});
            skLineSegment(sketch, "E92.0.6.1", {"start": v(6.14, -74.24) * mm, "end": v(3.56, -74.24) * mm});
            skLineSegment(sketch, "E92.0.7.0", {"start": v(6.14, -82.16) * mm, "end": v(3.56, -82.16) * mm});
            skLineSegment(sketch, "E92.0.7.1", {"start": v(6.14, -84.24) * mm, "end": v(3.56, -84.24) * mm});
            skLineSegment(sketch, "E92.0.8.0", {"start": v(6.14, -92.16) * mm, "end": v(3.56, -92.16) * mm});
            skLineSegment(sketch, "E92.0.8.1", {"start": v(6.14, -94.24) * mm, "end": v(3.56, -94.24) * mm});
            skLineSegment(sketch, "E92.0.9.0", {"start": v(6.14, -102.16) * mm, "end": v(3.56, -102.16) * mm});
            skLineSegment(sketch, "E92.0.9.1", {"start": v(6.14, -104.24) * mm, "end": v(3.56, -104.24) * mm});
            skLineSegment(sketch, "E92.0.10.0", {"start": v(6.14, -112.16) * mm, "end": v(3.56, -112.16) * mm});
            skLineSegment(sketch, "E92.0.10.1", {"start": v(6.14, -114.24) * mm, "end": v(3.56, -114.24) * mm});
            skLineSegment(sketch, "E92.0.11.0", {"start": v(6.14, -122.16) * mm, "end": v(3.56, -122.16) * mm});
            skLineSegment(sketch, "E92.0.13.0", {"start": v(6.14, -142.16) * mm, "end": v(3.56, -142.16) * mm});
            skLineSegment(sketch, "E92.0.14.0", {"start": v(6.14, -152.16) * mm, "end": v(3.56, -152.16) * mm});
            skLineSegment(sketch, "E92.0.15.0", {"start": v(6.14, -162.16) * mm, "end": v(3.56, -162.16) * mm});
            skLineSegment(sketch, "E92.0.16.0", {"start": v(6.14, -172.16) * mm, "end": v(3.56, -172.16) * mm});
            skLineSegment(sketch, "E92.0.17.0", {"start": v(6.14, -182.16) * mm, "end": v(3.56, -182.16) * mm});
            skLineSegment(sketch, "E92.0.18.0", {"start": v(6.14, -192.16) * mm, "end": v(3.56, -192.16) * mm});
            skLineSegment(sketch, "E92.0.20.1", {"start": v(6.14, -214.24) * mm, "end": v(3.56, -214.24) * mm});
            skLineSegment(sketch, "E92.direction1", {"start": v(3.56, -12.16) * mm, "end": v(28.96, -12.16) * mm, "construction": true});
            skLineSegment(sketch, "E92.direction2", {"start": v(3.56, -12.16) * mm, "end": v(3.56, -22.16) * mm, "construction": true});
            skText(sketch, "E93", { "text": "1", "fontName": "OpenSans-Regular.ttf"});
            skText(sketch, "E94", { "text": "2", "fontName": "OpenSans-Regular.ttf"});
            skText(sketch, "E95", { "text": "3", "fontName": "OpenSans-Regular.ttf"});
            skText(sketch, "E96", { "text": "4", "fontName": "OpenSans-Regular.ttf"});
            skText(sketch, "E97", { "text": "5", "fontName": "OpenSans-Regular.ttf"});
            skText(sketch, "E98", { "text": "6", "fontName": "OpenSans-Regular.ttf"});
            skText(sketch, "E99", { "text": "7", "fontName": "OpenSans-Regular.ttf"});
            skText(sketch, "E100", { "text": "8", "fontName": "OpenSans-Regular.ttf"});
            skText(sketch, "E101", { "text": "9", "fontName": "OpenSans-Regular.ttf"});
            skText(sketch, "E102", { "text": "10", "fontName": "OpenSans-Regular.ttf"});
            skText(sketch, "E103", { "text": "11", "fontName": "OpenSans-Regular.ttf"});
            skText(sketch, "E104", { "text": "12", "fontName": "OpenSans-Regular.ttf"});
            skText(sketch, "E105", { "text": "13", "fontName": "OpenSans-Regular.ttf"});
            skText(sketch, "E106", { "text": "14", "fontName": "OpenSans-Regular.ttf"});
            skText(sketch, "E107", { "text": "15", "fontName": "OpenSans-Regular.ttf"});
            skText(sketch, "E108", { "text": "16", "fontName": "OpenSans-Regular.ttf"});
            skText(sketch, "E109", { "text": "17", "fontName": "OpenSans-Regular.ttf"});
            skText(sketch, "E110", { "text": "18", "fontName": "OpenSans-Regular.ttf"});
            skText(sketch, "E111", { "text": "19", "fontName": "OpenSans-Regular.ttf"});
            skText(sketch, "E112", { "text": "20", "fontName": "OpenSans-Regular.ttf"});
            skText(sketch, "E113", { "text": "21", "fontName": "OpenSans-Regular.ttf"});
            skText(sketch, "E114", { "text": "22", "fontName": "OpenSans-Regular.ttf"});
            skText(sketch, "E115", { "text": "23", "fontName": "OpenSans-Regular.ttf"});
            skText(sketch, "E116", { "text": "24", "fontName": "OpenSans-Regular.ttf"});
            skText(sketch, "E117", { "text": "25", "fontName": "OpenSans-Regular.ttf"});
            skText(sketch, "E118", { "text": "26", "fontName": "OpenSans-Regular.ttf"});
            skText(sketch, "E119", { "text": "27", "fontName": "OpenSans-Regular.ttf"});
            skText(sketch, "E120", { "text": "28", "fontName": "OpenSans-Regular.ttf"});
            skText(sketch, "E121", { "text": "29", "fontName": "OpenSans-Regular.ttf"});
            skText(sketch, "E122", { "text": "30", "fontName": "OpenSans-Regular.ttf"});
            const initialGuessF8  = {"E88": [0.00356, -0.00237, 0, -1, 0.00258], "E93": [0.004, -0.01254, 0, -1, 0.00207], "E94": [0.00408, -0.02243, 0, -1, 0.00207], "E95": [0.00408, -0.0323, 0, -1, 0.00207], "E96": [0.00408, -0.04228, 0, -1, 0.00207], "E97": [0.00416, -0.05232, 0, -1, 0.00207], "E98": [0.00412, -0.06235, 0, -1, 0.00207], "E99": [0.004, -0.0723, 0, -1, 0.00207], "E100": [0.0041, -0.08227, 0, -1, 0.00207], "E101": [0.00406, -0.0923, 0, -1, 0.00207], "E102": [0.00404, -0.1015, 0, -1, 0.00207], "E103": [0.00414, -0.1118, 0, -1, 0.00207], "E104": [0.0041, -0.12144, 0, -1, 0.00207], "E105": [0.00403, -0.13154, 0, -1, 0.00207], "E106": [0.00403, -0.14142, 0, -1, 0.00207], "E107": [0.00412, -0.1514, 0, -1, 0.00207], "E108": [0.00406, -0.1615, 0, -1, 0.00207], "E109": [0.00406, -0.17161, 0, -1, 0.00207], "E110": [0.00408, -0.18157, 0, -1, 0.00207], "E111": [0.00394, -0.19156, 0, -1, 0.00207], "E112": [0.00413, -0.20156, 0, -1, 0.00207], "E113": [0.00413, -0.21178, 0, -1, 0.00207], "E114": [0.00403, -0.22157, 0, -1, 0.00207], "E115": [0.00403, -0.23154, 0, -1, 0.00207], "E116": [0.0041, -0.24153, 0, -1, 0.00207], "E117": [0.004, -0.25156, 0, -1, 0.00207], "E118": [0.004, -0.26148, 0, -1, 0.00207], "E119": [0.00406, -0.27149, 0, -1, 0.00207], "E120": [0.0041, -0.2816, 0, -1, 0.00207], "E121": [0.0041, -0.29147, 0, -1, 0.00207], "E122": [0.004, -0.30154, 0, -1, 0.00207]};
            skSetInitialGuess(sketch, initialGuessF8);
            skSolve(sketch);
        }
        {
            var Q0;
            Q0 = qSketchRegion(id + "F8", true);
            extrude(context, id + "F9", {"entities" : qUnion([Q0]), "operationType" : NewBodyOperationType.REMOVE, "oppositeDirection" : true, "depth" : 1.27 * mm});
        }
    });
